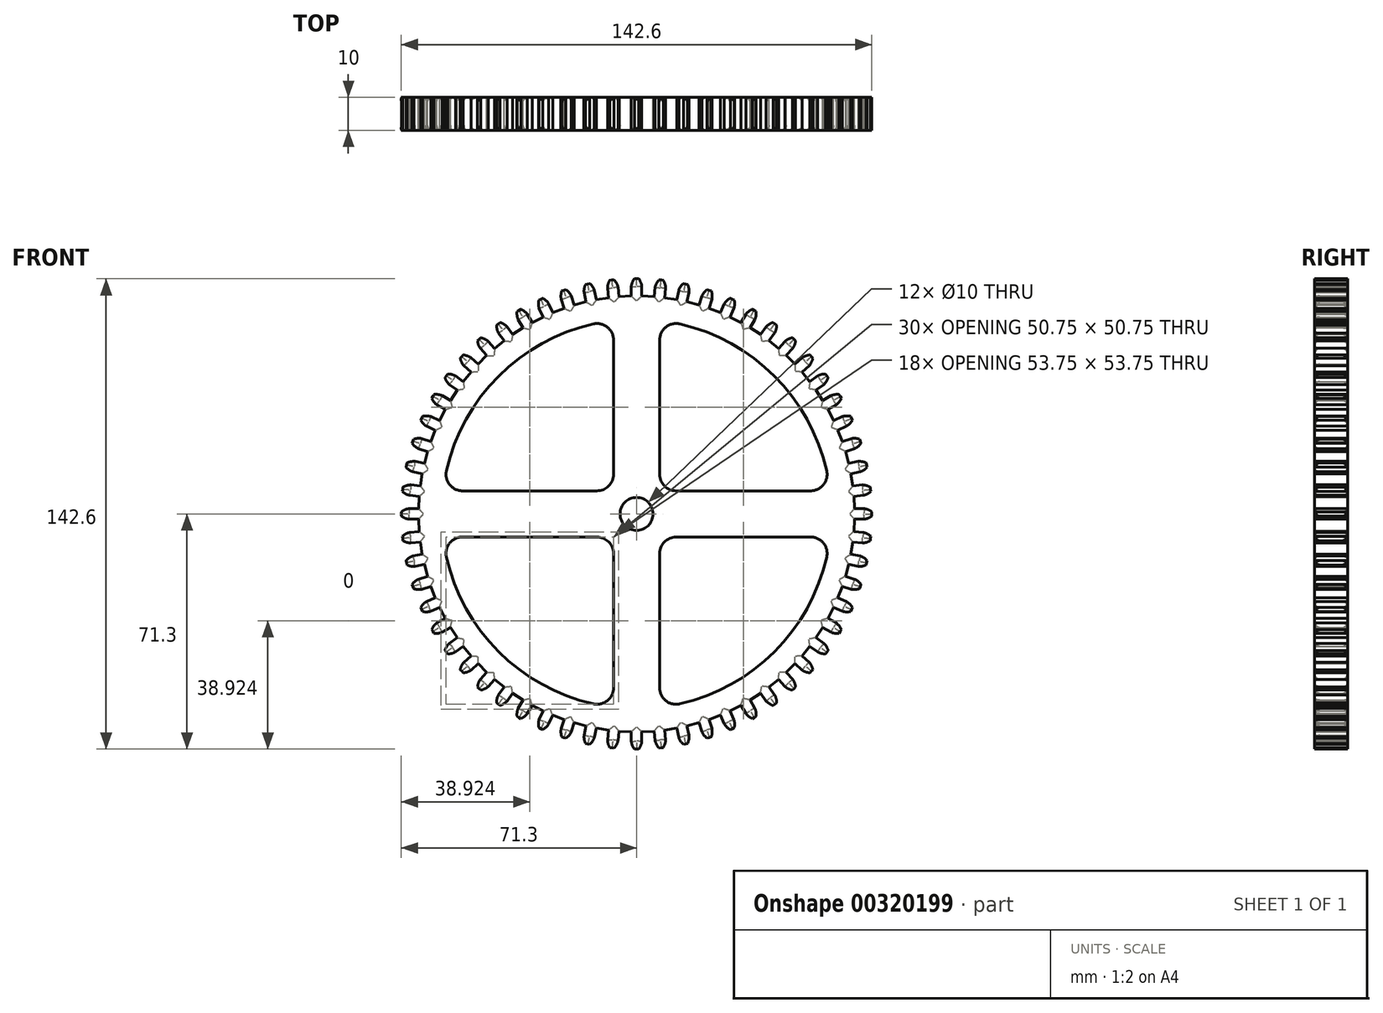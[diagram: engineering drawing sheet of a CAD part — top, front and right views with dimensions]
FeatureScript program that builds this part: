
annotation { "Feature Type Name" : "Feature", "Feature Type Description" : "" }
export const myFeature = defineFeature(function(context is Context, id is Id, definition is map)
    precondition{}
    {
        {
            var Q0;
            Q0=qCreatedBy(makeId("Front.planeOp"),FACE);
            var sketch = newSketch(context, id + "F0", { "sketchPlane" : qUnion([Q0])});
            skCircle(sketch, "E0", {"center": v(0, 0) * mm, "radius": 5 * mm});
            skLineSegment(sketch, "E1", {"start": v(1.6, 66.08) * mm, "end": v(1.6, 68.99) * mm});
            skArc(sketch, "E2", {"start": v(1.6, 67.83) * mm, "mid": v(1.47, 69.66) * mm, "end": v(0.66, 71.3) * mm});
            skLineSegment(sketch, "E3", {"start": v(0, 71.3) * mm, "end": v(0.66, 71.3) * mm});
            skLineSegment(sketch, "E4.MirrorCS", {"start": v(0, 71.3) * mm, "end": v(-0.66, 71.3) * mm});
            skArc(sketch, "E5.MirrorCS", {"start": v(-1.6, 67.83) * mm, "mid": v(-1.47, 69.66) * mm, "end": v(-0.66, 71.3) * mm});
            skLineSegment(sketch, "E6.MirrorCS", {"start": v(-1.6, 66.08) * mm, "end": v(-1.6, 68.99) * mm});
            skLineSegment(sketch, "E7.1.0", {"start": v(-8.5, 65.55) * mm, "end": v(-8.8, 68.44) * mm});
            skArc(sketch, "E7.1.1", {"start": v(-8.68, 67.3) * mm, "mid": v(-8.74, 69.12) * mm, "end": v(-8.1, 70.84) * mm});
            skLineSegment(sketch, "E7.1.2", {"start": v(-7.45, 70.9) * mm, "end": v(-8.1, 70.84) * mm});
            skLineSegment(sketch, "E7.1.3", {"start": v(-7.45, 70.9) * mm, "end": v(-6.8, 70.98) * mm});
            skArc(sketch, "E7.1.4", {"start": v(-5.5, 67.63) * mm, "mid": v(-5.82, 69.43) * mm, "end": v(-6.8, 70.98) * mm});
            skLineSegment(sketch, "E7.1.5", {"start": v(-5.32, 65.89) * mm, "end": v(-5.62, 68.78) * mm});
            skLineSegment(sketch, "E7.2.0", {"start": v(-15.3, 64.3) * mm, "end": v(-15.9, 67.15) * mm});
            skArc(sketch, "E7.2.1", {"start": v(-15.67, 66.02) * mm, "mid": v(-15.92, 67.83) * mm, "end": v(-15.47, 69.6) * mm});
            skLineSegment(sketch, "E7.2.2", {"start": v(-14.82, 69.74) * mm, "end": v(-15.47, 69.6) * mm});
            skLineSegment(sketch, "E7.2.3", {"start": v(-14.82, 69.74) * mm, "end": v(-14.18, 69.88) * mm});
            skArc(sketch, "E7.2.4", {"start": v(-12.54, 66.68) * mm, "mid": v(-13.05, 68.44) * mm, "end": v(-14.18, 69.88) * mm});
            skLineSegment(sketch, "E7.2.5", {"start": v(-12.17, 64.97) * mm, "end": v(-12.78, 67.81) * mm});
            skLineSegment(sketch, "E7.3.0", {"start": v(-21.94, 62.35) * mm, "end": v(-22.84, 65.12) * mm});
            skArc(sketch, "E7.3.1", {"start": v(-22.48, 64.02) * mm, "mid": v(-22.92, 65.8) * mm, "end": v(-22.66, 67.6) * mm});
            skLineSegment(sketch, "E7.3.2", {"start": v(-22.03, 67.81) * mm, "end": v(-22.66, 67.6) * mm});
            skLineSegment(sketch, "E7.3.3", {"start": v(-22.03, 67.81) * mm, "end": v(-21.4, 68.01) * mm});
            skArc(sketch, "E7.3.4", {"start": v(-19.44, 65) * mm, "mid": v(-20.13, 66.7) * mm, "end": v(-21.4, 68.01) * mm});
            skLineSegment(sketch, "E7.3.5", {"start": v(-18.9, 63.34) * mm, "end": v(-19.8, 66.1) * mm});
            skLineSegment(sketch, "E7.4.0", {"start": v(-28.34, 59.72) * mm, "end": v(-29.52, 62.37) * mm});
            skArc(sketch, "E7.4.1", {"start": v(-29.05, 61.32) * mm, "mid": v(-29.67, 63.04) * mm, "end": v(-29.6, 64.87) * mm});
            skLineSegment(sketch, "E7.4.2", {"start": v(-29, 65.14) * mm, "end": v(-29.6, 64.87) * mm});
            skLineSegment(sketch, "E7.4.3", {"start": v(-29, 65.14) * mm, "end": v(-28.4, 65.4) * mm});
            skArc(sketch, "E7.4.4", {"start": v(-26.13, 62.62) * mm, "mid": v(-26.99, 64.23) * mm, "end": v(-28.4, 65.4) * mm});
            skLineSegment(sketch, "E7.4.5", {"start": v(-25.42, 61.02) * mm, "end": v(-26.6, 63.68) * mm});
            skLineSegment(sketch, "E7.5.0", {"start": v(-34.43, 56.43) * mm, "end": v(-35.88, 58.95) * mm});
            skArc(sketch, "E7.5.1", {"start": v(-35.3, 57.94) * mm, "mid": v(-36.1, 59.59) * mm, "end": v(-36.22, 61.42) * mm});
            skLineSegment(sketch, "E7.5.2", {"start": v(-35.65, 61.75) * mm, "end": v(-36.22, 61.42) * mm});
            skLineSegment(sketch, "E7.5.3", {"start": v(-35.65, 61.75) * mm, "end": v(-35.08, 62.07) * mm});
            skArc(sketch, "E7.5.4", {"start": v(-32.53, 59.54) * mm, "mid": v(-33.56, 61.06) * mm, "end": v(-35.08, 62.07) * mm});
            skLineSegment(sketch, "E7.5.5", {"start": v(-31.65, 58.03) * mm, "end": v(-33.1, 60.55) * mm});
            skLineSegment(sketch, "E7.6.0", {"start": v(-40.14, 52.52) * mm, "end": v(-41.85, 54.87) * mm});
            skArc(sketch, "E7.6.1", {"start": v(-41.16, 53.94) * mm, "mid": v(-42.13, 55.49) * mm, "end": v(-42.44, 57.3) * mm});
            skLineSegment(sketch, "E7.6.2", {"start": v(-41.9, 57.68) * mm, "end": v(-42.44, 57.3) * mm});
            skLineSegment(sketch, "E7.6.3", {"start": v(-41.9, 57.68) * mm, "end": v(-41.38, 58.07) * mm});
            skArc(sketch, "E7.6.4", {"start": v(-38.58, 55.82) * mm, "mid": v(-39.75, 57.22) * mm, "end": v(-41.38, 58.07) * mm});
            skLineSegment(sketch, "E7.6.5", {"start": v(-37.55, 54.4) * mm, "end": v(-39.26, 56.75) * mm});
            skLineSegment(sketch, "E7.7.0", {"start": v(-45.4, 48.04) * mm, "end": v(-47.35, 50.2) * mm});
            skArc(sketch, "E7.7.1", {"start": v(-46.58, 49.34) * mm, "mid": v(-47.7, 50.78) * mm, "end": v(-48.2, 52.54) * mm});
            skLineSegment(sketch, "E7.7.2", {"start": v(-47.7, 52.99) * mm, "end": v(-48.2, 52.54) * mm});
            skLineSegment(sketch, "E7.7.3", {"start": v(-47.7, 52.99) * mm, "end": v(-47.22, 53.42) * mm});
            skArc(sketch, "E7.7.4", {"start": v(-44.2, 51.48) * mm, "mid": v(-45.52, 52.75) * mm, "end": v(-47.22, 53.42) * mm});
            skLineSegment(sketch, "E7.7.5", {"start": v(-43.03, 50.18) * mm, "end": v(-44.97, 52.34) * mm});
            skLineSegment(sketch, "E7.8.0", {"start": v(-50.18, 43.03) * mm, "end": v(-52.34, 44.97) * mm});
            skArc(sketch, "E7.8.1", {"start": v(-51.48, 44.2) * mm, "mid": v(-52.75, 45.52) * mm, "end": v(-53.42, 47.22) * mm});
            skLineSegment(sketch, "E7.8.2", {"start": v(-52.99, 47.7) * mm, "end": v(-53.42, 47.22) * mm});
            skLineSegment(sketch, "E7.8.3", {"start": v(-52.99, 47.7) * mm, "end": v(-52.54, 48.2) * mm});
            skArc(sketch, "E7.8.4", {"start": v(-49.34, 46.58) * mm, "mid": v(-50.78, 47.7) * mm, "end": v(-52.54, 48.2) * mm});
            skLineSegment(sketch, "E7.8.5", {"start": v(-48.04, 45.4) * mm, "end": v(-50.2, 47.35) * mm});
            skLineSegment(sketch, "E7.9.0", {"start": v(-54.4, 37.55) * mm, "end": v(-56.75, 39.26) * mm});
            skArc(sketch, "E7.9.1", {"start": v(-55.82, 38.58) * mm, "mid": v(-57.22, 39.75) * mm, "end": v(-58.07, 41.38) * mm});
            skLineSegment(sketch, "E7.9.2", {"start": v(-57.68, 41.9) * mm, "end": v(-58.07, 41.38) * mm});
            skLineSegment(sketch, "E7.9.3", {"start": v(-57.68, 41.9) * mm, "end": v(-57.3, 42.44) * mm});
            skArc(sketch, "E7.9.4", {"start": v(-53.94, 41.16) * mm, "mid": v(-55.49, 42.13) * mm, "end": v(-57.3, 42.44) * mm});
            skLineSegment(sketch, "E7.9.5", {"start": v(-52.52, 40.14) * mm, "end": v(-54.87, 41.85) * mm});
            skLineSegment(sketch, "E7.10.0", {"start": v(-58.03, 31.65) * mm, "end": v(-60.55, 33.1) * mm});
            skArc(sketch, "E7.10.1", {"start": v(-59.54, 32.53) * mm, "mid": v(-61.06, 33.56) * mm, "end": v(-62.07, 35.08) * mm});
            skLineSegment(sketch, "E7.10.2", {"start": v(-61.75, 35.65) * mm, "end": v(-62.07, 35.08) * mm});
            skLineSegment(sketch, "E7.10.3", {"start": v(-61.75, 35.65) * mm, "end": v(-61.42, 36.22) * mm});
            skArc(sketch, "E7.10.4", {"start": v(-57.94, 35.3) * mm, "mid": v(-59.59, 36.1) * mm, "end": v(-61.42, 36.22) * mm});
            skLineSegment(sketch, "E7.10.5", {"start": v(-56.43, 34.43) * mm, "end": v(-58.95, 35.88) * mm});
            skLineSegment(sketch, "E7.11.0", {"start": v(-61.02, 25.42) * mm, "end": v(-63.68, 26.6) * mm});
            skArc(sketch, "E7.11.1", {"start": v(-62.62, 26.13) * mm, "mid": v(-64.23, 26.99) * mm, "end": v(-65.4, 28.4) * mm});
            skLineSegment(sketch, "E7.11.2", {"start": v(-65.14, 29) * mm, "end": v(-65.4, 28.4) * mm});
            skLineSegment(sketch, "E7.11.3", {"start": v(-65.14, 29) * mm, "end": v(-64.87, 29.6) * mm});
            skArc(sketch, "E7.11.4", {"start": v(-61.32, 29.05) * mm, "mid": v(-63.04, 29.67) * mm, "end": v(-64.87, 29.6) * mm});
            skLineSegment(sketch, "E7.11.5", {"start": v(-59.72, 28.34) * mm, "end": v(-62.37, 29.52) * mm});
            skLineSegment(sketch, "E7.12.0", {"start": v(-63.34, 18.9) * mm, "end": v(-66.1, 19.8) * mm});
            skArc(sketch, "E7.12.1", {"start": v(-65, 19.44) * mm, "mid": v(-66.7, 20.13) * mm, "end": v(-68.01, 21.4) * mm});
            skLineSegment(sketch, "E7.12.2", {"start": v(-67.81, 22.03) * mm, "end": v(-68.01, 21.4) * mm});
            skLineSegment(sketch, "E7.12.3", {"start": v(-67.81, 22.03) * mm, "end": v(-67.6, 22.66) * mm});
            skArc(sketch, "E7.12.4", {"start": v(-64.02, 22.48) * mm, "mid": v(-65.8, 22.92) * mm, "end": v(-67.6, 22.66) * mm});
            skLineSegment(sketch, "E7.12.5", {"start": v(-62.35, 21.94) * mm, "end": v(-65.12, 22.84) * mm});
            skLineSegment(sketch, "E7.13.0", {"start": v(-64.97, 12.17) * mm, "end": v(-67.81, 12.78) * mm});
            skArc(sketch, "E7.13.1", {"start": v(-66.68, 12.54) * mm, "mid": v(-68.44, 13.05) * mm, "end": v(-69.88, 14.18) * mm});
            skLineSegment(sketch, "E7.13.2", {"start": v(-69.74, 14.82) * mm, "end": v(-69.88, 14.18) * mm});
            skLineSegment(sketch, "E7.13.3", {"start": v(-69.74, 14.82) * mm, "end": v(-69.6, 15.47) * mm});
            skArc(sketch, "E7.13.4", {"start": v(-66.02, 15.67) * mm, "mid": v(-67.83, 15.92) * mm, "end": v(-69.6, 15.47) * mm});
            skLineSegment(sketch, "E7.13.5", {"start": v(-64.3, 15.3) * mm, "end": v(-67.15, 15.9) * mm});
            skLineSegment(sketch, "E7.14.0", {"start": v(-65.89, 5.32) * mm, "end": v(-68.78, 5.62) * mm});
            skArc(sketch, "E7.14.1", {"start": v(-67.63, 5.5) * mm, "mid": v(-69.43, 5.82) * mm, "end": v(-70.98, 6.8) * mm});
            skLineSegment(sketch, "E7.14.2", {"start": v(-70.9, 7.45) * mm, "end": v(-70.98, 6.8) * mm});
            skLineSegment(sketch, "E7.14.3", {"start": v(-70.9, 7.45) * mm, "end": v(-70.84, 8.1) * mm});
            skArc(sketch, "E7.14.4", {"start": v(-67.3, 8.68) * mm, "mid": v(-69.12, 8.74) * mm, "end": v(-70.84, 8.1) * mm});
            skLineSegment(sketch, "E7.14.5", {"start": v(-65.55, 8.5) * mm, "end": v(-68.44, 8.8) * mm});
            skLineSegment(sketch, "E7.15.0", {"start": v(-66.08, -1.6) * mm, "end": v(-68.99, -1.6) * mm});
            skArc(sketch, "E7.15.1", {"start": v(-67.83, -1.6) * mm, "mid": v(-69.66, -1.47) * mm, "end": v(-71.3, -0.66) * mm});
            skLineSegment(sketch, "E7.15.2", {"start": v(-71.3, 0) * mm, "end": v(-71.3, -0.66) * mm});
            skLineSegment(sketch, "E7.15.3", {"start": v(-71.3, 0) * mm, "end": v(-71.3, 0.66) * mm});
            skArc(sketch, "E7.15.4", {"start": v(-67.83, 1.6) * mm, "mid": v(-69.66, 1.47) * mm, "end": v(-71.3, 0.66) * mm});
            skLineSegment(sketch, "E7.15.5", {"start": v(-66.08, 1.6) * mm, "end": v(-68.99, 1.6) * mm});
            skLineSegment(sketch, "E7.16.0", {"start": v(-65.55, -8.5) * mm, "end": v(-68.44, -8.8) * mm});
            skArc(sketch, "E7.16.1", {"start": v(-67.3, -8.68) * mm, "mid": v(-69.12, -8.74) * mm, "end": v(-70.84, -8.1) * mm});
            skLineSegment(sketch, "E7.16.2", {"start": v(-70.9, -7.45) * mm, "end": v(-70.84, -8.1) * mm});
            skLineSegment(sketch, "E7.16.3", {"start": v(-70.9, -7.45) * mm, "end": v(-70.98, -6.8) * mm});
            skArc(sketch, "E7.16.4", {"start": v(-67.63, -5.5) * mm, "mid": v(-69.43, -5.82) * mm, "end": v(-70.98, -6.8) * mm});
            skLineSegment(sketch, "E7.16.5", {"start": v(-65.89, -5.32) * mm, "end": v(-68.78, -5.62) * mm});
            skLineSegment(sketch, "E7.17.0", {"start": v(-64.3, -15.3) * mm, "end": v(-67.15, -15.9) * mm});
            skArc(sketch, "E7.17.1", {"start": v(-66.02, -15.67) * mm, "mid": v(-67.83, -15.92) * mm, "end": v(-69.6, -15.47) * mm});
            skLineSegment(sketch, "E7.17.2", {"start": v(-69.74, -14.82) * mm, "end": v(-69.6, -15.47) * mm});
            skLineSegment(sketch, "E7.17.3", {"start": v(-69.74, -14.82) * mm, "end": v(-69.88, -14.18) * mm});
            skArc(sketch, "E7.17.4", {"start": v(-66.68, -12.54) * mm, "mid": v(-68.44, -13.05) * mm, "end": v(-69.88, -14.18) * mm});
            skLineSegment(sketch, "E7.17.5", {"start": v(-64.97, -12.17) * mm, "end": v(-67.81, -12.78) * mm});
            skLineSegment(sketch, "E7.18.0", {"start": v(-62.35, -21.94) * mm, "end": v(-65.12, -22.84) * mm});
            skArc(sketch, "E7.18.1", {"start": v(-64.02, -22.48) * mm, "mid": v(-65.8, -22.92) * mm, "end": v(-67.6, -22.66) * mm});
            skLineSegment(sketch, "E7.18.2", {"start": v(-67.81, -22.03) * mm, "end": v(-67.6, -22.66) * mm});
            skLineSegment(sketch, "E7.18.3", {"start": v(-67.81, -22.03) * mm, "end": v(-68.01, -21.4) * mm});
            skArc(sketch, "E7.18.4", {"start": v(-65, -19.44) * mm, "mid": v(-66.7, -20.13) * mm, "end": v(-68.01, -21.4) * mm});
            skLineSegment(sketch, "E7.18.5", {"start": v(-63.34, -18.9) * mm, "end": v(-66.1, -19.8) * mm});
            skLineSegment(sketch, "E7.19.0", {"start": v(-59.72, -28.34) * mm, "end": v(-62.37, -29.52) * mm});
            skArc(sketch, "E7.19.1", {"start": v(-61.32, -29.05) * mm, "mid": v(-63.04, -29.67) * mm, "end": v(-64.87, -29.6) * mm});
            skLineSegment(sketch, "E7.19.2", {"start": v(-65.14, -29) * mm, "end": v(-64.87, -29.6) * mm});
            skLineSegment(sketch, "E7.19.3", {"start": v(-65.14, -29) * mm, "end": v(-65.4, -28.4) * mm});
            skArc(sketch, "E7.19.4", {"start": v(-62.62, -26.13) * mm, "mid": v(-64.23, -26.99) * mm, "end": v(-65.4, -28.4) * mm});
            skLineSegment(sketch, "E7.19.5", {"start": v(-61.02, -25.42) * mm, "end": v(-63.68, -26.6) * mm});
            skLineSegment(sketch, "E7.20.0", {"start": v(-56.43, -34.43) * mm, "end": v(-58.95, -35.88) * mm});
            skArc(sketch, "E7.20.1", {"start": v(-57.94, -35.3) * mm, "mid": v(-59.59, -36.1) * mm, "end": v(-61.42, -36.22) * mm});
            skLineSegment(sketch, "E7.20.2", {"start": v(-61.75, -35.65) * mm, "end": v(-61.42, -36.22) * mm});
            skLineSegment(sketch, "E7.20.3", {"start": v(-61.75, -35.65) * mm, "end": v(-62.07, -35.08) * mm});
            skArc(sketch, "E7.20.4", {"start": v(-59.54, -32.53) * mm, "mid": v(-61.06, -33.56) * mm, "end": v(-62.07, -35.08) * mm});
            skLineSegment(sketch, "E7.20.5", {"start": v(-58.03, -31.65) * mm, "end": v(-60.55, -33.1) * mm});
            skLineSegment(sketch, "E7.21.0", {"start": v(-52.52, -40.14) * mm, "end": v(-54.87, -41.85) * mm});
            skArc(sketch, "E7.21.1", {"start": v(-53.94, -41.16) * mm, "mid": v(-55.49, -42.13) * mm, "end": v(-57.3, -42.44) * mm});
            skLineSegment(sketch, "E7.21.2", {"start": v(-57.68, -41.9) * mm, "end": v(-57.3, -42.44) * mm});
            skLineSegment(sketch, "E7.21.3", {"start": v(-57.68, -41.9) * mm, "end": v(-58.07, -41.38) * mm});
            skArc(sketch, "E7.21.4", {"start": v(-55.82, -38.58) * mm, "mid": v(-57.22, -39.75) * mm, "end": v(-58.07, -41.38) * mm});
            skLineSegment(sketch, "E7.21.5", {"start": v(-54.4, -37.55) * mm, "end": v(-56.75, -39.26) * mm});
            skLineSegment(sketch, "E7.22.0", {"start": v(-48.04, -45.4) * mm, "end": v(-50.2, -47.35) * mm});
            skArc(sketch, "E7.22.1", {"start": v(-49.34, -46.58) * mm, "mid": v(-50.78, -47.7) * mm, "end": v(-52.54, -48.2) * mm});
            skLineSegment(sketch, "E7.22.2", {"start": v(-52.99, -47.7) * mm, "end": v(-52.54, -48.2) * mm});
            skLineSegment(sketch, "E7.22.3", {"start": v(-52.99, -47.7) * mm, "end": v(-53.42, -47.22) * mm});
            skArc(sketch, "E7.22.4", {"start": v(-51.48, -44.2) * mm, "mid": v(-52.75, -45.52) * mm, "end": v(-53.42, -47.22) * mm});
            skLineSegment(sketch, "E7.22.5", {"start": v(-50.18, -43.03) * mm, "end": v(-52.34, -44.97) * mm});
            skLineSegment(sketch, "E7.23.0", {"start": v(-43.03, -50.18) * mm, "end": v(-44.97, -52.34) * mm});
            skArc(sketch, "E7.23.1", {"start": v(-44.2, -51.48) * mm, "mid": v(-45.52, -52.75) * mm, "end": v(-47.22, -53.42) * mm});
            skLineSegment(sketch, "E7.23.2", {"start": v(-47.7, -52.99) * mm, "end": v(-47.22, -53.42) * mm});
            skLineSegment(sketch, "E7.23.3", {"start": v(-47.7, -52.99) * mm, "end": v(-48.2, -52.54) * mm});
            skArc(sketch, "E7.23.4", {"start": v(-46.58, -49.34) * mm, "mid": v(-47.7, -50.78) * mm, "end": v(-48.2, -52.54) * mm});
            skLineSegment(sketch, "E7.23.5", {"start": v(-45.4, -48.04) * mm, "end": v(-47.35, -50.2) * mm});
            skLineSegment(sketch, "E7.24.0", {"start": v(-37.55, -54.4) * mm, "end": v(-39.26, -56.75) * mm});
            skArc(sketch, "E7.24.1", {"start": v(-38.58, -55.82) * mm, "mid": v(-39.75, -57.22) * mm, "end": v(-41.38, -58.07) * mm});
            skLineSegment(sketch, "E7.24.2", {"start": v(-41.9, -57.68) * mm, "end": v(-41.38, -58.07) * mm});
            skLineSegment(sketch, "E7.24.3", {"start": v(-41.9, -57.68) * mm, "end": v(-42.44, -57.3) * mm});
            skArc(sketch, "E7.24.4", {"start": v(-41.16, -53.94) * mm, "mid": v(-42.13, -55.49) * mm, "end": v(-42.44, -57.3) * mm});
            skLineSegment(sketch, "E7.24.5", {"start": v(-40.14, -52.52) * mm, "end": v(-41.85, -54.87) * mm});
            skLineSegment(sketch, "E7.25.0", {"start": v(-31.65, -58.03) * mm, "end": v(-33.1, -60.55) * mm});
            skArc(sketch, "E7.25.1", {"start": v(-32.53, -59.54) * mm, "mid": v(-33.56, -61.06) * mm, "end": v(-35.08, -62.07) * mm});
            skLineSegment(sketch, "E7.25.2", {"start": v(-35.65, -61.75) * mm, "end": v(-35.08, -62.07) * mm});
            skLineSegment(sketch, "E7.25.3", {"start": v(-35.65, -61.75) * mm, "end": v(-36.22, -61.42) * mm});
            skArc(sketch, "E7.25.4", {"start": v(-35.3, -57.94) * mm, "mid": v(-36.1, -59.59) * mm, "end": v(-36.22, -61.42) * mm});
            skLineSegment(sketch, "E7.25.5", {"start": v(-34.43, -56.43) * mm, "end": v(-35.88, -58.95) * mm});
            skLineSegment(sketch, "E7.26.0", {"start": v(-25.42, -61.02) * mm, "end": v(-26.6, -63.68) * mm});
            skArc(sketch, "E7.26.1", {"start": v(-26.13, -62.62) * mm, "mid": v(-26.99, -64.23) * mm, "end": v(-28.4, -65.4) * mm});
            skLineSegment(sketch, "E7.26.2", {"start": v(-29, -65.14) * mm, "end": v(-28.4, -65.4) * mm});
            skLineSegment(sketch, "E7.26.3", {"start": v(-29, -65.14) * mm, "end": v(-29.6, -64.87) * mm});
            skArc(sketch, "E7.26.4", {"start": v(-29.05, -61.32) * mm, "mid": v(-29.67, -63.04) * mm, "end": v(-29.6, -64.87) * mm});
            skLineSegment(sketch, "E7.26.5", {"start": v(-28.34, -59.72) * mm, "end": v(-29.52, -62.37) * mm});
            skLineSegment(sketch, "E7.27.0", {"start": v(-18.9, -63.34) * mm, "end": v(-19.8, -66.1) * mm});
            skArc(sketch, "E7.27.1", {"start": v(-19.44, -65) * mm, "mid": v(-20.13, -66.7) * mm, "end": v(-21.4, -68.01) * mm});
            skLineSegment(sketch, "E7.27.2", {"start": v(-22.03, -67.81) * mm, "end": v(-21.4, -68.01) * mm});
            skLineSegment(sketch, "E7.27.3", {"start": v(-22.03, -67.81) * mm, "end": v(-22.66, -67.6) * mm});
            skArc(sketch, "E7.27.4", {"start": v(-22.48, -64.02) * mm, "mid": v(-22.92, -65.8) * mm, "end": v(-22.66, -67.6) * mm});
            skLineSegment(sketch, "E7.27.5", {"start": v(-21.94, -62.35) * mm, "end": v(-22.84, -65.12) * mm});
            skLineSegment(sketch, "E7.28.0", {"start": v(-12.17, -64.97) * mm, "end": v(-12.78, -67.81) * mm});
            skArc(sketch, "E7.28.1", {"start": v(-12.54, -66.68) * mm, "mid": v(-13.05, -68.44) * mm, "end": v(-14.18, -69.88) * mm});
            skLineSegment(sketch, "E7.28.2", {"start": v(-14.82, -69.74) * mm, "end": v(-14.18, -69.88) * mm});
            skLineSegment(sketch, "E7.28.3", {"start": v(-14.82, -69.74) * mm, "end": v(-15.47, -69.6) * mm});
            skArc(sketch, "E7.28.4", {"start": v(-15.67, -66.02) * mm, "mid": v(-15.92, -67.83) * mm, "end": v(-15.47, -69.6) * mm});
            skLineSegment(sketch, "E7.28.5", {"start": v(-15.3, -64.3) * mm, "end": v(-15.9, -67.15) * mm});
            skLineSegment(sketch, "E7.29.0", {"start": v(-5.32, -65.89) * mm, "end": v(-5.62, -68.78) * mm});
            skArc(sketch, "E7.29.1", {"start": v(-5.5, -67.63) * mm, "mid": v(-5.82, -69.43) * mm, "end": v(-6.8, -70.98) * mm});
            skLineSegment(sketch, "E7.29.2", {"start": v(-7.45, -70.9) * mm, "end": v(-6.8, -70.98) * mm});
            skLineSegment(sketch, "E7.29.3", {"start": v(-7.45, -70.9) * mm, "end": v(-8.1, -70.84) * mm});
            skArc(sketch, "E7.29.4", {"start": v(-8.68, -67.3) * mm, "mid": v(-8.74, -69.12) * mm, "end": v(-8.1, -70.84) * mm});
            skLineSegment(sketch, "E7.29.5", {"start": v(-8.5, -65.55) * mm, "end": v(-8.8, -68.44) * mm});
            skLineSegment(sketch, "E7.30.0", {"start": v(1.6, -66.08) * mm, "end": v(1.6, -68.99) * mm});
            skArc(sketch, "E7.30.1", {"start": v(1.6, -67.83) * mm, "mid": v(1.47, -69.66) * mm, "end": v(0.66, -71.3) * mm});
            skLineSegment(sketch, "E7.30.2", {"start": v(0, -71.3) * mm, "end": v(0.66, -71.3) * mm});
            skLineSegment(sketch, "E7.30.3", {"start": v(0, -71.3) * mm, "end": v(-0.66, -71.3) * mm});
            skArc(sketch, "E7.30.4", {"start": v(-1.6, -67.83) * mm, "mid": v(-1.47, -69.66) * mm, "end": v(-0.66, -71.3) * mm});
            skLineSegment(sketch, "E7.30.5", {"start": v(-1.6, -66.08) * mm, "end": v(-1.6, -68.99) * mm});
            skLineSegment(sketch, "E7.31.0", {"start": v(8.5, -65.55) * mm, "end": v(8.8, -68.44) * mm});
            skArc(sketch, "E7.31.1", {"start": v(8.68, -67.3) * mm, "mid": v(8.74, -69.12) * mm, "end": v(8.1, -70.84) * mm});
            skLineSegment(sketch, "E7.31.2", {"start": v(7.45, -70.9) * mm, "end": v(8.1, -70.84) * mm});
            skLineSegment(sketch, "E7.31.3", {"start": v(7.45, -70.9) * mm, "end": v(6.8, -70.98) * mm});
            skArc(sketch, "E7.31.4", {"start": v(5.5, -67.63) * mm, "mid": v(5.82, -69.43) * mm, "end": v(6.8, -70.98) * mm});
            skLineSegment(sketch, "E7.31.5", {"start": v(5.32, -65.89) * mm, "end": v(5.62, -68.78) * mm});
            skLineSegment(sketch, "E7.32.0", {"start": v(15.3, -64.3) * mm, "end": v(15.9, -67.15) * mm});
            skArc(sketch, "E7.32.1", {"start": v(15.67, -66.02) * mm, "mid": v(15.92, -67.83) * mm, "end": v(15.47, -69.6) * mm});
            skLineSegment(sketch, "E7.32.2", {"start": v(14.82, -69.74) * mm, "end": v(15.47, -69.6) * mm});
            skLineSegment(sketch, "E7.32.3", {"start": v(14.82, -69.74) * mm, "end": v(14.18, -69.88) * mm});
            skArc(sketch, "E7.32.4", {"start": v(12.54, -66.68) * mm, "mid": v(13.05, -68.44) * mm, "end": v(14.18, -69.88) * mm});
            skLineSegment(sketch, "E7.32.5", {"start": v(12.17, -64.97) * mm, "end": v(12.78, -67.81) * mm});
            skLineSegment(sketch, "E7.33.0", {"start": v(21.94, -62.35) * mm, "end": v(22.84, -65.12) * mm});
            skArc(sketch, "E7.33.1", {"start": v(22.48, -64.02) * mm, "mid": v(22.92, -65.8) * mm, "end": v(22.66, -67.6) * mm});
            skLineSegment(sketch, "E7.33.2", {"start": v(22.03, -67.81) * mm, "end": v(22.66, -67.6) * mm});
            skLineSegment(sketch, "E7.33.3", {"start": v(22.03, -67.81) * mm, "end": v(21.4, -68.01) * mm});
            skArc(sketch, "E7.33.4", {"start": v(19.44, -65) * mm, "mid": v(20.13, -66.7) * mm, "end": v(21.4, -68.01) * mm});
            skLineSegment(sketch, "E7.33.5", {"start": v(18.9, -63.34) * mm, "end": v(19.8, -66.1) * mm});
            skLineSegment(sketch, "E7.34.0", {"start": v(28.34, -59.72) * mm, "end": v(29.52, -62.37) * mm});
            skArc(sketch, "E7.34.1", {"start": v(29.05, -61.32) * mm, "mid": v(29.67, -63.04) * mm, "end": v(29.6, -64.87) * mm});
            skLineSegment(sketch, "E7.34.2", {"start": v(29, -65.14) * mm, "end": v(29.6, -64.87) * mm});
            skLineSegment(sketch, "E7.34.3", {"start": v(29, -65.14) * mm, "end": v(28.4, -65.4) * mm});
            skArc(sketch, "E7.34.4", {"start": v(26.13, -62.62) * mm, "mid": v(26.99, -64.23) * mm, "end": v(28.4, -65.4) * mm});
            skLineSegment(sketch, "E7.34.5", {"start": v(25.42, -61.02) * mm, "end": v(26.6, -63.68) * mm});
            skLineSegment(sketch, "E7.35.0", {"start": v(34.43, -56.43) * mm, "end": v(35.88, -58.95) * mm});
            skArc(sketch, "E7.35.1", {"start": v(35.3, -57.94) * mm, "mid": v(36.1, -59.59) * mm, "end": v(36.22, -61.42) * mm});
            skLineSegment(sketch, "E7.35.2", {"start": v(35.65, -61.75) * mm, "end": v(36.22, -61.42) * mm});
            skLineSegment(sketch, "E7.35.3", {"start": v(35.65, -61.75) * mm, "end": v(35.08, -62.07) * mm});
            skArc(sketch, "E7.35.4", {"start": v(32.53, -59.54) * mm, "mid": v(33.56, -61.06) * mm, "end": v(35.08, -62.07) * mm});
            skLineSegment(sketch, "E7.35.5", {"start": v(31.65, -58.03) * mm, "end": v(33.1, -60.55) * mm});
            skLineSegment(sketch, "E7.36.0", {"start": v(40.14, -52.52) * mm, "end": v(41.85, -54.87) * mm});
            skArc(sketch, "E7.36.1", {"start": v(41.16, -53.94) * mm, "mid": v(42.13, -55.49) * mm, "end": v(42.44, -57.3) * mm});
            skLineSegment(sketch, "E7.36.2", {"start": v(41.9, -57.68) * mm, "end": v(42.44, -57.3) * mm});
            skLineSegment(sketch, "E7.36.3", {"start": v(41.9, -57.68) * mm, "end": v(41.38, -58.07) * mm});
            skArc(sketch, "E7.36.4", {"start": v(38.58, -55.82) * mm, "mid": v(39.75, -57.22) * mm, "end": v(41.38, -58.07) * mm});
            skLineSegment(sketch, "E7.36.5", {"start": v(37.55, -54.4) * mm, "end": v(39.26, -56.75) * mm});
            skLineSegment(sketch, "E7.37.0", {"start": v(45.4, -48.04) * mm, "end": v(47.35, -50.2) * mm});
            skArc(sketch, "E7.37.1", {"start": v(46.58, -49.34) * mm, "mid": v(47.7, -50.78) * mm, "end": v(48.2, -52.54) * mm});
            skLineSegment(sketch, "E7.37.2", {"start": v(47.7, -52.99) * mm, "end": v(48.2, -52.54) * mm});
            skLineSegment(sketch, "E7.37.3", {"start": v(47.7, -52.99) * mm, "end": v(47.22, -53.42) * mm});
            skArc(sketch, "E7.37.4", {"start": v(44.2, -51.48) * mm, "mid": v(45.52, -52.75) * mm, "end": v(47.22, -53.42) * mm});
            skLineSegment(sketch, "E7.37.5", {"start": v(43.03, -50.18) * mm, "end": v(44.97, -52.34) * mm});
            skLineSegment(sketch, "E7.38.0", {"start": v(50.18, -43.03) * mm, "end": v(52.34, -44.97) * mm});
            skArc(sketch, "E7.38.1", {"start": v(51.48, -44.2) * mm, "mid": v(52.75, -45.52) * mm, "end": v(53.42, -47.22) * mm});
            skLineSegment(sketch, "E7.38.2", {"start": v(52.99, -47.7) * mm, "end": v(53.42, -47.22) * mm});
            skLineSegment(sketch, "E7.38.3", {"start": v(52.99, -47.7) * mm, "end": v(52.54, -48.2) * mm});
            skArc(sketch, "E7.38.4", {"start": v(49.34, -46.58) * mm, "mid": v(50.78, -47.7) * mm, "end": v(52.54, -48.2) * mm});
            skLineSegment(sketch, "E7.38.5", {"start": v(48.04, -45.4) * mm, "end": v(50.2, -47.35) * mm});
            skLineSegment(sketch, "E7.39.0", {"start": v(54.4, -37.55) * mm, "end": v(56.75, -39.26) * mm});
            skArc(sketch, "E7.39.1", {"start": v(55.82, -38.58) * mm, "mid": v(57.22, -39.75) * mm, "end": v(58.07, -41.38) * mm});
            skLineSegment(sketch, "E7.39.2", {"start": v(57.68, -41.9) * mm, "end": v(58.07, -41.38) * mm});
            skLineSegment(sketch, "E7.39.3", {"start": v(57.68, -41.9) * mm, "end": v(57.3, -42.44) * mm});
            skArc(sketch, "E7.39.4", {"start": v(53.94, -41.16) * mm, "mid": v(55.49, -42.13) * mm, "end": v(57.3, -42.44) * mm});
            skLineSegment(sketch, "E7.39.5", {"start": v(52.52, -40.14) * mm, "end": v(54.87, -41.85) * mm});
            skLineSegment(sketch, "E7.40.0", {"start": v(58.03, -31.65) * mm, "end": v(60.55, -33.1) * mm});
            skArc(sketch, "E7.40.1", {"start": v(59.54, -32.53) * mm, "mid": v(61.06, -33.56) * mm, "end": v(62.07, -35.08) * mm});
            skLineSegment(sketch, "E7.40.2", {"start": v(61.75, -35.65) * mm, "end": v(62.07, -35.08) * mm});
            skLineSegment(sketch, "E7.40.3", {"start": v(61.75, -35.65) * mm, "end": v(61.42, -36.22) * mm});
            skArc(sketch, "E7.40.4", {"start": v(57.94, -35.3) * mm, "mid": v(59.59, -36.1) * mm, "end": v(61.42, -36.22) * mm});
            skLineSegment(sketch, "E7.40.5", {"start": v(56.43, -34.43) * mm, "end": v(58.95, -35.88) * mm});
            skLineSegment(sketch, "E7.41.0", {"start": v(61.02, -25.42) * mm, "end": v(63.68, -26.6) * mm});
            skArc(sketch, "E7.41.1", {"start": v(62.62, -26.13) * mm, "mid": v(64.23, -26.99) * mm, "end": v(65.4, -28.4) * mm});
            skLineSegment(sketch, "E7.41.2", {"start": v(65.14, -29) * mm, "end": v(65.4, -28.4) * mm});
            skLineSegment(sketch, "E7.41.3", {"start": v(65.14, -29) * mm, "end": v(64.87, -29.6) * mm});
            skArc(sketch, "E7.41.4", {"start": v(61.32, -29.05) * mm, "mid": v(63.04, -29.67) * mm, "end": v(64.87, -29.6) * mm});
            skLineSegment(sketch, "E7.41.5", {"start": v(59.72, -28.34) * mm, "end": v(62.37, -29.52) * mm});
            skLineSegment(sketch, "E7.42.0", {"start": v(63.34, -18.9) * mm, "end": v(66.1, -19.8) * mm});
            skArc(sketch, "E7.42.1", {"start": v(65, -19.44) * mm, "mid": v(66.7, -20.13) * mm, "end": v(68.01, -21.4) * mm});
            skLineSegment(sketch, "E7.42.2", {"start": v(67.81, -22.03) * mm, "end": v(68.01, -21.4) * mm});
            skLineSegment(sketch, "E7.42.3", {"start": v(67.81, -22.03) * mm, "end": v(67.6, -22.66) * mm});
            skArc(sketch, "E7.42.4", {"start": v(64.02, -22.48) * mm, "mid": v(65.8, -22.92) * mm, "end": v(67.6, -22.66) * mm});
            skLineSegment(sketch, "E7.42.5", {"start": v(62.35, -21.94) * mm, "end": v(65.12, -22.84) * mm});
            skLineSegment(sketch, "E7.43.0", {"start": v(64.97, -12.17) * mm, "end": v(67.81, -12.78) * mm});
            skArc(sketch, "E7.43.1", {"start": v(66.68, -12.54) * mm, "mid": v(68.44, -13.05) * mm, "end": v(69.88, -14.18) * mm});
            skLineSegment(sketch, "E7.43.2", {"start": v(69.74, -14.82) * mm, "end": v(69.88, -14.18) * mm});
            skLineSegment(sketch, "E7.43.3", {"start": v(69.74, -14.82) * mm, "end": v(69.6, -15.47) * mm});
            skArc(sketch, "E7.43.4", {"start": v(66.02, -15.67) * mm, "mid": v(67.83, -15.92) * mm, "end": v(69.6, -15.47) * mm});
            skLineSegment(sketch, "E7.43.5", {"start": v(64.3, -15.3) * mm, "end": v(67.15, -15.9) * mm});
            skLineSegment(sketch, "E7.44.0", {"start": v(65.89, -5.32) * mm, "end": v(68.78, -5.62) * mm});
            skArc(sketch, "E7.44.1", {"start": v(67.63, -5.5) * mm, "mid": v(69.43, -5.82) * mm, "end": v(70.98, -6.8) * mm});
            skLineSegment(sketch, "E7.44.2", {"start": v(70.9, -7.45) * mm, "end": v(70.98, -6.8) * mm});
            skLineSegment(sketch, "E7.44.3", {"start": v(70.9, -7.45) * mm, "end": v(70.84, -8.1) * mm});
            skArc(sketch, "E7.44.4", {"start": v(67.3, -8.68) * mm, "mid": v(69.12, -8.74) * mm, "end": v(70.84, -8.1) * mm});
            skLineSegment(sketch, "E7.44.5", {"start": v(65.55, -8.5) * mm, "end": v(68.44, -8.8) * mm});
            skLineSegment(sketch, "E7.45.0", {"start": v(66.08, 1.6) * mm, "end": v(68.99, 1.6) * mm});
            skArc(sketch, "E7.45.1", {"start": v(67.83, 1.6) * mm, "mid": v(69.66, 1.47) * mm, "end": v(71.3, 0.66) * mm});
            skLineSegment(sketch, "E7.45.2", {"start": v(71.3, 0) * mm, "end": v(71.3, 0.66) * mm});
            skLineSegment(sketch, "E7.45.3", {"start": v(71.3, 0) * mm, "end": v(71.3, -0.66) * mm});
            skArc(sketch, "E7.45.4", {"start": v(67.83, -1.6) * mm, "mid": v(69.66, -1.47) * mm, "end": v(71.3, -0.66) * mm});
            skLineSegment(sketch, "E7.45.5", {"start": v(66.08, -1.6) * mm, "end": v(68.99, -1.6) * mm});
            skLineSegment(sketch, "E7.46.0", {"start": v(65.55, 8.5) * mm, "end": v(68.44, 8.8) * mm});
            skArc(sketch, "E7.46.1", {"start": v(67.3, 8.68) * mm, "mid": v(69.12, 8.74) * mm, "end": v(70.84, 8.1) * mm});
            skLineSegment(sketch, "E7.46.2", {"start": v(70.9, 7.45) * mm, "end": v(70.84, 8.1) * mm});
            skLineSegment(sketch, "E7.46.3", {"start": v(70.9, 7.45) * mm, "end": v(70.98, 6.8) * mm});
            skArc(sketch, "E7.46.4", {"start": v(67.63, 5.5) * mm, "mid": v(69.43, 5.82) * mm, "end": v(70.98, 6.8) * mm});
            skLineSegment(sketch, "E7.46.5", {"start": v(65.89, 5.32) * mm, "end": v(68.78, 5.62) * mm});
            skLineSegment(sketch, "E7.47.0", {"start": v(64.3, 15.3) * mm, "end": v(67.15, 15.9) * mm});
            skArc(sketch, "E7.47.1", {"start": v(66.02, 15.67) * mm, "mid": v(67.83, 15.92) * mm, "end": v(69.6, 15.47) * mm});
            skLineSegment(sketch, "E7.47.2", {"start": v(69.74, 14.82) * mm, "end": v(69.6, 15.47) * mm});
            skLineSegment(sketch, "E7.47.3", {"start": v(69.74, 14.82) * mm, "end": v(69.88, 14.18) * mm});
            skArc(sketch, "E7.47.4", {"start": v(66.68, 12.54) * mm, "mid": v(68.44, 13.05) * mm, "end": v(69.88, 14.18) * mm});
            skLineSegment(sketch, "E7.47.5", {"start": v(64.97, 12.17) * mm, "end": v(67.81, 12.78) * mm});
            skLineSegment(sketch, "E7.48.0", {"start": v(62.35, 21.94) * mm, "end": v(65.12, 22.84) * mm});
            skArc(sketch, "E7.48.1", {"start": v(64.02, 22.48) * mm, "mid": v(65.8, 22.92) * mm, "end": v(67.6, 22.66) * mm});
            skLineSegment(sketch, "E7.48.2", {"start": v(67.81, 22.03) * mm, "end": v(67.6, 22.66) * mm});
            skLineSegment(sketch, "E7.48.3", {"start": v(67.81, 22.03) * mm, "end": v(68.01, 21.4) * mm});
            skArc(sketch, "E7.48.4", {"start": v(65, 19.44) * mm, "mid": v(66.7, 20.13) * mm, "end": v(68.01, 21.4) * mm});
            skLineSegment(sketch, "E7.48.5", {"start": v(63.34, 18.9) * mm, "end": v(66.1, 19.8) * mm});
            skLineSegment(sketch, "E7.49.0", {"start": v(59.72, 28.34) * mm, "end": v(62.37, 29.52) * mm});
            skArc(sketch, "E7.49.1", {"start": v(61.32, 29.05) * mm, "mid": v(63.04, 29.67) * mm, "end": v(64.87, 29.6) * mm});
            skLineSegment(sketch, "E7.49.2", {"start": v(65.14, 29) * mm, "end": v(64.87, 29.6) * mm});
            skLineSegment(sketch, "E7.49.3", {"start": v(65.14, 29) * mm, "end": v(65.4, 28.4) * mm});
            skArc(sketch, "E7.49.4", {"start": v(62.62, 26.13) * mm, "mid": v(64.23, 26.99) * mm, "end": v(65.4, 28.4) * mm});
            skLineSegment(sketch, "E7.49.5", {"start": v(61.02, 25.42) * mm, "end": v(63.68, 26.6) * mm});
            skLineSegment(sketch, "E7.50.0", {"start": v(56.43, 34.43) * mm, "end": v(58.95, 35.88) * mm});
            skArc(sketch, "E7.50.1", {"start": v(57.94, 35.3) * mm, "mid": v(59.59, 36.1) * mm, "end": v(61.42, 36.22) * mm});
            skLineSegment(sketch, "E7.50.2", {"start": v(61.75, 35.65) * mm, "end": v(61.42, 36.22) * mm});
            skLineSegment(sketch, "E7.50.3", {"start": v(61.75, 35.65) * mm, "end": v(62.07, 35.08) * mm});
            skArc(sketch, "E7.50.4", {"start": v(59.54, 32.53) * mm, "mid": v(61.06, 33.56) * mm, "end": v(62.07, 35.08) * mm});
            skLineSegment(sketch, "E7.50.5", {"start": v(58.03, 31.65) * mm, "end": v(60.55, 33.1) * mm});
            skLineSegment(sketch, "E7.51.0", {"start": v(52.52, 40.14) * mm, "end": v(54.87, 41.85) * mm});
            skArc(sketch, "E7.51.1", {"start": v(53.94, 41.16) * mm, "mid": v(55.49, 42.13) * mm, "end": v(57.3, 42.44) * mm});
            skLineSegment(sketch, "E7.51.2", {"start": v(57.68, 41.9) * mm, "end": v(57.3, 42.44) * mm});
            skLineSegment(sketch, "E7.51.3", {"start": v(57.68, 41.9) * mm, "end": v(58.07, 41.38) * mm});
            skArc(sketch, "E7.51.4", {"start": v(55.82, 38.58) * mm, "mid": v(57.22, 39.75) * mm, "end": v(58.07, 41.38) * mm});
            skLineSegment(sketch, "E7.51.5", {"start": v(54.4, 37.55) * mm, "end": v(56.75, 39.26) * mm});
            skLineSegment(sketch, "E7.52.0", {"start": v(48.04, 45.4) * mm, "end": v(50.2, 47.35) * mm});
            skArc(sketch, "E7.52.1", {"start": v(49.34, 46.58) * mm, "mid": v(50.78, 47.7) * mm, "end": v(52.54, 48.2) * mm});
            skLineSegment(sketch, "E7.52.2", {"start": v(52.99, 47.7) * mm, "end": v(52.54, 48.2) * mm});
            skLineSegment(sketch, "E7.52.3", {"start": v(52.99, 47.7) * mm, "end": v(53.42, 47.22) * mm});
            skArc(sketch, "E7.52.4", {"start": v(51.48, 44.2) * mm, "mid": v(52.75, 45.52) * mm, "end": v(53.42, 47.22) * mm});
            skLineSegment(sketch, "E7.52.5", {"start": v(50.18, 43.03) * mm, "end": v(52.34, 44.97) * mm});
            skLineSegment(sketch, "E7.53.0", {"start": v(43.03, 50.18) * mm, "end": v(44.97, 52.34) * mm});
            skArc(sketch, "E7.53.1", {"start": v(44.2, 51.48) * mm, "mid": v(45.52, 52.75) * mm, "end": v(47.22, 53.42) * mm});
            skLineSegment(sketch, "E7.53.2", {"start": v(47.7, 52.99) * mm, "end": v(47.22, 53.42) * mm});
            skLineSegment(sketch, "E7.53.3", {"start": v(47.7, 52.99) * mm, "end": v(48.2, 52.54) * mm});
            skArc(sketch, "E7.53.4", {"start": v(46.58, 49.34) * mm, "mid": v(47.7, 50.78) * mm, "end": v(48.2, 52.54) * mm});
            skLineSegment(sketch, "E7.53.5", {"start": v(45.4, 48.04) * mm, "end": v(47.35, 50.2) * mm});
            skLineSegment(sketch, "E7.54.0", {"start": v(37.55, 54.4) * mm, "end": v(39.26, 56.75) * mm});
            skArc(sketch, "E7.54.1", {"start": v(38.58, 55.82) * mm, "mid": v(39.75, 57.22) * mm, "end": v(41.38, 58.07) * mm});
            skLineSegment(sketch, "E7.54.2", {"start": v(41.9, 57.68) * mm, "end": v(41.38, 58.07) * mm});
            skLineSegment(sketch, "E7.54.3", {"start": v(41.9, 57.68) * mm, "end": v(42.44, 57.3) * mm});
            skArc(sketch, "E7.54.4", {"start": v(41.16, 53.94) * mm, "mid": v(42.13, 55.49) * mm, "end": v(42.44, 57.3) * mm});
            skLineSegment(sketch, "E7.54.5", {"start": v(40.14, 52.52) * mm, "end": v(41.85, 54.87) * mm});
            skLineSegment(sketch, "E7.55.0", {"start": v(31.65, 58.03) * mm, "end": v(33.1, 60.55) * mm});
            skArc(sketch, "E7.55.1", {"start": v(32.53, 59.54) * mm, "mid": v(33.56, 61.06) * mm, "end": v(35.08, 62.07) * mm});
            skLineSegment(sketch, "E7.55.2", {"start": v(35.65, 61.75) * mm, "end": v(35.08, 62.07) * mm});
            skLineSegment(sketch, "E7.55.3", {"start": v(35.65, 61.75) * mm, "end": v(36.22, 61.42) * mm});
            skArc(sketch, "E7.55.4", {"start": v(35.3, 57.94) * mm, "mid": v(36.1, 59.59) * mm, "end": v(36.22, 61.42) * mm});
            skLineSegment(sketch, "E7.55.5", {"start": v(34.43, 56.43) * mm, "end": v(35.88, 58.95) * mm});
            skLineSegment(sketch, "E7.56.0", {"start": v(25.42, 61.02) * mm, "end": v(26.6, 63.68) * mm});
            skArc(sketch, "E7.56.1", {"start": v(26.13, 62.62) * mm, "mid": v(26.99, 64.23) * mm, "end": v(28.4, 65.4) * mm});
            skLineSegment(sketch, "E7.56.2", {"start": v(29, 65.14) * mm, "end": v(28.4, 65.4) * mm});
            skLineSegment(sketch, "E7.56.3", {"start": v(29, 65.14) * mm, "end": v(29.6, 64.87) * mm});
            skArc(sketch, "E7.56.4", {"start": v(29.05, 61.32) * mm, "mid": v(29.67, 63.04) * mm, "end": v(29.6, 64.87) * mm});
            skLineSegment(sketch, "E7.56.5", {"start": v(28.34, 59.72) * mm, "end": v(29.52, 62.37) * mm});
            skLineSegment(sketch, "E7.57.0", {"start": v(18.9, 63.34) * mm, "end": v(19.8, 66.1) * mm});
            skArc(sketch, "E7.57.1", {"start": v(19.44, 65) * mm, "mid": v(20.13, 66.7) * mm, "end": v(21.4, 68.01) * mm});
            skLineSegment(sketch, "E7.57.2", {"start": v(22.03, 67.81) * mm, "end": v(21.4, 68.01) * mm});
            skLineSegment(sketch, "E7.57.3", {"start": v(22.03, 67.81) * mm, "end": v(22.66, 67.6) * mm});
            skArc(sketch, "E7.57.4", {"start": v(22.48, 64.02) * mm, "mid": v(22.92, 65.8) * mm, "end": v(22.66, 67.6) * mm});
            skLineSegment(sketch, "E7.57.5", {"start": v(21.94, 62.35) * mm, "end": v(22.84, 65.12) * mm});
            skLineSegment(sketch, "E7.58.0", {"start": v(12.17, 64.97) * mm, "end": v(12.78, 67.81) * mm});
            skArc(sketch, "E7.58.1", {"start": v(12.54, 66.68) * mm, "mid": v(13.05, 68.44) * mm, "end": v(14.18, 69.88) * mm});
            skLineSegment(sketch, "E7.58.2", {"start": v(14.82, 69.74) * mm, "end": v(14.18, 69.88) * mm});
            skLineSegment(sketch, "E7.58.3", {"start": v(14.82, 69.74) * mm, "end": v(15.47, 69.6) * mm});
            skArc(sketch, "E7.58.4", {"start": v(15.67, 66.02) * mm, "mid": v(15.92, 67.83) * mm, "end": v(15.47, 69.6) * mm});
            skLineSegment(sketch, "E7.58.5", {"start": v(15.3, 64.3) * mm, "end": v(15.9, 67.15) * mm});
            skLineSegment(sketch, "E7.59.0", {"start": v(5.32, 65.89) * mm, "end": v(5.62, 68.78) * mm});
            skArc(sketch, "E7.59.1", {"start": v(5.5, 67.63) * mm, "mid": v(5.82, 69.43) * mm, "end": v(6.8, 70.98) * mm});
            skLineSegment(sketch, "E7.59.2", {"start": v(7.45, 70.9) * mm, "end": v(6.8, 70.98) * mm});
            skLineSegment(sketch, "E7.59.3", {"start": v(7.45, 70.9) * mm, "end": v(8.1, 70.84) * mm});
            skArc(sketch, "E7.59.4", {"start": v(8.68, 67.3) * mm, "mid": v(8.74, 69.12) * mm, "end": v(8.1, 70.84) * mm});
            skLineSegment(sketch, "E7.59.5", {"start": v(8.5, 65.55) * mm, "end": v(8.8, 68.44) * mm});
            skArc(sketch, "E8", {"start": v(-57.63, 13.1) * mm, "mid": v(-41.8, 41.8) * mm, "end": v(-13.1, 57.63) * mm});
            skLineSegment(sketch, "E9", {"start": v(-52.75, 7) * mm, "end": v(-12, 7) * mm});
            skLineSegment(sketch, "E10", {"start": v(-7, 12) * mm, "end": v(-7, 52.75) * mm});
            skPoint(sketch, "E11.visualSharp", {"position": v(-7, 58.68) * mm});
            skArc(sketch, "E11.filletArc", {"start": v(-7, 52.75) * mm, "mid": v(-8.88, 56.66) * mm, "end": v(-13.1, 57.63) * mm});
            skPoint(sketch, "E12.visualSharp", {"position": v(-58.68, 7) * mm});
            skArc(sketch, "E12.filletArc", {"start": v(-57.63, 13.1) * mm, "mid": v(-56.66, 8.88) * mm, "end": v(-52.75, 7) * mm});
            skPoint(sketch, "E13.visualSharp", {"position": v(-7, 7) * mm});
            skArc(sketch, "E13.filletArc", {"start": v(-12, 7) * mm, "mid": v(-8.46, 8.46) * mm, "end": v(-7, 12) * mm});
            skLineSegment(sketch, "E14.MirrorCS", {"start": v(7, 12) * mm, "end": v(7, 52.75) * mm});
            skArc(sketch, "E15.MirrorCS", {"start": v(7, 52.75) * mm, "mid": v(8.88, 56.66) * mm, "end": v(13.1, 57.63) * mm});
            skArc(sketch, "E16.MirrorCS", {"start": v(57.63, 13.1) * mm, "mid": v(41.8, 41.8) * mm, "end": v(13.1, 57.63) * mm});
            skArc(sketch, "E17.MirrorCS", {"start": v(57.63, 13.1) * mm, "mid": v(56.66, 8.88) * mm, "end": v(52.75, 7) * mm});
            skLineSegment(sketch, "E18.MirrorCS", {"start": v(52.75, 7) * mm, "end": v(12, 7) * mm});
            skArc(sketch, "E19.MirrorCS", {"start": v(12, 7) * mm, "mid": v(8.46, 8.46) * mm, "end": v(7, 12) * mm});
            skArc(sketch, "E20.MirrorCS", {"start": v(12, -7) * mm, "mid": v(8.46, -8.46) * mm, "end": v(7, -12) * mm});
            skLineSegment(sketch, "E21.MirrorCS", {"start": v(7, -12) * mm, "end": v(7, -52.75) * mm});
            skArc(sketch, "E22.MirrorCS", {"start": v(7, -52.75) * mm, "mid": v(8.88, -56.66) * mm, "end": v(13.1, -57.63) * mm});
            skArc(sketch, "E23.MirrorCS", {"start": v(57.63, -13.1) * mm, "mid": v(41.8, -41.8) * mm, "end": v(13.1, -57.63) * mm});
            skArc(sketch, "E24.MirrorCS", {"start": v(57.63, -13.1) * mm, "mid": v(56.66, -8.88) * mm, "end": v(52.75, -7) * mm});
            skLineSegment(sketch, "E25.MirrorCS", {"start": v(52.75, -7) * mm, "end": v(12, -7) * mm});
            skPoint(sketch, "E26.MirrorP", {"position": v(-7, -58.68) * mm});
            skLineSegment(sketch, "E27.MirrorCS", {"start": v(-7, -12) * mm, "end": v(-7, -52.75) * mm});
            skArc(sketch, "E28.MirrorCS", {"start": v(-57.63, -13.1) * mm, "mid": v(-56.66, -8.88) * mm, "end": v(-52.75, -7) * mm});
            skLineSegment(sketch, "E29.MirrorCS", {"start": v(-52.75, -7) * mm, "end": v(-12, -7) * mm});
            skArc(sketch, "E30.MirrorCS", {"start": v(-57.63, -13.1) * mm, "mid": v(-41.8, -41.8) * mm, "end": v(-13.1, -57.63) * mm});
            skArc(sketch, "E31.MirrorCS", {"start": v(-7, -52.75) * mm, "mid": v(-8.88, -56.66) * mm, "end": v(-13.1, -57.63) * mm});
            skArc(sketch, "E32.MirrorCS", {"start": v(-12, -7) * mm, "mid": v(-8.46, -8.46) * mm, "end": v(-7, -12) * mm});
            skLineSegment(sketch, "E33", {"start": v(-5.32, 65.89) * mm, "end": v(-1.6, 66.08) * mm});
            skLineSegment(sketch, "E34.1.0", {"start": v(-12.17, 64.97) * mm, "end": v(-8.5, 65.55) * mm});
            skLineSegment(sketch, "E34.2.0", {"start": v(-18.9, 63.34) * mm, "end": v(-15.3, 64.3) * mm});
            skLineSegment(sketch, "E34.3.0", {"start": v(-25.42, 61.02) * mm, "end": v(-21.94, 62.35) * mm});
            skLineSegment(sketch, "E34.4.0", {"start": v(-31.65, 58.03) * mm, "end": v(-28.34, 59.72) * mm});
            skLineSegment(sketch, "E34.5.0", {"start": v(-37.55, 54.4) * mm, "end": v(-34.43, 56.43) * mm});
            skLineSegment(sketch, "E34.6.0", {"start": v(-43.03, 50.18) * mm, "end": v(-40.14, 52.52) * mm});
            skLineSegment(sketch, "E34.7.0", {"start": v(-48.04, 45.4) * mm, "end": v(-45.4, 48.04) * mm});
            skLineSegment(sketch, "E34.8.0", {"start": v(-52.52, 40.14) * mm, "end": v(-50.18, 43.03) * mm});
            skLineSegment(sketch, "E34.9.0", {"start": v(-56.43, 34.43) * mm, "end": v(-54.4, 37.55) * mm});
            skLineSegment(sketch, "E34.10.0", {"start": v(-59.72, 28.34) * mm, "end": v(-58.03, 31.65) * mm});
            skLineSegment(sketch, "E34.11.0", {"start": v(-62.35, 21.94) * mm, "end": v(-61.02, 25.42) * mm});
            skLineSegment(sketch, "E34.12.0", {"start": v(-64.3, 15.3) * mm, "end": v(-63.34, 18.9) * mm});
            skLineSegment(sketch, "E34.13.0", {"start": v(-65.55, 8.5) * mm, "end": v(-64.97, 12.17) * mm});
            skLineSegment(sketch, "E34.14.0", {"start": v(-66.08, 1.6) * mm, "end": v(-65.89, 5.32) * mm});
            skLineSegment(sketch, "E34.15.0", {"start": v(-65.89, -5.32) * mm, "end": v(-66.08, -1.6) * mm});
            skLineSegment(sketch, "E34.16.0", {"start": v(-64.97, -12.17) * mm, "end": v(-65.55, -8.5) * mm});
            skLineSegment(sketch, "E34.17.0", {"start": v(-63.34, -18.9) * mm, "end": v(-64.3, -15.3) * mm});
            skLineSegment(sketch, "E34.18.0", {"start": v(-61.02, -25.42) * mm, "end": v(-62.35, -21.94) * mm});
            skLineSegment(sketch, "E34.19.0", {"start": v(-58.03, -31.65) * mm, "end": v(-59.72, -28.34) * mm});
            skLineSegment(sketch, "E34.20.0", {"start": v(-54.4, -37.55) * mm, "end": v(-56.43, -34.43) * mm});
            skLineSegment(sketch, "E34.21.0", {"start": v(-50.18, -43.03) * mm, "end": v(-52.52, -40.14) * mm});
            skLineSegment(sketch, "E34.22.0", {"start": v(-45.4, -48.04) * mm, "end": v(-48.04, -45.4) * mm});
            skLineSegment(sketch, "E34.23.0", {"start": v(-40.14, -52.52) * mm, "end": v(-43.03, -50.18) * mm});
            skLineSegment(sketch, "E34.24.0", {"start": v(-34.43, -56.43) * mm, "end": v(-37.55, -54.4) * mm});
            skLineSegment(sketch, "E34.25.0", {"start": v(-28.34, -59.72) * mm, "end": v(-31.65, -58.03) * mm});
            skLineSegment(sketch, "E34.26.0", {"start": v(-21.94, -62.35) * mm, "end": v(-25.42, -61.02) * mm});
            skLineSegment(sketch, "E34.27.0", {"start": v(-15.3, -64.3) * mm, "end": v(-18.9, -63.34) * mm});
            skLineSegment(sketch, "E34.28.0", {"start": v(-8.5, -65.55) * mm, "end": v(-12.17, -64.97) * mm});
            skLineSegment(sketch, "E34.29.0", {"start": v(-1.6, -66.08) * mm, "end": v(-5.32, -65.89) * mm});
            skLineSegment(sketch, "E34.30.0", {"start": v(5.32, -65.89) * mm, "end": v(1.6, -66.08) * mm});
            skLineSegment(sketch, "E34.31.0", {"start": v(12.17, -64.97) * mm, "end": v(8.5, -65.55) * mm});
            skLineSegment(sketch, "E34.32.0", {"start": v(18.9, -63.34) * mm, "end": v(15.3, -64.3) * mm});
            skLineSegment(sketch, "E34.33.0", {"start": v(25.42, -61.02) * mm, "end": v(21.94, -62.35) * mm});
            skLineSegment(sketch, "E34.34.0", {"start": v(31.65, -58.03) * mm, "end": v(28.34, -59.72) * mm});
            skLineSegment(sketch, "E34.35.0", {"start": v(37.55, -54.4) * mm, "end": v(34.43, -56.43) * mm});
            skLineSegment(sketch, "E34.36.0", {"start": v(43.03, -50.18) * mm, "end": v(40.14, -52.52) * mm});
            skLineSegment(sketch, "E34.37.0", {"start": v(48.04, -45.4) * mm, "end": v(45.4, -48.04) * mm});
            skLineSegment(sketch, "E34.38.0", {"start": v(52.52, -40.14) * mm, "end": v(50.18, -43.03) * mm});
            skLineSegment(sketch, "E34.39.0", {"start": v(56.43, -34.43) * mm, "end": v(54.4, -37.55) * mm});
            skLineSegment(sketch, "E34.40.0", {"start": v(59.72, -28.34) * mm, "end": v(58.03, -31.65) * mm});
            skLineSegment(sketch, "E34.41.0", {"start": v(62.35, -21.94) * mm, "end": v(61.02, -25.42) * mm});
            skLineSegment(sketch, "E34.42.0", {"start": v(64.3, -15.3) * mm, "end": v(63.34, -18.9) * mm});
            skLineSegment(sketch, "E34.43.0", {"start": v(65.55, -8.5) * mm, "end": v(64.97, -12.17) * mm});
            skLineSegment(sketch, "E34.44.0", {"start": v(66.08, -1.6) * mm, "end": v(65.89, -5.32) * mm});
            skLineSegment(sketch, "E34.45.0", {"start": v(65.89, 5.32) * mm, "end": v(66.08, 1.6) * mm});
            skLineSegment(sketch, "E34.46.0", {"start": v(64.97, 12.17) * mm, "end": v(65.55, 8.5) * mm});
            skLineSegment(sketch, "E34.47.0", {"start": v(63.34, 18.9) * mm, "end": v(64.3, 15.3) * mm});
            skLineSegment(sketch, "E34.48.0", {"start": v(61.02, 25.42) * mm, "end": v(62.35, 21.94) * mm});
            skLineSegment(sketch, "E34.49.0", {"start": v(58.03, 31.65) * mm, "end": v(59.72, 28.34) * mm});
            skLineSegment(sketch, "E34.50.0", {"start": v(54.4, 37.55) * mm, "end": v(56.43, 34.43) * mm});
            skLineSegment(sketch, "E34.51.0", {"start": v(50.18, 43.03) * mm, "end": v(52.52, 40.14) * mm});
            skLineSegment(sketch, "E34.52.0", {"start": v(45.4, 48.04) * mm, "end": v(48.04, 45.4) * mm});
            skLineSegment(sketch, "E34.53.0", {"start": v(40.14, 52.52) * mm, "end": v(43.03, 50.18) * mm});
            skLineSegment(sketch, "E34.54.0", {"start": v(34.43, 56.43) * mm, "end": v(37.55, 54.4) * mm});
            skLineSegment(sketch, "E34.55.0", {"start": v(28.34, 59.72) * mm, "end": v(31.65, 58.03) * mm});
            skLineSegment(sketch, "E34.56.0", {"start": v(21.94, 62.35) * mm, "end": v(25.42, 61.02) * mm});
            skLineSegment(sketch, "E34.57.0", {"start": v(15.3, 64.3) * mm, "end": v(18.9, 63.34) * mm});
            skLineSegment(sketch, "E34.58.0", {"start": v(8.5, 65.55) * mm, "end": v(12.17, 64.97) * mm});
            skLineSegment(sketch, "E34.59.0", {"start": v(1.6, 66.08) * mm, "end": v(5.32, 65.89) * mm});
            skSolve(sketch);
        }
        {
            var Q0;
            Q0=makeQuery(id+"F0.imprint","IMPRINT",FACE,{"disambiguationData":[TD([[makeQuery(id+"F0.imprint","IMPRINT",EDGE,{"derivedFrom":sQuery(id+"F0.wireOp",EDGE,"E0")}),-1.0]])]});
            extrude(context, id + "F1", {"entities" : qUnion([Q0]), "endBound" : BoundingType.SYMMETRIC, "depth" : 10 * mm});
        }
        {
            var Q0;
            Q0=makeQuery(id+"F1.opExtrude","SWEPT_BODY",BODY,{"disambiguationData":[OSD([sQuery(id+"F0.wireOp",EDGE,"E0"),sQuery(id+"F0.wireOp",EDGE,"E1"),sQuery(id+"F0.wireOp",EDGE,"E2"),sQuery(id+"F0.wireOp",EDGE,"E3"),sQuery(id+"F0.wireOp",EDGE,"E4.MirrorCS"),sQuery(id+"F0.wireOp",EDGE,"E5.MirrorCS"),sQuery(id+"F0.wireOp",EDGE,"E6.MirrorCS"),sQuery(id+"F0.wireOp",EDGE,"E7.1.0"),sQuery(id+"F0.wireOp",EDGE,"E7.1.1"),sQuery(id+"F0.wireOp",EDGE,"E7.1.2"),sQuery(id+"F0.wireOp",EDGE,"E7.1.3"),sQuery(id+"F0.wireOp",EDGE,"E7.1.4"),sQuery(id+"F0.wireOp",EDGE,"E7.1.5"),sQuery(id+"F0.wireOp",EDGE,"E7.2.0"),sQuery(id+"F0.wireOp",EDGE,"E7.2.1"),sQuery(id+"F0.wireOp",EDGE,"E7.2.2"),sQuery(id+"F0.wireOp",EDGE,"E7.2.3"),sQuery(id+"F0.wireOp",EDGE,"E7.2.4"),sQuery(id+"F0.wireOp",EDGE,"E7.2.5"),sQuery(id+"F0.wireOp",EDGE,"E7.3.0"),sQuery(id+"F0.wireOp",EDGE,"E7.3.1"),sQuery(id+"F0.wireOp",EDGE,"E7.3.2"),sQuery(id+"F0.wireOp",EDGE,"E7.3.3"),sQuery(id+"F0.wireOp",EDGE,"E7.3.4"),sQuery(id+"F0.wireOp",EDGE,"E7.3.5"),sQuery(id+"F0.wireOp",EDGE,"E7.4.0"),sQuery(id+"F0.wireOp",EDGE,"E7.4.1"),sQuery(id+"F0.wireOp",EDGE,"E7.4.2"),sQuery(id+"F0.wireOp",EDGE,"E7.4.3"),sQuery(id+"F0.wireOp",EDGE,"E7.4.4"),sQuery(id+"F0.wireOp",EDGE,"E7.4.5"),sQuery(id+"F0.wireOp",EDGE,"E7.5.0"),sQuery(id+"F0.wireOp",EDGE,"E7.5.1"),sQuery(id+"F0.wireOp",EDGE,"E7.5.2"),sQuery(id+"F0.wireOp",EDGE,"E7.5.3"),sQuery(id+"F0.wireOp",EDGE,"E7.5.4"),sQuery(id+"F0.wireOp",EDGE,"E7.5.5"),sQuery(id+"F0.wireOp",EDGE,"E7.6.0"),sQuery(id+"F0.wireOp",EDGE,"E7.6.1"),sQuery(id+"F0.wireOp",EDGE,"E7.6.2"),sQuery(id+"F0.wireOp",EDGE,"E7.6.3"),sQuery(id+"F0.wireOp",EDGE,"E7.6.4"),sQuery(id+"F0.wireOp",EDGE,"E7.6.5"),sQuery(id+"F0.wireOp",EDGE,"E7.7.0"),sQuery(id+"F0.wireOp",EDGE,"E7.7.1"),sQuery(id+"F0.wireOp",EDGE,"E7.7.2"),sQuery(id+"F0.wireOp",EDGE,"E7.7.3"),sQuery(id+"F0.wireOp",EDGE,"E7.7.4"),sQuery(id+"F0.wireOp",EDGE,"E7.7.5"),sQuery(id+"F0.wireOp",EDGE,"E7.8.0"),sQuery(id+"F0.wireOp",EDGE,"E7.8.1"),sQuery(id+"F0.wireOp",EDGE,"E7.8.2"),sQuery(id+"F0.wireOp",EDGE,"E7.8.3"),sQuery(id+"F0.wireOp",EDGE,"E7.8.4"),sQuery(id+"F0.wireOp",EDGE,"E7.8.5"),sQuery(id+"F0.wireOp",EDGE,"E7.9.0"),sQuery(id+"F0.wireOp",EDGE,"E7.9.1"),sQuery(id+"F0.wireOp",EDGE,"E7.9.2"),sQuery(id+"F0.wireOp",EDGE,"E7.9.3"),sQuery(id+"F0.wireOp",EDGE,"E7.9.4"),sQuery(id+"F0.wireOp",EDGE,"E7.9.5"),sQuery(id+"F0.wireOp",EDGE,"E7.10.0"),sQuery(id+"F0.wireOp",EDGE,"E7.10.1"),sQuery(id+"F0.wireOp",EDGE,"E7.10.2"),sQuery(id+"F0.wireOp",EDGE,"E7.10.3"),sQuery(id+"F0.wireOp",EDGE,"E7.10.4"),sQuery(id+"F0.wireOp",EDGE,"E7.10.5"),sQuery(id+"F0.wireOp",EDGE,"E7.11.0"),sQuery(id+"F0.wireOp",EDGE,"E7.11.1"),sQuery(id+"F0.wireOp",EDGE,"E7.11.2"),sQuery(id+"F0.wireOp",EDGE,"E7.11.3"),sQuery(id+"F0.wireOp",EDGE,"E7.11.4"),sQuery(id+"F0.wireOp",EDGE,"E7.11.5"),sQuery(id+"F0.wireOp",EDGE,"E7.12.0"),sQuery(id+"F0.wireOp",EDGE,"E7.12.1"),sQuery(id+"F0.wireOp",EDGE,"E7.12.2"),sQuery(id+"F0.wireOp",EDGE,"E7.12.3"),sQuery(id+"F0.wireOp",EDGE,"E7.12.4"),sQuery(id+"F0.wireOp",EDGE,"E7.12.5"),sQuery(id+"F0.wireOp",EDGE,"E7.13.0"),sQuery(id+"F0.wireOp",EDGE,"E7.13.1"),sQuery(id+"F0.wireOp",EDGE,"E7.13.2"),sQuery(id+"F0.wireOp",EDGE,"E7.13.3"),sQuery(id+"F0.wireOp",EDGE,"E7.13.4"),sQuery(id+"F0.wireOp",EDGE,"E7.13.5"),sQuery(id+"F0.wireOp",EDGE,"E7.14.0"),sQuery(id+"F0.wireOp",EDGE,"E7.14.1"),sQuery(id+"F0.wireOp",EDGE,"E7.14.2"),sQuery(id+"F0.wireOp",EDGE,"E7.14.3"),sQuery(id+"F0.wireOp",EDGE,"E7.14.4"),sQuery(id+"F0.wireOp",EDGE,"E7.14.5"),sQuery(id+"F0.wireOp",EDGE,"E7.15.0"),sQuery(id+"F0.wireOp",EDGE,"E7.15.1"),sQuery(id+"F0.wireOp",EDGE,"E7.15.2"),sQuery(id+"F0.wireOp",EDGE,"E7.15.3"),sQuery(id+"F0.wireOp",EDGE,"E7.15.4"),sQuery(id+"F0.wireOp",EDGE,"E7.15.5"),sQuery(id+"F0.wireOp",EDGE,"E7.16.0"),sQuery(id+"F0.wireOp",EDGE,"E7.16.1"),sQuery(id+"F0.wireOp",EDGE,"E7.16.2"),sQuery(id+"F0.wireOp",EDGE,"E7.16.3"),sQuery(id+"F0.wireOp",EDGE,"E7.16.4"),sQuery(id+"F0.wireOp",EDGE,"E7.16.5"),sQuery(id+"F0.wireOp",EDGE,"E7.17.0"),sQuery(id+"F0.wireOp",EDGE,"E7.17.1"),sQuery(id+"F0.wireOp",EDGE,"E7.17.2"),sQuery(id+"F0.wireOp",EDGE,"E7.17.3"),sQuery(id+"F0.wireOp",EDGE,"E7.17.4"),sQuery(id+"F0.wireOp",EDGE,"E7.17.5"),sQuery(id+"F0.wireOp",EDGE,"E7.18.0"),sQuery(id+"F0.wireOp",EDGE,"E7.18.1"),sQuery(id+"F0.wireOp",EDGE,"E7.18.2"),sQuery(id+"F0.wireOp",EDGE,"E7.18.3"),sQuery(id+"F0.wireOp",EDGE,"E7.18.4"),sQuery(id+"F0.wireOp",EDGE,"E7.18.5"),sQuery(id+"F0.wireOp",EDGE,"E7.19.0"),sQuery(id+"F0.wireOp",EDGE,"E7.19.1"),sQuery(id+"F0.wireOp",EDGE,"E7.19.2"),sQuery(id+"F0.wireOp",EDGE,"E7.19.3"),sQuery(id+"F0.wireOp",EDGE,"E7.19.4"),sQuery(id+"F0.wireOp",EDGE,"E7.19.5"),sQuery(id+"F0.wireOp",EDGE,"E7.20.0"),sQuery(id+"F0.wireOp",EDGE,"E7.20.1"),sQuery(id+"F0.wireOp",EDGE,"E7.20.2"),sQuery(id+"F0.wireOp",EDGE,"E7.20.3"),sQuery(id+"F0.wireOp",EDGE,"E7.20.4"),sQuery(id+"F0.wireOp",EDGE,"E7.20.5"),sQuery(id+"F0.wireOp",EDGE,"E7.21.0"),sQuery(id+"F0.wireOp",EDGE,"E7.21.1"),sQuery(id+"F0.wireOp",EDGE,"E7.21.2"),sQuery(id+"F0.wireOp",EDGE,"E7.21.3"),sQuery(id+"F0.wireOp",EDGE,"E7.21.4"),sQuery(id+"F0.wireOp",EDGE,"E7.21.5"),sQuery(id+"F0.wireOp",EDGE,"E7.22.0"),sQuery(id+"F0.wireOp",EDGE,"E7.22.1"),sQuery(id+"F0.wireOp",EDGE,"E7.22.2"),sQuery(id+"F0.wireOp",EDGE,"E7.22.3"),sQuery(id+"F0.wireOp",EDGE,"E7.22.4"),sQuery(id+"F0.wireOp",EDGE,"E7.22.5"),sQuery(id+"F0.wireOp",EDGE,"E7.23.0"),sQuery(id+"F0.wireOp",EDGE,"E7.23.1"),sQuery(id+"F0.wireOp",EDGE,"E7.23.2"),sQuery(id+"F0.wireOp",EDGE,"E7.23.3"),sQuery(id+"F0.wireOp",EDGE,"E7.23.4"),sQuery(id+"F0.wireOp",EDGE,"E7.23.5"),sQuery(id+"F0.wireOp",EDGE,"E7.24.0"),sQuery(id+"F0.wireOp",EDGE,"E7.24.1"),sQuery(id+"F0.wireOp",EDGE,"E7.24.2"),sQuery(id+"F0.wireOp",EDGE,"E7.24.3"),sQuery(id+"F0.wireOp",EDGE,"E7.24.4"),sQuery(id+"F0.wireOp",EDGE,"E7.24.5"),sQuery(id+"F0.wireOp",EDGE,"E7.25.0"),sQuery(id+"F0.wireOp",EDGE,"E7.25.1"),sQuery(id+"F0.wireOp",EDGE,"E7.25.2"),sQuery(id+"F0.wireOp",EDGE,"E7.25.3"),sQuery(id+"F0.wireOp",EDGE,"E7.25.4"),sQuery(id+"F0.wireOp",EDGE,"E7.25.5"),sQuery(id+"F0.wireOp",EDGE,"E7.26.0"),sQuery(id+"F0.wireOp",EDGE,"E7.26.1"),sQuery(id+"F0.wireOp",EDGE,"E7.26.2"),sQuery(id+"F0.wireOp",EDGE,"E7.26.3"),sQuery(id+"F0.wireOp",EDGE,"E7.26.4"),sQuery(id+"F0.wireOp",EDGE,"E7.26.5"),sQuery(id+"F0.wireOp",EDGE,"E7.27.0"),sQuery(id+"F0.wireOp",EDGE,"E7.27.1"),sQuery(id+"F0.wireOp",EDGE,"E7.27.2"),sQuery(id+"F0.wireOp",EDGE,"E7.27.3"),sQuery(id+"F0.wireOp",EDGE,"E7.27.4"),sQuery(id+"F0.wireOp",EDGE,"E7.27.5"),sQuery(id+"F0.wireOp",EDGE,"E7.28.0"),sQuery(id+"F0.wireOp",EDGE,"E7.28.1"),sQuery(id+"F0.wireOp",EDGE,"E7.28.2"),sQuery(id+"F0.wireOp",EDGE,"E7.28.3"),sQuery(id+"F0.wireOp",EDGE,"E7.28.4"),sQuery(id+"F0.wireOp",EDGE,"E7.28.5"),sQuery(id+"F0.wireOp",EDGE,"E7.29.0"),sQuery(id+"F0.wireOp",EDGE,"E7.29.1"),sQuery(id+"F0.wireOp",EDGE,"E7.29.2"),sQuery(id+"F0.wireOp",EDGE,"E7.29.3"),sQuery(id+"F0.wireOp",EDGE,"E7.29.4"),sQuery(id+"F0.wireOp",EDGE,"E7.29.5"),sQuery(id+"F0.wireOp",EDGE,"E7.30.0"),sQuery(id+"F0.wireOp",EDGE,"E7.30.1"),sQuery(id+"F0.wireOp",EDGE,"E7.30.2"),sQuery(id+"F0.wireOp",EDGE,"E7.30.3"),sQuery(id+"F0.wireOp",EDGE,"E7.30.4"),sQuery(id+"F0.wireOp",EDGE,"E7.30.5"),sQuery(id+"F0.wireOp",EDGE,"E7.31.0"),sQuery(id+"F0.wireOp",EDGE,"E7.31.1"),sQuery(id+"F0.wireOp",EDGE,"E7.31.2"),sQuery(id+"F0.wireOp",EDGE,"E7.31.3"),sQuery(id+"F0.wireOp",EDGE,"E7.31.4"),sQuery(id+"F0.wireOp",EDGE,"E7.31.5"),sQuery(id+"F0.wireOp",EDGE,"E7.32.0"),sQuery(id+"F0.wireOp",EDGE,"E7.32.1"),sQuery(id+"F0.wireOp",EDGE,"E7.32.2"),sQuery(id+"F0.wireOp",EDGE,"E7.32.3"),sQuery(id+"F0.wireOp",EDGE,"E7.32.4"),sQuery(id+"F0.wireOp",EDGE,"E7.32.5"),sQuery(id+"F0.wireOp",EDGE,"E7.33.0"),sQuery(id+"F0.wireOp",EDGE,"E7.33.1"),sQuery(id+"F0.wireOp",EDGE,"E7.33.2"),sQuery(id+"F0.wireOp",EDGE,"E7.33.3"),sQuery(id+"F0.wireOp",EDGE,"E7.33.4"),sQuery(id+"F0.wireOp",EDGE,"E7.33.5"),sQuery(id+"F0.wireOp",EDGE,"E7.34.0"),sQuery(id+"F0.wireOp",EDGE,"E7.34.1"),sQuery(id+"F0.wireOp",EDGE,"E7.34.2"),sQuery(id+"F0.wireOp",EDGE,"E7.34.3"),sQuery(id+"F0.wireOp",EDGE,"E7.34.4"),sQuery(id+"F0.wireOp",EDGE,"E7.34.5"),sQuery(id+"F0.wireOp",EDGE,"E7.35.0"),sQuery(id+"F0.wireOp",EDGE,"E7.35.1"),sQuery(id+"F0.wireOp",EDGE,"E7.35.2"),sQuery(id+"F0.wireOp",EDGE,"E7.35.3"),sQuery(id+"F0.wireOp",EDGE,"E7.35.4"),sQuery(id+"F0.wireOp",EDGE,"E7.35.5"),sQuery(id+"F0.wireOp",EDGE,"E7.36.0"),sQuery(id+"F0.wireOp",EDGE,"E7.36.1"),sQuery(id+"F0.wireOp",EDGE,"E7.36.2"),sQuery(id+"F0.wireOp",EDGE,"E7.36.3"),sQuery(id+"F0.wireOp",EDGE,"E7.36.4"),sQuery(id+"F0.wireOp",EDGE,"E7.36.5"),sQuery(id+"F0.wireOp",EDGE,"E7.37.0"),sQuery(id+"F0.wireOp",EDGE,"E7.37.1"),sQuery(id+"F0.wireOp",EDGE,"E7.37.2"),sQuery(id+"F0.wireOp",EDGE,"E7.37.3"),sQuery(id+"F0.wireOp",EDGE,"E7.37.4"),sQuery(id+"F0.wireOp",EDGE,"E7.37.5"),sQuery(id+"F0.wireOp",EDGE,"E7.38.0"),sQuery(id+"F0.wireOp",EDGE,"E7.38.1"),sQuery(id+"F0.wireOp",EDGE,"E7.38.2"),sQuery(id+"F0.wireOp",EDGE,"E7.38.3"),sQuery(id+"F0.wireOp",EDGE,"E7.38.4"),sQuery(id+"F0.wireOp",EDGE,"E7.38.5"),sQuery(id+"F0.wireOp",EDGE,"E7.39.0"),sQuery(id+"F0.wireOp",EDGE,"E7.39.1"),sQuery(id+"F0.wireOp",EDGE,"E7.39.2"),sQuery(id+"F0.wireOp",EDGE,"E7.39.3"),sQuery(id+"F0.wireOp",EDGE,"E7.39.4"),sQuery(id+"F0.wireOp",EDGE,"E7.39.5"),sQuery(id+"F0.wireOp",EDGE,"E7.40.0"),sQuery(id+"F0.wireOp",EDGE,"E7.40.1"),sQuery(id+"F0.wireOp",EDGE,"E7.40.2"),sQuery(id+"F0.wireOp",EDGE,"E7.40.3"),sQuery(id+"F0.wireOp",EDGE,"E7.40.4"),sQuery(id+"F0.wireOp",EDGE,"E7.40.5"),sQuery(id+"F0.wireOp",EDGE,"E7.41.0"),sQuery(id+"F0.wireOp",EDGE,"E7.41.1"),sQuery(id+"F0.wireOp",EDGE,"E7.41.2"),sQuery(id+"F0.wireOp",EDGE,"E7.41.3"),sQuery(id+"F0.wireOp",EDGE,"E7.41.4"),sQuery(id+"F0.wireOp",EDGE,"E7.41.5"),sQuery(id+"F0.wireOp",EDGE,"E7.42.0"),sQuery(id+"F0.wireOp",EDGE,"E7.42.1"),sQuery(id+"F0.wireOp",EDGE,"E7.42.2"),sQuery(id+"F0.wireOp",EDGE,"E7.42.3"),sQuery(id+"F0.wireOp",EDGE,"E7.42.4"),sQuery(id+"F0.wireOp",EDGE,"E7.42.5"),sQuery(id+"F0.wireOp",EDGE,"E7.43.0"),sQuery(id+"F0.wireOp",EDGE,"E7.43.1"),sQuery(id+"F0.wireOp",EDGE,"E7.43.2"),sQuery(id+"F0.wireOp",EDGE,"E7.43.3"),sQuery(id+"F0.wireOp",EDGE,"E7.43.4"),sQuery(id+"F0.wireOp",EDGE,"E7.43.5"),sQuery(id+"F0.wireOp",EDGE,"E7.44.0"),sQuery(id+"F0.wireOp",EDGE,"E7.44.1"),sQuery(id+"F0.wireOp",EDGE,"E7.44.2"),sQuery(id+"F0.wireOp",EDGE,"E7.44.3"),sQuery(id+"F0.wireOp",EDGE,"E7.44.4"),sQuery(id+"F0.wireOp",EDGE,"E7.44.5"),sQuery(id+"F0.wireOp",EDGE,"E7.45.0"),sQuery(id+"F0.wireOp",EDGE,"E7.45.1"),sQuery(id+"F0.wireOp",EDGE,"E7.45.2"),sQuery(id+"F0.wireOp",EDGE,"E7.45.3"),sQuery(id+"F0.wireOp",EDGE,"E7.45.4"),sQuery(id+"F0.wireOp",EDGE,"E7.45.5"),sQuery(id+"F0.wireOp",EDGE,"E7.46.0"),sQuery(id+"F0.wireOp",EDGE,"E7.46.1"),sQuery(id+"F0.wireOp",EDGE,"E7.46.2"),sQuery(id+"F0.wireOp",EDGE,"E7.46.3"),sQuery(id+"F0.wireOp",EDGE,"E7.46.4"),sQuery(id+"F0.wireOp",EDGE,"E7.46.5"),sQuery(id+"F0.wireOp",EDGE,"E7.47.0"),sQuery(id+"F0.wireOp",EDGE,"E7.47.1"),sQuery(id+"F0.wireOp",EDGE,"E7.47.2"),sQuery(id+"F0.wireOp",EDGE,"E7.47.3"),sQuery(id+"F0.wireOp",EDGE,"E7.47.4"),sQuery(id+"F0.wireOp",EDGE,"E7.47.5"),sQuery(id+"F0.wireOp",EDGE,"E7.48.0"),sQuery(id+"F0.wireOp",EDGE,"E7.48.1"),sQuery(id+"F0.wireOp",EDGE,"E7.48.2"),sQuery(id+"F0.wireOp",EDGE,"E7.48.3"),sQuery(id+"F0.wireOp",EDGE,"E7.48.4"),sQuery(id+"F0.wireOp",EDGE,"E7.48.5"),sQuery(id+"F0.wireOp",EDGE,"E7.49.0"),sQuery(id+"F0.wireOp",EDGE,"E7.49.1"),sQuery(id+"F0.wireOp",EDGE,"E7.49.2"),sQuery(id+"F0.wireOp",EDGE,"E7.49.3"),sQuery(id+"F0.wireOp",EDGE,"E7.49.4"),sQuery(id+"F0.wireOp",EDGE,"E7.49.5"),sQuery(id+"F0.wireOp",EDGE,"E7.50.0"),sQuery(id+"F0.wireOp",EDGE,"E7.50.1"),sQuery(id+"F0.wireOp",EDGE,"E7.50.2"),sQuery(id+"F0.wireOp",EDGE,"E7.50.3"),sQuery(id+"F0.wireOp",EDGE,"E7.50.4"),sQuery(id+"F0.wireOp",EDGE,"E7.50.5"),sQuery(id+"F0.wireOp",EDGE,"E7.51.0"),sQuery(id+"F0.wireOp",EDGE,"E7.51.1"),sQuery(id+"F0.wireOp",EDGE,"E7.51.2"),sQuery(id+"F0.wireOp",EDGE,"E7.51.3"),sQuery(id+"F0.wireOp",EDGE,"E7.51.4"),sQuery(id+"F0.wireOp",EDGE,"E7.51.5"),sQuery(id+"F0.wireOp",EDGE,"E7.52.0"),sQuery(id+"F0.wireOp",EDGE,"E7.52.1"),sQuery(id+"F0.wireOp",EDGE,"E7.52.2"),sQuery(id+"F0.wireOp",EDGE,"E7.52.3"),sQuery(id+"F0.wireOp",EDGE,"E7.52.4"),sQuery(id+"F0.wireOp",EDGE,"E7.52.5"),sQuery(id+"F0.wireOp",EDGE,"E7.53.0"),sQuery(id+"F0.wireOp",EDGE,"E7.53.1"),sQuery(id+"F0.wireOp",EDGE,"E7.53.2"),sQuery(id+"F0.wireOp",EDGE,"E7.53.3"),sQuery(id+"F0.wireOp",EDGE,"E7.53.4"),sQuery(id+"F0.wireOp",EDGE,"E7.53.5"),sQuery(id+"F0.wireOp",EDGE,"E7.54.0"),sQuery(id+"F0.wireOp",EDGE,"E7.54.1"),sQuery(id+"F0.wireOp",EDGE,"E7.54.2"),sQuery(id+"F0.wireOp",EDGE,"E7.54.3"),sQuery(id+"F0.wireOp",EDGE,"E7.54.4"),sQuery(id+"F0.wireOp",EDGE,"E7.54.5"),sQuery(id+"F0.wireOp",EDGE,"E7.55.0"),sQuery(id+"F0.wireOp",EDGE,"E7.55.1"),sQuery(id+"F0.wireOp",EDGE,"E7.55.2"),sQuery(id+"F0.wireOp",EDGE,"E7.55.3"),sQuery(id+"F0.wireOp",EDGE,"E7.55.4"),sQuery(id+"F0.wireOp",EDGE,"E7.55.5"),sQuery(id+"F0.wireOp",EDGE,"E7.56.0"),sQuery(id+"F0.wireOp",EDGE,"E7.56.1"),sQuery(id+"F0.wireOp",EDGE,"E7.56.2"),sQuery(id+"F0.wireOp",EDGE,"E7.56.3"),sQuery(id+"F0.wireOp",EDGE,"E7.56.4"),sQuery(id+"F0.wireOp",EDGE,"E7.56.5"),sQuery(id+"F0.wireOp",EDGE,"E7.57.0"),sQuery(id+"F0.wireOp",EDGE,"E7.57.1"),sQuery(id+"F0.wireOp",EDGE,"E7.57.2"),sQuery(id+"F0.wireOp",EDGE,"E7.57.3"),sQuery(id+"F0.wireOp",EDGE,"E7.57.4"),sQuery(id+"F0.wireOp",EDGE,"E7.57.5"),sQuery(id+"F0.wireOp",EDGE,"E7.58.0"),sQuery(id+"F0.wireOp",EDGE,"E7.58.1"),sQuery(id+"F0.wireOp",EDGE,"E7.58.2"),sQuery(id+"F0.wireOp",EDGE,"E7.58.3"),sQuery(id+"F0.wireOp",EDGE,"E7.58.4"),sQuery(id+"F0.wireOp",EDGE,"E7.58.5"),sQuery(id+"F0.wireOp",EDGE,"E7.59.0"),sQuery(id+"F0.wireOp",EDGE,"E7.59.1"),sQuery(id+"F0.wireOp",EDGE,"E7.59.2"),sQuery(id+"F0.wireOp",EDGE,"E7.59.3"),sQuery(id+"F0.wireOp",EDGE,"E7.59.4"),sQuery(id+"F0.wireOp",EDGE,"E7.59.5"),sQuery(id+"F0.wireOp",EDGE,"E8"),sQuery(id+"F0.wireOp",EDGE,"E9"),sQuery(id+"F0.wireOp",EDGE,"E10"),sQuery(id+"F0.wireOp",EDGE,"E11.filletArc"),sQuery(id+"F0.wireOp",EDGE,"E12.filletArc"),sQuery(id+"F0.wireOp",EDGE,"E13.filletArc"),sQuery(id+"F0.wireOp",EDGE,"E14.MirrorCS"),sQuery(id+"F0.wireOp",EDGE,"E15.MirrorCS"),sQuery(id+"F0.wireOp",EDGE,"E16.MirrorCS"),sQuery(id+"F0.wireOp",EDGE,"E17.MirrorCS"),sQuery(id+"F0.wireOp",EDGE,"E18.MirrorCS"),sQuery(id+"F0.wireOp",EDGE,"E19.MirrorCS"),sQuery(id+"F0.wireOp",EDGE,"E21.MirrorCS"),sQuery(id+"F0.wireOp",EDGE,"E22.MirrorCS"),sQuery(id+"F0.wireOp",EDGE,"E23.MirrorCS"),sQuery(id+"F0.wireOp",EDGE,"E24.MirrorCS"),sQuery(id+"F0.wireOp",EDGE,"E25.MirrorCS"),sQuery(id+"F0.wireOp",EDGE,"E20.MirrorCS"),sQuery(id+"F0.wireOp",EDGE,"E27.MirrorCS"),sQuery(id+"F0.wireOp",EDGE,"E28.MirrorCS"),sQuery(id+"F0.wireOp",EDGE,"E29.MirrorCS"),sQuery(id+"F0.wireOp",EDGE,"E30.MirrorCS"),sQuery(id+"F0.wireOp",EDGE,"E31.MirrorCS"),sQuery(id+"F0.wireOp",EDGE,"E32.MirrorCS"),sQuery(id+"F0.wireOp",EDGE,"E33"),sQuery(id+"F0.wireOp",EDGE,"E34.1.0"),sQuery(id+"F0.wireOp",EDGE,"E34.2.0"),sQuery(id+"F0.wireOp",EDGE,"E34.3.0"),sQuery(id+"F0.wireOp",EDGE,"E34.4.0"),sQuery(id+"F0.wireOp",EDGE,"E34.5.0"),sQuery(id+"F0.wireOp",EDGE,"E34.6.0"),sQuery(id+"F0.wireOp",EDGE,"E34.7.0"),sQuery(id+"F0.wireOp",EDGE,"E34.8.0"),sQuery(id+"F0.wireOp",EDGE,"E34.9.0"),sQuery(id+"F0.wireOp",EDGE,"E34.10.0"),sQuery(id+"F0.wireOp",EDGE,"E34.11.0"),sQuery(id+"F0.wireOp",EDGE,"E34.12.0"),sQuery(id+"F0.wireOp",EDGE,"E34.13.0"),sQuery(id+"F0.wireOp",EDGE,"E34.14.0"),sQuery(id+"F0.wireOp",EDGE,"E34.15.0"),sQuery(id+"F0.wireOp",EDGE,"E34.16.0"),sQuery(id+"F0.wireOp",EDGE,"E34.17.0"),sQuery(id+"F0.wireOp",EDGE,"E34.18.0"),sQuery(id+"F0.wireOp",EDGE,"E34.19.0"),sQuery(id+"F0.wireOp",EDGE,"E34.20.0"),sQuery(id+"F0.wireOp",EDGE,"E34.21.0"),sQuery(id+"F0.wireOp",EDGE,"E34.22.0"),sQuery(id+"F0.wireOp",EDGE,"E34.23.0"),sQuery(id+"F0.wireOp",EDGE,"E34.24.0"),sQuery(id+"F0.wireOp",EDGE,"E34.25.0"),sQuery(id+"F0.wireOp",EDGE,"E34.26.0"),sQuery(id+"F0.wireOp",EDGE,"E34.27.0"),sQuery(id+"F0.wireOp",EDGE,"E34.28.0"),sQuery(id+"F0.wireOp",EDGE,"E34.29.0"),sQuery(id+"F0.wireOp",EDGE,"E34.30.0"),sQuery(id+"F0.wireOp",EDGE,"E34.31.0"),sQuery(id+"F0.wireOp",EDGE,"E34.32.0"),sQuery(id+"F0.wireOp",EDGE,"E34.33.0"),sQuery(id+"F0.wireOp",EDGE,"E34.34.0"),sQuery(id+"F0.wireOp",EDGE,"E34.35.0"),sQuery(id+"F0.wireOp",EDGE,"E34.36.0"),sQuery(id+"F0.wireOp",EDGE,"E34.37.0"),sQuery(id+"F0.wireOp",EDGE,"E34.38.0"),sQuery(id+"F0.wireOp",EDGE,"E34.39.0"),sQuery(id+"F0.wireOp",EDGE,"E34.40.0"),sQuery(id+"F0.wireOp",EDGE,"E34.41.0"),sQuery(id+"F0.wireOp",EDGE,"E34.42.0"),sQuery(id+"F0.wireOp",EDGE,"E34.43.0"),sQuery(id+"F0.wireOp",EDGE,"E34.44.0"),sQuery(id+"F0.wireOp",EDGE,"E34.45.0"),sQuery(id+"F0.wireOp",EDGE,"E34.46.0"),sQuery(id+"F0.wireOp",EDGE,"E34.47.0"),sQuery(id+"F0.wireOp",EDGE,"E34.48.0"),sQuery(id+"F0.wireOp",EDGE,"E34.49.0"),sQuery(id+"F0.wireOp",EDGE,"E34.50.0"),sQuery(id+"F0.wireOp",EDGE,"E34.51.0"),sQuery(id+"F0.wireOp",EDGE,"E34.52.0"),sQuery(id+"F0.wireOp",EDGE,"E34.53.0"),sQuery(id+"F0.wireOp",EDGE,"E34.54.0"),sQuery(id+"F0.wireOp",EDGE,"E34.55.0"),sQuery(id+"F0.wireOp",EDGE,"E34.56.0"),sQuery(id+"F0.wireOp",EDGE,"E34.57.0"),sQuery(id+"F0.wireOp",EDGE,"E34.58.0"),sQuery(id+"F0.wireOp",EDGE,"E34.59.0")])]});
            transform(context, id + "F2", {"entities" : qUnion([Q0]), "transformType" : TransformType.TRANSLATION_3D, "dx" : 0 * mm, "dy" : 0 * mm, "dz" : 0 * mm, "makeCopy" : true});
        }
        {
            var Q0;
            Q0=makeQuery(id+"F1.opExtrude","SWEPT_BODY",BODY,{"disambiguationData":[OSD([sQuery(id+"F0.wireOp",EDGE,"E0"),sQuery(id+"F0.wireOp",EDGE,"E1"),sQuery(id+"F0.wireOp",EDGE,"E2"),sQuery(id+"F0.wireOp",EDGE,"E3"),sQuery(id+"F0.wireOp",EDGE,"E4.MirrorCS"),sQuery(id+"F0.wireOp",EDGE,"E5.MirrorCS"),sQuery(id+"F0.wireOp",EDGE,"E6.MirrorCS"),sQuery(id+"F0.wireOp",EDGE,"E7.1.0"),sQuery(id+"F0.wireOp",EDGE,"E7.1.1"),sQuery(id+"F0.wireOp",EDGE,"E7.1.2"),sQuery(id+"F0.wireOp",EDGE,"E7.1.3"),sQuery(id+"F0.wireOp",EDGE,"E7.1.4"),sQuery(id+"F0.wireOp",EDGE,"E7.1.5"),sQuery(id+"F0.wireOp",EDGE,"E7.2.0"),sQuery(id+"F0.wireOp",EDGE,"E7.2.1"),sQuery(id+"F0.wireOp",EDGE,"E7.2.2"),sQuery(id+"F0.wireOp",EDGE,"E7.2.3"),sQuery(id+"F0.wireOp",EDGE,"E7.2.4"),sQuery(id+"F0.wireOp",EDGE,"E7.2.5"),sQuery(id+"F0.wireOp",EDGE,"E7.3.0"),sQuery(id+"F0.wireOp",EDGE,"E7.3.1"),sQuery(id+"F0.wireOp",EDGE,"E7.3.2"),sQuery(id+"F0.wireOp",EDGE,"E7.3.3"),sQuery(id+"F0.wireOp",EDGE,"E7.3.4"),sQuery(id+"F0.wireOp",EDGE,"E7.3.5"),sQuery(id+"F0.wireOp",EDGE,"E7.4.0"),sQuery(id+"F0.wireOp",EDGE,"E7.4.1"),sQuery(id+"F0.wireOp",EDGE,"E7.4.2"),sQuery(id+"F0.wireOp",EDGE,"E7.4.3"),sQuery(id+"F0.wireOp",EDGE,"E7.4.4"),sQuery(id+"F0.wireOp",EDGE,"E7.4.5"),sQuery(id+"F0.wireOp",EDGE,"E7.5.0"),sQuery(id+"F0.wireOp",EDGE,"E7.5.1"),sQuery(id+"F0.wireOp",EDGE,"E7.5.2"),sQuery(id+"F0.wireOp",EDGE,"E7.5.3"),sQuery(id+"F0.wireOp",EDGE,"E7.5.4"),sQuery(id+"F0.wireOp",EDGE,"E7.5.5"),sQuery(id+"F0.wireOp",EDGE,"E7.6.0"),sQuery(id+"F0.wireOp",EDGE,"E7.6.1"),sQuery(id+"F0.wireOp",EDGE,"E7.6.2"),sQuery(id+"F0.wireOp",EDGE,"E7.6.3"),sQuery(id+"F0.wireOp",EDGE,"E7.6.4"),sQuery(id+"F0.wireOp",EDGE,"E7.6.5"),sQuery(id+"F0.wireOp",EDGE,"E7.7.0"),sQuery(id+"F0.wireOp",EDGE,"E7.7.1"),sQuery(id+"F0.wireOp",EDGE,"E7.7.2"),sQuery(id+"F0.wireOp",EDGE,"E7.7.3"),sQuery(id+"F0.wireOp",EDGE,"E7.7.4"),sQuery(id+"F0.wireOp",EDGE,"E7.7.5"),sQuery(id+"F0.wireOp",EDGE,"E7.8.0"),sQuery(id+"F0.wireOp",EDGE,"E7.8.1"),sQuery(id+"F0.wireOp",EDGE,"E7.8.2"),sQuery(id+"F0.wireOp",EDGE,"E7.8.3"),sQuery(id+"F0.wireOp",EDGE,"E7.8.4"),sQuery(id+"F0.wireOp",EDGE,"E7.8.5"),sQuery(id+"F0.wireOp",EDGE,"E7.9.0"),sQuery(id+"F0.wireOp",EDGE,"E7.9.1"),sQuery(id+"F0.wireOp",EDGE,"E7.9.2"),sQuery(id+"F0.wireOp",EDGE,"E7.9.3"),sQuery(id+"F0.wireOp",EDGE,"E7.9.4"),sQuery(id+"F0.wireOp",EDGE,"E7.9.5"),sQuery(id+"F0.wireOp",EDGE,"E7.10.0"),sQuery(id+"F0.wireOp",EDGE,"E7.10.1"),sQuery(id+"F0.wireOp",EDGE,"E7.10.2"),sQuery(id+"F0.wireOp",EDGE,"E7.10.3"),sQuery(id+"F0.wireOp",EDGE,"E7.10.4"),sQuery(id+"F0.wireOp",EDGE,"E7.10.5"),sQuery(id+"F0.wireOp",EDGE,"E7.11.0"),sQuery(id+"F0.wireOp",EDGE,"E7.11.1"),sQuery(id+"F0.wireOp",EDGE,"E7.11.2"),sQuery(id+"F0.wireOp",EDGE,"E7.11.3"),sQuery(id+"F0.wireOp",EDGE,"E7.11.4"),sQuery(id+"F0.wireOp",EDGE,"E7.11.5"),sQuery(id+"F0.wireOp",EDGE,"E7.12.0"),sQuery(id+"F0.wireOp",EDGE,"E7.12.1"),sQuery(id+"F0.wireOp",EDGE,"E7.12.2"),sQuery(id+"F0.wireOp",EDGE,"E7.12.3"),sQuery(id+"F0.wireOp",EDGE,"E7.12.4"),sQuery(id+"F0.wireOp",EDGE,"E7.12.5"),sQuery(id+"F0.wireOp",EDGE,"E7.13.0"),sQuery(id+"F0.wireOp",EDGE,"E7.13.1"),sQuery(id+"F0.wireOp",EDGE,"E7.13.2"),sQuery(id+"F0.wireOp",EDGE,"E7.13.3"),sQuery(id+"F0.wireOp",EDGE,"E7.13.4"),sQuery(id+"F0.wireOp",EDGE,"E7.13.5"),sQuery(id+"F0.wireOp",EDGE,"E7.14.0"),sQuery(id+"F0.wireOp",EDGE,"E7.14.1"),sQuery(id+"F0.wireOp",EDGE,"E7.14.2"),sQuery(id+"F0.wireOp",EDGE,"E7.14.3"),sQuery(id+"F0.wireOp",EDGE,"E7.14.4"),sQuery(id+"F0.wireOp",EDGE,"E7.14.5"),sQuery(id+"F0.wireOp",EDGE,"E7.15.0"),sQuery(id+"F0.wireOp",EDGE,"E7.15.1"),sQuery(id+"F0.wireOp",EDGE,"E7.15.2"),sQuery(id+"F0.wireOp",EDGE,"E7.15.3"),sQuery(id+"F0.wireOp",EDGE,"E7.15.4"),sQuery(id+"F0.wireOp",EDGE,"E7.15.5"),sQuery(id+"F0.wireOp",EDGE,"E7.16.0"),sQuery(id+"F0.wireOp",EDGE,"E7.16.1"),sQuery(id+"F0.wireOp",EDGE,"E7.16.2"),sQuery(id+"F0.wireOp",EDGE,"E7.16.3"),sQuery(id+"F0.wireOp",EDGE,"E7.16.4"),sQuery(id+"F0.wireOp",EDGE,"E7.16.5"),sQuery(id+"F0.wireOp",EDGE,"E7.17.0"),sQuery(id+"F0.wireOp",EDGE,"E7.17.1"),sQuery(id+"F0.wireOp",EDGE,"E7.17.2"),sQuery(id+"F0.wireOp",EDGE,"E7.17.3"),sQuery(id+"F0.wireOp",EDGE,"E7.17.4"),sQuery(id+"F0.wireOp",EDGE,"E7.17.5"),sQuery(id+"F0.wireOp",EDGE,"E7.18.0"),sQuery(id+"F0.wireOp",EDGE,"E7.18.1"),sQuery(id+"F0.wireOp",EDGE,"E7.18.2"),sQuery(id+"F0.wireOp",EDGE,"E7.18.3"),sQuery(id+"F0.wireOp",EDGE,"E7.18.4"),sQuery(id+"F0.wireOp",EDGE,"E7.18.5"),sQuery(id+"F0.wireOp",EDGE,"E7.19.0"),sQuery(id+"F0.wireOp",EDGE,"E7.19.1"),sQuery(id+"F0.wireOp",EDGE,"E7.19.2"),sQuery(id+"F0.wireOp",EDGE,"E7.19.3"),sQuery(id+"F0.wireOp",EDGE,"E7.19.4"),sQuery(id+"F0.wireOp",EDGE,"E7.19.5"),sQuery(id+"F0.wireOp",EDGE,"E7.20.0"),sQuery(id+"F0.wireOp",EDGE,"E7.20.1"),sQuery(id+"F0.wireOp",EDGE,"E7.20.2"),sQuery(id+"F0.wireOp",EDGE,"E7.20.3"),sQuery(id+"F0.wireOp",EDGE,"E7.20.4"),sQuery(id+"F0.wireOp",EDGE,"E7.20.5"),sQuery(id+"F0.wireOp",EDGE,"E7.21.0"),sQuery(id+"F0.wireOp",EDGE,"E7.21.1"),sQuery(id+"F0.wireOp",EDGE,"E7.21.2"),sQuery(id+"F0.wireOp",EDGE,"E7.21.3"),sQuery(id+"F0.wireOp",EDGE,"E7.21.4"),sQuery(id+"F0.wireOp",EDGE,"E7.21.5"),sQuery(id+"F0.wireOp",EDGE,"E7.22.0"),sQuery(id+"F0.wireOp",EDGE,"E7.22.1"),sQuery(id+"F0.wireOp",EDGE,"E7.22.2"),sQuery(id+"F0.wireOp",EDGE,"E7.22.3"),sQuery(id+"F0.wireOp",EDGE,"E7.22.4"),sQuery(id+"F0.wireOp",EDGE,"E7.22.5"),sQuery(id+"F0.wireOp",EDGE,"E7.23.0"),sQuery(id+"F0.wireOp",EDGE,"E7.23.1"),sQuery(id+"F0.wireOp",EDGE,"E7.23.2"),sQuery(id+"F0.wireOp",EDGE,"E7.23.3"),sQuery(id+"F0.wireOp",EDGE,"E7.23.4"),sQuery(id+"F0.wireOp",EDGE,"E7.23.5"),sQuery(id+"F0.wireOp",EDGE,"E7.24.0"),sQuery(id+"F0.wireOp",EDGE,"E7.24.1"),sQuery(id+"F0.wireOp",EDGE,"E7.24.2"),sQuery(id+"F0.wireOp",EDGE,"E7.24.3"),sQuery(id+"F0.wireOp",EDGE,"E7.24.4"),sQuery(id+"F0.wireOp",EDGE,"E7.24.5"),sQuery(id+"F0.wireOp",EDGE,"E7.25.0"),sQuery(id+"F0.wireOp",EDGE,"E7.25.1"),sQuery(id+"F0.wireOp",EDGE,"E7.25.2"),sQuery(id+"F0.wireOp",EDGE,"E7.25.3"),sQuery(id+"F0.wireOp",EDGE,"E7.25.4"),sQuery(id+"F0.wireOp",EDGE,"E7.25.5"),sQuery(id+"F0.wireOp",EDGE,"E7.26.0"),sQuery(id+"F0.wireOp",EDGE,"E7.26.1"),sQuery(id+"F0.wireOp",EDGE,"E7.26.2"),sQuery(id+"F0.wireOp",EDGE,"E7.26.3"),sQuery(id+"F0.wireOp",EDGE,"E7.26.4"),sQuery(id+"F0.wireOp",EDGE,"E7.26.5"),sQuery(id+"F0.wireOp",EDGE,"E7.27.0"),sQuery(id+"F0.wireOp",EDGE,"E7.27.1"),sQuery(id+"F0.wireOp",EDGE,"E7.27.2"),sQuery(id+"F0.wireOp",EDGE,"E7.27.3"),sQuery(id+"F0.wireOp",EDGE,"E7.27.4"),sQuery(id+"F0.wireOp",EDGE,"E7.27.5"),sQuery(id+"F0.wireOp",EDGE,"E7.28.0"),sQuery(id+"F0.wireOp",EDGE,"E7.28.1"),sQuery(id+"F0.wireOp",EDGE,"E7.28.2"),sQuery(id+"F0.wireOp",EDGE,"E7.28.3"),sQuery(id+"F0.wireOp",EDGE,"E7.28.4"),sQuery(id+"F0.wireOp",EDGE,"E7.28.5"),sQuery(id+"F0.wireOp",EDGE,"E7.29.0"),sQuery(id+"F0.wireOp",EDGE,"E7.29.1"),sQuery(id+"F0.wireOp",EDGE,"E7.29.2"),sQuery(id+"F0.wireOp",EDGE,"E7.29.3"),sQuery(id+"F0.wireOp",EDGE,"E7.29.4"),sQuery(id+"F0.wireOp",EDGE,"E7.29.5"),sQuery(id+"F0.wireOp",EDGE,"E7.30.0"),sQuery(id+"F0.wireOp",EDGE,"E7.30.1"),sQuery(id+"F0.wireOp",EDGE,"E7.30.2"),sQuery(id+"F0.wireOp",EDGE,"E7.30.3"),sQuery(id+"F0.wireOp",EDGE,"E7.30.4"),sQuery(id+"F0.wireOp",EDGE,"E7.30.5"),sQuery(id+"F0.wireOp",EDGE,"E7.31.0"),sQuery(id+"F0.wireOp",EDGE,"E7.31.1"),sQuery(id+"F0.wireOp",EDGE,"E7.31.2"),sQuery(id+"F0.wireOp",EDGE,"E7.31.3"),sQuery(id+"F0.wireOp",EDGE,"E7.31.4"),sQuery(id+"F0.wireOp",EDGE,"E7.31.5"),sQuery(id+"F0.wireOp",EDGE,"E7.32.0"),sQuery(id+"F0.wireOp",EDGE,"E7.32.1"),sQuery(id+"F0.wireOp",EDGE,"E7.32.2"),sQuery(id+"F0.wireOp",EDGE,"E7.32.3"),sQuery(id+"F0.wireOp",EDGE,"E7.32.4"),sQuery(id+"F0.wireOp",EDGE,"E7.32.5"),sQuery(id+"F0.wireOp",EDGE,"E7.33.0"),sQuery(id+"F0.wireOp",EDGE,"E7.33.1"),sQuery(id+"F0.wireOp",EDGE,"E7.33.2"),sQuery(id+"F0.wireOp",EDGE,"E7.33.3"),sQuery(id+"F0.wireOp",EDGE,"E7.33.4"),sQuery(id+"F0.wireOp",EDGE,"E7.33.5"),sQuery(id+"F0.wireOp",EDGE,"E7.34.0"),sQuery(id+"F0.wireOp",EDGE,"E7.34.1"),sQuery(id+"F0.wireOp",EDGE,"E7.34.2"),sQuery(id+"F0.wireOp",EDGE,"E7.34.3"),sQuery(id+"F0.wireOp",EDGE,"E7.34.4"),sQuery(id+"F0.wireOp",EDGE,"E7.34.5"),sQuery(id+"F0.wireOp",EDGE,"E7.35.0"),sQuery(id+"F0.wireOp",EDGE,"E7.35.1"),sQuery(id+"F0.wireOp",EDGE,"E7.35.2"),sQuery(id+"F0.wireOp",EDGE,"E7.35.3"),sQuery(id+"F0.wireOp",EDGE,"E7.35.4"),sQuery(id+"F0.wireOp",EDGE,"E7.35.5"),sQuery(id+"F0.wireOp",EDGE,"E7.36.0"),sQuery(id+"F0.wireOp",EDGE,"E7.36.1"),sQuery(id+"F0.wireOp",EDGE,"E7.36.2"),sQuery(id+"F0.wireOp",EDGE,"E7.36.3"),sQuery(id+"F0.wireOp",EDGE,"E7.36.4"),sQuery(id+"F0.wireOp",EDGE,"E7.36.5"),sQuery(id+"F0.wireOp",EDGE,"E7.37.0"),sQuery(id+"F0.wireOp",EDGE,"E7.37.1"),sQuery(id+"F0.wireOp",EDGE,"E7.37.2"),sQuery(id+"F0.wireOp",EDGE,"E7.37.3"),sQuery(id+"F0.wireOp",EDGE,"E7.37.4"),sQuery(id+"F0.wireOp",EDGE,"E7.37.5"),sQuery(id+"F0.wireOp",EDGE,"E7.38.0"),sQuery(id+"F0.wireOp",EDGE,"E7.38.1"),sQuery(id+"F0.wireOp",EDGE,"E7.38.2"),sQuery(id+"F0.wireOp",EDGE,"E7.38.3"),sQuery(id+"F0.wireOp",EDGE,"E7.38.4"),sQuery(id+"F0.wireOp",EDGE,"E7.38.5"),sQuery(id+"F0.wireOp",EDGE,"E7.39.0"),sQuery(id+"F0.wireOp",EDGE,"E7.39.1"),sQuery(id+"F0.wireOp",EDGE,"E7.39.2"),sQuery(id+"F0.wireOp",EDGE,"E7.39.3"),sQuery(id+"F0.wireOp",EDGE,"E7.39.4"),sQuery(id+"F0.wireOp",EDGE,"E7.39.5"),sQuery(id+"F0.wireOp",EDGE,"E7.40.0"),sQuery(id+"F0.wireOp",EDGE,"E7.40.1"),sQuery(id+"F0.wireOp",EDGE,"E7.40.2"),sQuery(id+"F0.wireOp",EDGE,"E7.40.3"),sQuery(id+"F0.wireOp",EDGE,"E7.40.4"),sQuery(id+"F0.wireOp",EDGE,"E7.40.5"),sQuery(id+"F0.wireOp",EDGE,"E7.41.0"),sQuery(id+"F0.wireOp",EDGE,"E7.41.1"),sQuery(id+"F0.wireOp",EDGE,"E7.41.2"),sQuery(id+"F0.wireOp",EDGE,"E7.41.3"),sQuery(id+"F0.wireOp",EDGE,"E7.41.4"),sQuery(id+"F0.wireOp",EDGE,"E7.41.5"),sQuery(id+"F0.wireOp",EDGE,"E7.42.0"),sQuery(id+"F0.wireOp",EDGE,"E7.42.1"),sQuery(id+"F0.wireOp",EDGE,"E7.42.2"),sQuery(id+"F0.wireOp",EDGE,"E7.42.3"),sQuery(id+"F0.wireOp",EDGE,"E7.42.4"),sQuery(id+"F0.wireOp",EDGE,"E7.42.5"),sQuery(id+"F0.wireOp",EDGE,"E7.43.0"),sQuery(id+"F0.wireOp",EDGE,"E7.43.1"),sQuery(id+"F0.wireOp",EDGE,"E7.43.2"),sQuery(id+"F0.wireOp",EDGE,"E7.43.3"),sQuery(id+"F0.wireOp",EDGE,"E7.43.4"),sQuery(id+"F0.wireOp",EDGE,"E7.43.5"),sQuery(id+"F0.wireOp",EDGE,"E7.44.0"),sQuery(id+"F0.wireOp",EDGE,"E7.44.1"),sQuery(id+"F0.wireOp",EDGE,"E7.44.2"),sQuery(id+"F0.wireOp",EDGE,"E7.44.3"),sQuery(id+"F0.wireOp",EDGE,"E7.44.4"),sQuery(id+"F0.wireOp",EDGE,"E7.44.5"),sQuery(id+"F0.wireOp",EDGE,"E7.45.0"),sQuery(id+"F0.wireOp",EDGE,"E7.45.1"),sQuery(id+"F0.wireOp",EDGE,"E7.45.2"),sQuery(id+"F0.wireOp",EDGE,"E7.45.3"),sQuery(id+"F0.wireOp",EDGE,"E7.45.4"),sQuery(id+"F0.wireOp",EDGE,"E7.45.5"),sQuery(id+"F0.wireOp",EDGE,"E7.46.0"),sQuery(id+"F0.wireOp",EDGE,"E7.46.1"),sQuery(id+"F0.wireOp",EDGE,"E7.46.2"),sQuery(id+"F0.wireOp",EDGE,"E7.46.3"),sQuery(id+"F0.wireOp",EDGE,"E7.46.4"),sQuery(id+"F0.wireOp",EDGE,"E7.46.5"),sQuery(id+"F0.wireOp",EDGE,"E7.47.0"),sQuery(id+"F0.wireOp",EDGE,"E7.47.1"),sQuery(id+"F0.wireOp",EDGE,"E7.47.2"),sQuery(id+"F0.wireOp",EDGE,"E7.47.3"),sQuery(id+"F0.wireOp",EDGE,"E7.47.4"),sQuery(id+"F0.wireOp",EDGE,"E7.47.5"),sQuery(id+"F0.wireOp",EDGE,"E7.48.0"),sQuery(id+"F0.wireOp",EDGE,"E7.48.1"),sQuery(id+"F0.wireOp",EDGE,"E7.48.2"),sQuery(id+"F0.wireOp",EDGE,"E7.48.3"),sQuery(id+"F0.wireOp",EDGE,"E7.48.4"),sQuery(id+"F0.wireOp",EDGE,"E7.48.5"),sQuery(id+"F0.wireOp",EDGE,"E7.49.0"),sQuery(id+"F0.wireOp",EDGE,"E7.49.1"),sQuery(id+"F0.wireOp",EDGE,"E7.49.2"),sQuery(id+"F0.wireOp",EDGE,"E7.49.3"),sQuery(id+"F0.wireOp",EDGE,"E7.49.4"),sQuery(id+"F0.wireOp",EDGE,"E7.49.5"),sQuery(id+"F0.wireOp",EDGE,"E7.50.0"),sQuery(id+"F0.wireOp",EDGE,"E7.50.1"),sQuery(id+"F0.wireOp",EDGE,"E7.50.2"),sQuery(id+"F0.wireOp",EDGE,"E7.50.3"),sQuery(id+"F0.wireOp",EDGE,"E7.50.4"),sQuery(id+"F0.wireOp",EDGE,"E7.50.5"),sQuery(id+"F0.wireOp",EDGE,"E7.51.0"),sQuery(id+"F0.wireOp",EDGE,"E7.51.1"),sQuery(id+"F0.wireOp",EDGE,"E7.51.2"),sQuery(id+"F0.wireOp",EDGE,"E7.51.3"),sQuery(id+"F0.wireOp",EDGE,"E7.51.4"),sQuery(id+"F0.wireOp",EDGE,"E7.51.5"),sQuery(id+"F0.wireOp",EDGE,"E7.52.0"),sQuery(id+"F0.wireOp",EDGE,"E7.52.1"),sQuery(id+"F0.wireOp",EDGE,"E7.52.2"),sQuery(id+"F0.wireOp",EDGE,"E7.52.3"),sQuery(id+"F0.wireOp",EDGE,"E7.52.4"),sQuery(id+"F0.wireOp",EDGE,"E7.52.5"),sQuery(id+"F0.wireOp",EDGE,"E7.53.0"),sQuery(id+"F0.wireOp",EDGE,"E7.53.1"),sQuery(id+"F0.wireOp",EDGE,"E7.53.2"),sQuery(id+"F0.wireOp",EDGE,"E7.53.3"),sQuery(id+"F0.wireOp",EDGE,"E7.53.4"),sQuery(id+"F0.wireOp",EDGE,"E7.53.5"),sQuery(id+"F0.wireOp",EDGE,"E7.54.0"),sQuery(id+"F0.wireOp",EDGE,"E7.54.1"),sQuery(id+"F0.wireOp",EDGE,"E7.54.2"),sQuery(id+"F0.wireOp",EDGE,"E7.54.3"),sQuery(id+"F0.wireOp",EDGE,"E7.54.4"),sQuery(id+"F0.wireOp",EDGE,"E7.54.5"),sQuery(id+"F0.wireOp",EDGE,"E7.55.0"),sQuery(id+"F0.wireOp",EDGE,"E7.55.1"),sQuery(id+"F0.wireOp",EDGE,"E7.55.2"),sQuery(id+"F0.wireOp",EDGE,"E7.55.3"),sQuery(id+"F0.wireOp",EDGE,"E7.55.4"),sQuery(id+"F0.wireOp",EDGE,"E7.55.5"),sQuery(id+"F0.wireOp",EDGE,"E7.56.0"),sQuery(id+"F0.wireOp",EDGE,"E7.56.1"),sQuery(id+"F0.wireOp",EDGE,"E7.56.2"),sQuery(id+"F0.wireOp",EDGE,"E7.56.3"),sQuery(id+"F0.wireOp",EDGE,"E7.56.4"),sQuery(id+"F0.wireOp",EDGE,"E7.56.5"),sQuery(id+"F0.wireOp",EDGE,"E7.57.0"),sQuery(id+"F0.wireOp",EDGE,"E7.57.1"),sQuery(id+"F0.wireOp",EDGE,"E7.57.2"),sQuery(id+"F0.wireOp",EDGE,"E7.57.3"),sQuery(id+"F0.wireOp",EDGE,"E7.57.4"),sQuery(id+"F0.wireOp",EDGE,"E7.57.5"),sQuery(id+"F0.wireOp",EDGE,"E7.58.0"),sQuery(id+"F0.wireOp",EDGE,"E7.58.1"),sQuery(id+"F0.wireOp",EDGE,"E7.58.2"),sQuery(id+"F0.wireOp",EDGE,"E7.58.3"),sQuery(id+"F0.wireOp",EDGE,"E7.58.4"),sQuery(id+"F0.wireOp",EDGE,"E7.58.5"),sQuery(id+"F0.wireOp",EDGE,"E7.59.0"),sQuery(id+"F0.wireOp",EDGE,"E7.59.1"),sQuery(id+"F0.wireOp",EDGE,"E7.59.2"),sQuery(id+"F0.wireOp",EDGE,"E7.59.3"),sQuery(id+"F0.wireOp",EDGE,"E7.59.4"),sQuery(id+"F0.wireOp",EDGE,"E7.59.5"),sQuery(id+"F0.wireOp",EDGE,"E8"),sQuery(id+"F0.wireOp",EDGE,"E9"),sQuery(id+"F0.wireOp",EDGE,"E10"),sQuery(id+"F0.wireOp",EDGE,"E11.filletArc"),sQuery(id+"F0.wireOp",EDGE,"E12.filletArc"),sQuery(id+"F0.wireOp",EDGE,"E13.filletArc"),sQuery(id+"F0.wireOp",EDGE,"E14.MirrorCS"),sQuery(id+"F0.wireOp",EDGE,"E15.MirrorCS"),sQuery(id+"F0.wireOp",EDGE,"E16.MirrorCS"),sQuery(id+"F0.wireOp",EDGE,"E17.MirrorCS"),sQuery(id+"F0.wireOp",EDGE,"E18.MirrorCS"),sQuery(id+"F0.wireOp",EDGE,"E19.MirrorCS"),sQuery(id+"F0.wireOp",EDGE,"E21.MirrorCS"),sQuery(id+"F0.wireOp",EDGE,"E22.MirrorCS"),sQuery(id+"F0.wireOp",EDGE,"E23.MirrorCS"),sQuery(id+"F0.wireOp",EDGE,"E24.MirrorCS"),sQuery(id+"F0.wireOp",EDGE,"E25.MirrorCS"),sQuery(id+"F0.wireOp",EDGE,"E20.MirrorCS"),sQuery(id+"F0.wireOp",EDGE,"E27.MirrorCS"),sQuery(id+"F0.wireOp",EDGE,"E28.MirrorCS"),sQuery(id+"F0.wireOp",EDGE,"E29.MirrorCS"),sQuery(id+"F0.wireOp",EDGE,"E30.MirrorCS"),sQuery(id+"F0.wireOp",EDGE,"E31.MirrorCS"),sQuery(id+"F0.wireOp",EDGE,"E32.MirrorCS"),sQuery(id+"F0.wireOp",EDGE,"E33"),sQuery(id+"F0.wireOp",EDGE,"E34.1.0"),sQuery(id+"F0.wireOp",EDGE,"E34.2.0"),sQuery(id+"F0.wireOp",EDGE,"E34.3.0"),sQuery(id+"F0.wireOp",EDGE,"E34.4.0"),sQuery(id+"F0.wireOp",EDGE,"E34.5.0"),sQuery(id+"F0.wireOp",EDGE,"E34.6.0"),sQuery(id+"F0.wireOp",EDGE,"E34.7.0"),sQuery(id+"F0.wireOp",EDGE,"E34.8.0"),sQuery(id+"F0.wireOp",EDGE,"E34.9.0"),sQuery(id+"F0.wireOp",EDGE,"E34.10.0"),sQuery(id+"F0.wireOp",EDGE,"E34.11.0"),sQuery(id+"F0.wireOp",EDGE,"E34.12.0"),sQuery(id+"F0.wireOp",EDGE,"E34.13.0"),sQuery(id+"F0.wireOp",EDGE,"E34.14.0"),sQuery(id+"F0.wireOp",EDGE,"E34.15.0"),sQuery(id+"F0.wireOp",EDGE,"E34.16.0"),sQuery(id+"F0.wireOp",EDGE,"E34.17.0"),sQuery(id+"F0.wireOp",EDGE,"E34.18.0"),sQuery(id+"F0.wireOp",EDGE,"E34.19.0"),sQuery(id+"F0.wireOp",EDGE,"E34.20.0"),sQuery(id+"F0.wireOp",EDGE,"E34.21.0"),sQuery(id+"F0.wireOp",EDGE,"E34.22.0"),sQuery(id+"F0.wireOp",EDGE,"E34.23.0"),sQuery(id+"F0.wireOp",EDGE,"E34.24.0"),sQuery(id+"F0.wireOp",EDGE,"E34.25.0"),sQuery(id+"F0.wireOp",EDGE,"E34.26.0"),sQuery(id+"F0.wireOp",EDGE,"E34.27.0"),sQuery(id+"F0.wireOp",EDGE,"E34.28.0"),sQuery(id+"F0.wireOp",EDGE,"E34.29.0"),sQuery(id+"F0.wireOp",EDGE,"E34.30.0"),sQuery(id+"F0.wireOp",EDGE,"E34.31.0"),sQuery(id+"F0.wireOp",EDGE,"E34.32.0"),sQuery(id+"F0.wireOp",EDGE,"E34.33.0"),sQuery(id+"F0.wireOp",EDGE,"E34.34.0"),sQuery(id+"F0.wireOp",EDGE,"E34.35.0"),sQuery(id+"F0.wireOp",EDGE,"E34.36.0"),sQuery(id+"F0.wireOp",EDGE,"E34.37.0"),sQuery(id+"F0.wireOp",EDGE,"E34.38.0"),sQuery(id+"F0.wireOp",EDGE,"E34.39.0"),sQuery(id+"F0.wireOp",EDGE,"E34.40.0"),sQuery(id+"F0.wireOp",EDGE,"E34.41.0"),sQuery(id+"F0.wireOp",EDGE,"E34.42.0"),sQuery(id+"F0.wireOp",EDGE,"E34.43.0"),sQuery(id+"F0.wireOp",EDGE,"E34.44.0"),sQuery(id+"F0.wireOp",EDGE,"E34.45.0"),sQuery(id+"F0.wireOp",EDGE,"E34.46.0"),sQuery(id+"F0.wireOp",EDGE,"E34.47.0"),sQuery(id+"F0.wireOp",EDGE,"E34.48.0"),sQuery(id+"F0.wireOp",EDGE,"E34.49.0"),sQuery(id+"F0.wireOp",EDGE,"E34.50.0"),sQuery(id+"F0.wireOp",EDGE,"E34.51.0"),sQuery(id+"F0.wireOp",EDGE,"E34.52.0"),sQuery(id+"F0.wireOp",EDGE,"E34.53.0"),sQuery(id+"F0.wireOp",EDGE,"E34.54.0"),sQuery(id+"F0.wireOp",EDGE,"E34.55.0"),sQuery(id+"F0.wireOp",EDGE,"E34.56.0"),sQuery(id+"F0.wireOp",EDGE,"E34.57.0"),sQuery(id+"F0.wireOp",EDGE,"E34.58.0"),sQuery(id+"F0.wireOp",EDGE,"E34.59.0")])]});
            transform(context, id + "F3", {"entities" : qUnion([Q0]), "transformType" : TransformType.TRANSLATION_3D, "dx" : 0 * mm, "dy" : 0 * mm, "dz" : 0 * mm, "makeCopy" : true});
        }
        {
            var Q0;
            Q0=makeQuery(id+"F3.opPattern","COPY",BODY,{"derivedFrom":makeQuery(id+"F1.opExtrude","SWEPT_BODY",BODY,{"disambiguationData":[OSD([sQuery(id+"F0.wireOp",EDGE,"E0"),sQuery(id+"F0.wireOp",EDGE,"E1"),sQuery(id+"F0.wireOp",EDGE,"E2"),sQuery(id+"F0.wireOp",EDGE,"E3"),sQuery(id+"F0.wireOp",EDGE,"E4.MirrorCS"),sQuery(id+"F0.wireOp",EDGE,"E5.MirrorCS"),sQuery(id+"F0.wireOp",EDGE,"E6.MirrorCS"),sQuery(id+"F0.wireOp",EDGE,"E7.1.0"),sQuery(id+"F0.wireOp",EDGE,"E7.1.1"),sQuery(id+"F0.wireOp",EDGE,"E7.1.2"),sQuery(id+"F0.wireOp",EDGE,"E7.1.3"),sQuery(id+"F0.wireOp",EDGE,"E7.1.4"),sQuery(id+"F0.wireOp",EDGE,"E7.1.5"),sQuery(id+"F0.wireOp",EDGE,"E7.2.0"),sQuery(id+"F0.wireOp",EDGE,"E7.2.1"),sQuery(id+"F0.wireOp",EDGE,"E7.2.2"),sQuery(id+"F0.wireOp",EDGE,"E7.2.3"),sQuery(id+"F0.wireOp",EDGE,"E7.2.4"),sQuery(id+"F0.wireOp",EDGE,"E7.2.5"),sQuery(id+"F0.wireOp",EDGE,"E7.3.0"),sQuery(id+"F0.wireOp",EDGE,"E7.3.1"),sQuery(id+"F0.wireOp",EDGE,"E7.3.2"),sQuery(id+"F0.wireOp",EDGE,"E7.3.3"),sQuery(id+"F0.wireOp",EDGE,"E7.3.4"),sQuery(id+"F0.wireOp",EDGE,"E7.3.5"),sQuery(id+"F0.wireOp",EDGE,"E7.4.0"),sQuery(id+"F0.wireOp",EDGE,"E7.4.1"),sQuery(id+"F0.wireOp",EDGE,"E7.4.2"),sQuery(id+"F0.wireOp",EDGE,"E7.4.3"),sQuery(id+"F0.wireOp",EDGE,"E7.4.4"),sQuery(id+"F0.wireOp",EDGE,"E7.4.5"),sQuery(id+"F0.wireOp",EDGE,"E7.5.0"),sQuery(id+"F0.wireOp",EDGE,"E7.5.1"),sQuery(id+"F0.wireOp",EDGE,"E7.5.2"),sQuery(id+"F0.wireOp",EDGE,"E7.5.3"),sQuery(id+"F0.wireOp",EDGE,"E7.5.4"),sQuery(id+"F0.wireOp",EDGE,"E7.5.5"),sQuery(id+"F0.wireOp",EDGE,"E7.6.0"),sQuery(id+"F0.wireOp",EDGE,"E7.6.1"),sQuery(id+"F0.wireOp",EDGE,"E7.6.2"),sQuery(id+"F0.wireOp",EDGE,"E7.6.3"),sQuery(id+"F0.wireOp",EDGE,"E7.6.4"),sQuery(id+"F0.wireOp",EDGE,"E7.6.5"),sQuery(id+"F0.wireOp",EDGE,"E7.7.0"),sQuery(id+"F0.wireOp",EDGE,"E7.7.1"),sQuery(id+"F0.wireOp",EDGE,"E7.7.2"),sQuery(id+"F0.wireOp",EDGE,"E7.7.3"),sQuery(id+"F0.wireOp",EDGE,"E7.7.4"),sQuery(id+"F0.wireOp",EDGE,"E7.7.5"),sQuery(id+"F0.wireOp",EDGE,"E7.8.0"),sQuery(id+"F0.wireOp",EDGE,"E7.8.1"),sQuery(id+"F0.wireOp",EDGE,"E7.8.2"),sQuery(id+"F0.wireOp",EDGE,"E7.8.3"),sQuery(id+"F0.wireOp",EDGE,"E7.8.4"),sQuery(id+"F0.wireOp",EDGE,"E7.8.5"),sQuery(id+"F0.wireOp",EDGE,"E7.9.0"),sQuery(id+"F0.wireOp",EDGE,"E7.9.1"),sQuery(id+"F0.wireOp",EDGE,"E7.9.2"),sQuery(id+"F0.wireOp",EDGE,"E7.9.3"),sQuery(id+"F0.wireOp",EDGE,"E7.9.4"),sQuery(id+"F0.wireOp",EDGE,"E7.9.5"),sQuery(id+"F0.wireOp",EDGE,"E7.10.0"),sQuery(id+"F0.wireOp",EDGE,"E7.10.1"),sQuery(id+"F0.wireOp",EDGE,"E7.10.2"),sQuery(id+"F0.wireOp",EDGE,"E7.10.3"),sQuery(id+"F0.wireOp",EDGE,"E7.10.4"),sQuery(id+"F0.wireOp",EDGE,"E7.10.5"),sQuery(id+"F0.wireOp",EDGE,"E7.11.0"),sQuery(id+"F0.wireOp",EDGE,"E7.11.1"),sQuery(id+"F0.wireOp",EDGE,"E7.11.2"),sQuery(id+"F0.wireOp",EDGE,"E7.11.3"),sQuery(id+"F0.wireOp",EDGE,"E7.11.4"),sQuery(id+"F0.wireOp",EDGE,"E7.11.5"),sQuery(id+"F0.wireOp",EDGE,"E7.12.0"),sQuery(id+"F0.wireOp",EDGE,"E7.12.1"),sQuery(id+"F0.wireOp",EDGE,"E7.12.2"),sQuery(id+"F0.wireOp",EDGE,"E7.12.3"),sQuery(id+"F0.wireOp",EDGE,"E7.12.4"),sQuery(id+"F0.wireOp",EDGE,"E7.12.5"),sQuery(id+"F0.wireOp",EDGE,"E7.13.0"),sQuery(id+"F0.wireOp",EDGE,"E7.13.1"),sQuery(id+"F0.wireOp",EDGE,"E7.13.2"),sQuery(id+"F0.wireOp",EDGE,"E7.13.3"),sQuery(id+"F0.wireOp",EDGE,"E7.13.4"),sQuery(id+"F0.wireOp",EDGE,"E7.13.5"),sQuery(id+"F0.wireOp",EDGE,"E7.14.0"),sQuery(id+"F0.wireOp",EDGE,"E7.14.1"),sQuery(id+"F0.wireOp",EDGE,"E7.14.2"),sQuery(id+"F0.wireOp",EDGE,"E7.14.3"),sQuery(id+"F0.wireOp",EDGE,"E7.14.4"),sQuery(id+"F0.wireOp",EDGE,"E7.14.5"),sQuery(id+"F0.wireOp",EDGE,"E7.15.0"),sQuery(id+"F0.wireOp",EDGE,"E7.15.1"),sQuery(id+"F0.wireOp",EDGE,"E7.15.2"),sQuery(id+"F0.wireOp",EDGE,"E7.15.3"),sQuery(id+"F0.wireOp",EDGE,"E7.15.4"),sQuery(id+"F0.wireOp",EDGE,"E7.15.5"),sQuery(id+"F0.wireOp",EDGE,"E7.16.0"),sQuery(id+"F0.wireOp",EDGE,"E7.16.1"),sQuery(id+"F0.wireOp",EDGE,"E7.16.2"),sQuery(id+"F0.wireOp",EDGE,"E7.16.3"),sQuery(id+"F0.wireOp",EDGE,"E7.16.4"),sQuery(id+"F0.wireOp",EDGE,"E7.16.5"),sQuery(id+"F0.wireOp",EDGE,"E7.17.0"),sQuery(id+"F0.wireOp",EDGE,"E7.17.1"),sQuery(id+"F0.wireOp",EDGE,"E7.17.2"),sQuery(id+"F0.wireOp",EDGE,"E7.17.3"),sQuery(id+"F0.wireOp",EDGE,"E7.17.4"),sQuery(id+"F0.wireOp",EDGE,"E7.17.5"),sQuery(id+"F0.wireOp",EDGE,"E7.18.0"),sQuery(id+"F0.wireOp",EDGE,"E7.18.1"),sQuery(id+"F0.wireOp",EDGE,"E7.18.2"),sQuery(id+"F0.wireOp",EDGE,"E7.18.3"),sQuery(id+"F0.wireOp",EDGE,"E7.18.4"),sQuery(id+"F0.wireOp",EDGE,"E7.18.5"),sQuery(id+"F0.wireOp",EDGE,"E7.19.0"),sQuery(id+"F0.wireOp",EDGE,"E7.19.1"),sQuery(id+"F0.wireOp",EDGE,"E7.19.2"),sQuery(id+"F0.wireOp",EDGE,"E7.19.3"),sQuery(id+"F0.wireOp",EDGE,"E7.19.4"),sQuery(id+"F0.wireOp",EDGE,"E7.19.5"),sQuery(id+"F0.wireOp",EDGE,"E7.20.0"),sQuery(id+"F0.wireOp",EDGE,"E7.20.1"),sQuery(id+"F0.wireOp",EDGE,"E7.20.2"),sQuery(id+"F0.wireOp",EDGE,"E7.20.3"),sQuery(id+"F0.wireOp",EDGE,"E7.20.4"),sQuery(id+"F0.wireOp",EDGE,"E7.20.5"),sQuery(id+"F0.wireOp",EDGE,"E7.21.0"),sQuery(id+"F0.wireOp",EDGE,"E7.21.1"),sQuery(id+"F0.wireOp",EDGE,"E7.21.2"),sQuery(id+"F0.wireOp",EDGE,"E7.21.3"),sQuery(id+"F0.wireOp",EDGE,"E7.21.4"),sQuery(id+"F0.wireOp",EDGE,"E7.21.5"),sQuery(id+"F0.wireOp",EDGE,"E7.22.0"),sQuery(id+"F0.wireOp",EDGE,"E7.22.1"),sQuery(id+"F0.wireOp",EDGE,"E7.22.2"),sQuery(id+"F0.wireOp",EDGE,"E7.22.3"),sQuery(id+"F0.wireOp",EDGE,"E7.22.4"),sQuery(id+"F0.wireOp",EDGE,"E7.22.5"),sQuery(id+"F0.wireOp",EDGE,"E7.23.0"),sQuery(id+"F0.wireOp",EDGE,"E7.23.1"),sQuery(id+"F0.wireOp",EDGE,"E7.23.2"),sQuery(id+"F0.wireOp",EDGE,"E7.23.3"),sQuery(id+"F0.wireOp",EDGE,"E7.23.4"),sQuery(id+"F0.wireOp",EDGE,"E7.23.5"),sQuery(id+"F0.wireOp",EDGE,"E7.24.0"),sQuery(id+"F0.wireOp",EDGE,"E7.24.1"),sQuery(id+"F0.wireOp",EDGE,"E7.24.2"),sQuery(id+"F0.wireOp",EDGE,"E7.24.3"),sQuery(id+"F0.wireOp",EDGE,"E7.24.4"),sQuery(id+"F0.wireOp",EDGE,"E7.24.5"),sQuery(id+"F0.wireOp",EDGE,"E7.25.0"),sQuery(id+"F0.wireOp",EDGE,"E7.25.1"),sQuery(id+"F0.wireOp",EDGE,"E7.25.2"),sQuery(id+"F0.wireOp",EDGE,"E7.25.3"),sQuery(id+"F0.wireOp",EDGE,"E7.25.4"),sQuery(id+"F0.wireOp",EDGE,"E7.25.5"),sQuery(id+"F0.wireOp",EDGE,"E7.26.0"),sQuery(id+"F0.wireOp",EDGE,"E7.26.1"),sQuery(id+"F0.wireOp",EDGE,"E7.26.2"),sQuery(id+"F0.wireOp",EDGE,"E7.26.3"),sQuery(id+"F0.wireOp",EDGE,"E7.26.4"),sQuery(id+"F0.wireOp",EDGE,"E7.26.5"),sQuery(id+"F0.wireOp",EDGE,"E7.27.0"),sQuery(id+"F0.wireOp",EDGE,"E7.27.1"),sQuery(id+"F0.wireOp",EDGE,"E7.27.2"),sQuery(id+"F0.wireOp",EDGE,"E7.27.3"),sQuery(id+"F0.wireOp",EDGE,"E7.27.4"),sQuery(id+"F0.wireOp",EDGE,"E7.27.5"),sQuery(id+"F0.wireOp",EDGE,"E7.28.0"),sQuery(id+"F0.wireOp",EDGE,"E7.28.1"),sQuery(id+"F0.wireOp",EDGE,"E7.28.2"),sQuery(id+"F0.wireOp",EDGE,"E7.28.3"),sQuery(id+"F0.wireOp",EDGE,"E7.28.4"),sQuery(id+"F0.wireOp",EDGE,"E7.28.5"),sQuery(id+"F0.wireOp",EDGE,"E7.29.0"),sQuery(id+"F0.wireOp",EDGE,"E7.29.1"),sQuery(id+"F0.wireOp",EDGE,"E7.29.2"),sQuery(id+"F0.wireOp",EDGE,"E7.29.3"),sQuery(id+"F0.wireOp",EDGE,"E7.29.4"),sQuery(id+"F0.wireOp",EDGE,"E7.29.5"),sQuery(id+"F0.wireOp",EDGE,"E7.30.0"),sQuery(id+"F0.wireOp",EDGE,"E7.30.1"),sQuery(id+"F0.wireOp",EDGE,"E7.30.2"),sQuery(id+"F0.wireOp",EDGE,"E7.30.3"),sQuery(id+"F0.wireOp",EDGE,"E7.30.4"),sQuery(id+"F0.wireOp",EDGE,"E7.30.5"),sQuery(id+"F0.wireOp",EDGE,"E7.31.0"),sQuery(id+"F0.wireOp",EDGE,"E7.31.1"),sQuery(id+"F0.wireOp",EDGE,"E7.31.2"),sQuery(id+"F0.wireOp",EDGE,"E7.31.3"),sQuery(id+"F0.wireOp",EDGE,"E7.31.4"),sQuery(id+"F0.wireOp",EDGE,"E7.31.5"),sQuery(id+"F0.wireOp",EDGE,"E7.32.0"),sQuery(id+"F0.wireOp",EDGE,"E7.32.1"),sQuery(id+"F0.wireOp",EDGE,"E7.32.2"),sQuery(id+"F0.wireOp",EDGE,"E7.32.3"),sQuery(id+"F0.wireOp",EDGE,"E7.32.4"),sQuery(id+"F0.wireOp",EDGE,"E7.32.5"),sQuery(id+"F0.wireOp",EDGE,"E7.33.0"),sQuery(id+"F0.wireOp",EDGE,"E7.33.1"),sQuery(id+"F0.wireOp",EDGE,"E7.33.2"),sQuery(id+"F0.wireOp",EDGE,"E7.33.3"),sQuery(id+"F0.wireOp",EDGE,"E7.33.4"),sQuery(id+"F0.wireOp",EDGE,"E7.33.5"),sQuery(id+"F0.wireOp",EDGE,"E7.34.0"),sQuery(id+"F0.wireOp",EDGE,"E7.34.1"),sQuery(id+"F0.wireOp",EDGE,"E7.34.2"),sQuery(id+"F0.wireOp",EDGE,"E7.34.3"),sQuery(id+"F0.wireOp",EDGE,"E7.34.4"),sQuery(id+"F0.wireOp",EDGE,"E7.34.5"),sQuery(id+"F0.wireOp",EDGE,"E7.35.0"),sQuery(id+"F0.wireOp",EDGE,"E7.35.1"),sQuery(id+"F0.wireOp",EDGE,"E7.35.2"),sQuery(id+"F0.wireOp",EDGE,"E7.35.3"),sQuery(id+"F0.wireOp",EDGE,"E7.35.4"),sQuery(id+"F0.wireOp",EDGE,"E7.35.5"),sQuery(id+"F0.wireOp",EDGE,"E7.36.0"),sQuery(id+"F0.wireOp",EDGE,"E7.36.1"),sQuery(id+"F0.wireOp",EDGE,"E7.36.2"),sQuery(id+"F0.wireOp",EDGE,"E7.36.3"),sQuery(id+"F0.wireOp",EDGE,"E7.36.4"),sQuery(id+"F0.wireOp",EDGE,"E7.36.5"),sQuery(id+"F0.wireOp",EDGE,"E7.37.0"),sQuery(id+"F0.wireOp",EDGE,"E7.37.1"),sQuery(id+"F0.wireOp",EDGE,"E7.37.2"),sQuery(id+"F0.wireOp",EDGE,"E7.37.3"),sQuery(id+"F0.wireOp",EDGE,"E7.37.4"),sQuery(id+"F0.wireOp",EDGE,"E7.37.5"),sQuery(id+"F0.wireOp",EDGE,"E7.38.0"),sQuery(id+"F0.wireOp",EDGE,"E7.38.1"),sQuery(id+"F0.wireOp",EDGE,"E7.38.2"),sQuery(id+"F0.wireOp",EDGE,"E7.38.3"),sQuery(id+"F0.wireOp",EDGE,"E7.38.4"),sQuery(id+"F0.wireOp",EDGE,"E7.38.5"),sQuery(id+"F0.wireOp",EDGE,"E7.39.0"),sQuery(id+"F0.wireOp",EDGE,"E7.39.1"),sQuery(id+"F0.wireOp",EDGE,"E7.39.2"),sQuery(id+"F0.wireOp",EDGE,"E7.39.3"),sQuery(id+"F0.wireOp",EDGE,"E7.39.4"),sQuery(id+"F0.wireOp",EDGE,"E7.39.5"),sQuery(id+"F0.wireOp",EDGE,"E7.40.0"),sQuery(id+"F0.wireOp",EDGE,"E7.40.1"),sQuery(id+"F0.wireOp",EDGE,"E7.40.2"),sQuery(id+"F0.wireOp",EDGE,"E7.40.3"),sQuery(id+"F0.wireOp",EDGE,"E7.40.4"),sQuery(id+"F0.wireOp",EDGE,"E7.40.5"),sQuery(id+"F0.wireOp",EDGE,"E7.41.0"),sQuery(id+"F0.wireOp",EDGE,"E7.41.1"),sQuery(id+"F0.wireOp",EDGE,"E7.41.2"),sQuery(id+"F0.wireOp",EDGE,"E7.41.3"),sQuery(id+"F0.wireOp",EDGE,"E7.41.4"),sQuery(id+"F0.wireOp",EDGE,"E7.41.5"),sQuery(id+"F0.wireOp",EDGE,"E7.42.0"),sQuery(id+"F0.wireOp",EDGE,"E7.42.1"),sQuery(id+"F0.wireOp",EDGE,"E7.42.2"),sQuery(id+"F0.wireOp",EDGE,"E7.42.3"),sQuery(id+"F0.wireOp",EDGE,"E7.42.4"),sQuery(id+"F0.wireOp",EDGE,"E7.42.5"),sQuery(id+"F0.wireOp",EDGE,"E7.43.0"),sQuery(id+"F0.wireOp",EDGE,"E7.43.1"),sQuery(id+"F0.wireOp",EDGE,"E7.43.2"),sQuery(id+"F0.wireOp",EDGE,"E7.43.3"),sQuery(id+"F0.wireOp",EDGE,"E7.43.4"),sQuery(id+"F0.wireOp",EDGE,"E7.43.5"),sQuery(id+"F0.wireOp",EDGE,"E7.44.0"),sQuery(id+"F0.wireOp",EDGE,"E7.44.1"),sQuery(id+"F0.wireOp",EDGE,"E7.44.2"),sQuery(id+"F0.wireOp",EDGE,"E7.44.3"),sQuery(id+"F0.wireOp",EDGE,"E7.44.4"),sQuery(id+"F0.wireOp",EDGE,"E7.44.5"),sQuery(id+"F0.wireOp",EDGE,"E7.45.0"),sQuery(id+"F0.wireOp",EDGE,"E7.45.1"),sQuery(id+"F0.wireOp",EDGE,"E7.45.2"),sQuery(id+"F0.wireOp",EDGE,"E7.45.3"),sQuery(id+"F0.wireOp",EDGE,"E7.45.4"),sQuery(id+"F0.wireOp",EDGE,"E7.45.5"),sQuery(id+"F0.wireOp",EDGE,"E7.46.0"),sQuery(id+"F0.wireOp",EDGE,"E7.46.1"),sQuery(id+"F0.wireOp",EDGE,"E7.46.2"),sQuery(id+"F0.wireOp",EDGE,"E7.46.3"),sQuery(id+"F0.wireOp",EDGE,"E7.46.4"),sQuery(id+"F0.wireOp",EDGE,"E7.46.5"),sQuery(id+"F0.wireOp",EDGE,"E7.47.0"),sQuery(id+"F0.wireOp",EDGE,"E7.47.1"),sQuery(id+"F0.wireOp",EDGE,"E7.47.2"),sQuery(id+"F0.wireOp",EDGE,"E7.47.3"),sQuery(id+"F0.wireOp",EDGE,"E7.47.4"),sQuery(id+"F0.wireOp",EDGE,"E7.47.5"),sQuery(id+"F0.wireOp",EDGE,"E7.48.0"),sQuery(id+"F0.wireOp",EDGE,"E7.48.1"),sQuery(id+"F0.wireOp",EDGE,"E7.48.2"),sQuery(id+"F0.wireOp",EDGE,"E7.48.3"),sQuery(id+"F0.wireOp",EDGE,"E7.48.4"),sQuery(id+"F0.wireOp",EDGE,"E7.48.5"),sQuery(id+"F0.wireOp",EDGE,"E7.49.0"),sQuery(id+"F0.wireOp",EDGE,"E7.49.1"),sQuery(id+"F0.wireOp",EDGE,"E7.49.2"),sQuery(id+"F0.wireOp",EDGE,"E7.49.3"),sQuery(id+"F0.wireOp",EDGE,"E7.49.4"),sQuery(id+"F0.wireOp",EDGE,"E7.49.5"),sQuery(id+"F0.wireOp",EDGE,"E7.50.0"),sQuery(id+"F0.wireOp",EDGE,"E7.50.1"),sQuery(id+"F0.wireOp",EDGE,"E7.50.2"),sQuery(id+"F0.wireOp",EDGE,"E7.50.3"),sQuery(id+"F0.wireOp",EDGE,"E7.50.4"),sQuery(id+"F0.wireOp",EDGE,"E7.50.5"),sQuery(id+"F0.wireOp",EDGE,"E7.51.0"),sQuery(id+"F0.wireOp",EDGE,"E7.51.1"),sQuery(id+"F0.wireOp",EDGE,"E7.51.2"),sQuery(id+"F0.wireOp",EDGE,"E7.51.3"),sQuery(id+"F0.wireOp",EDGE,"E7.51.4"),sQuery(id+"F0.wireOp",EDGE,"E7.51.5"),sQuery(id+"F0.wireOp",EDGE,"E7.52.0"),sQuery(id+"F0.wireOp",EDGE,"E7.52.1"),sQuery(id+"F0.wireOp",EDGE,"E7.52.2"),sQuery(id+"F0.wireOp",EDGE,"E7.52.3"),sQuery(id+"F0.wireOp",EDGE,"E7.52.4"),sQuery(id+"F0.wireOp",EDGE,"E7.52.5"),sQuery(id+"F0.wireOp",EDGE,"E7.53.0"),sQuery(id+"F0.wireOp",EDGE,"E7.53.1"),sQuery(id+"F0.wireOp",EDGE,"E7.53.2"),sQuery(id+"F0.wireOp",EDGE,"E7.53.3"),sQuery(id+"F0.wireOp",EDGE,"E7.53.4"),sQuery(id+"F0.wireOp",EDGE,"E7.53.5"),sQuery(id+"F0.wireOp",EDGE,"E7.54.0"),sQuery(id+"F0.wireOp",EDGE,"E7.54.1"),sQuery(id+"F0.wireOp",EDGE,"E7.54.2"),sQuery(id+"F0.wireOp",EDGE,"E7.54.3"),sQuery(id+"F0.wireOp",EDGE,"E7.54.4"),sQuery(id+"F0.wireOp",EDGE,"E7.54.5"),sQuery(id+"F0.wireOp",EDGE,"E7.55.0"),sQuery(id+"F0.wireOp",EDGE,"E7.55.1"),sQuery(id+"F0.wireOp",EDGE,"E7.55.2"),sQuery(id+"F0.wireOp",EDGE,"E7.55.3"),sQuery(id+"F0.wireOp",EDGE,"E7.55.4"),sQuery(id+"F0.wireOp",EDGE,"E7.55.5"),sQuery(id+"F0.wireOp",EDGE,"E7.56.0"),sQuery(id+"F0.wireOp",EDGE,"E7.56.1"),sQuery(id+"F0.wireOp",EDGE,"E7.56.2"),sQuery(id+"F0.wireOp",EDGE,"E7.56.3"),sQuery(id+"F0.wireOp",EDGE,"E7.56.4"),sQuery(id+"F0.wireOp",EDGE,"E7.56.5"),sQuery(id+"F0.wireOp",EDGE,"E7.57.0"),sQuery(id+"F0.wireOp",EDGE,"E7.57.1"),sQuery(id+"F0.wireOp",EDGE,"E7.57.2"),sQuery(id+"F0.wireOp",EDGE,"E7.57.3"),sQuery(id+"F0.wireOp",EDGE,"E7.57.4"),sQuery(id+"F0.wireOp",EDGE,"E7.57.5"),sQuery(id+"F0.wireOp",EDGE,"E7.58.0"),sQuery(id+"F0.wireOp",EDGE,"E7.58.1"),sQuery(id+"F0.wireOp",EDGE,"E7.58.2"),sQuery(id+"F0.wireOp",EDGE,"E7.58.3"),sQuery(id+"F0.wireOp",EDGE,"E7.58.4"),sQuery(id+"F0.wireOp",EDGE,"E7.58.5"),sQuery(id+"F0.wireOp",EDGE,"E7.59.0"),sQuery(id+"F0.wireOp",EDGE,"E7.59.1"),sQuery(id+"F0.wireOp",EDGE,"E7.59.2"),sQuery(id+"F0.wireOp",EDGE,"E7.59.3"),sQuery(id+"F0.wireOp",EDGE,"E7.59.4"),sQuery(id+"F0.wireOp",EDGE,"E7.59.5"),sQuery(id+"F0.wireOp",EDGE,"E8"),sQuery(id+"F0.wireOp",EDGE,"E9"),sQuery(id+"F0.wireOp",EDGE,"E10"),sQuery(id+"F0.wireOp",EDGE,"E11.filletArc"),sQuery(id+"F0.wireOp",EDGE,"E12.filletArc"),sQuery(id+"F0.wireOp",EDGE,"E13.filletArc"),sQuery(id+"F0.wireOp",EDGE,"E14.MirrorCS"),sQuery(id+"F0.wireOp",EDGE,"E15.MirrorCS"),sQuery(id+"F0.wireOp",EDGE,"E16.MirrorCS"),sQuery(id+"F0.wireOp",EDGE,"E17.MirrorCS"),sQuery(id+"F0.wireOp",EDGE,"E18.MirrorCS"),sQuery(id+"F0.wireOp",EDGE,"E19.MirrorCS"),sQuery(id+"F0.wireOp",EDGE,"E21.MirrorCS"),sQuery(id+"F0.wireOp",EDGE,"E22.MirrorCS"),sQuery(id+"F0.wireOp",EDGE,"E23.MirrorCS"),sQuery(id+"F0.wireOp",EDGE,"E24.MirrorCS"),sQuery(id+"F0.wireOp",EDGE,"E25.MirrorCS"),sQuery(id+"F0.wireOp",EDGE,"E20.MirrorCS"),sQuery(id+"F0.wireOp",EDGE,"E27.MirrorCS"),sQuery(id+"F0.wireOp",EDGE,"E28.MirrorCS"),sQuery(id+"F0.wireOp",EDGE,"E29.MirrorCS"),sQuery(id+"F0.wireOp",EDGE,"E30.MirrorCS"),sQuery(id+"F0.wireOp",EDGE,"E31.MirrorCS"),sQuery(id+"F0.wireOp",EDGE,"E32.MirrorCS"),sQuery(id+"F0.wireOp",EDGE,"E33"),sQuery(id+"F0.wireOp",EDGE,"E34.1.0"),sQuery(id+"F0.wireOp",EDGE,"E34.2.0"),sQuery(id+"F0.wireOp",EDGE,"E34.3.0"),sQuery(id+"F0.wireOp",EDGE,"E34.4.0"),sQuery(id+"F0.wireOp",EDGE,"E34.5.0"),sQuery(id+"F0.wireOp",EDGE,"E34.6.0"),sQuery(id+"F0.wireOp",EDGE,"E34.7.0"),sQuery(id+"F0.wireOp",EDGE,"E34.8.0"),sQuery(id+"F0.wireOp",EDGE,"E34.9.0"),sQuery(id+"F0.wireOp",EDGE,"E34.10.0"),sQuery(id+"F0.wireOp",EDGE,"E34.11.0"),sQuery(id+"F0.wireOp",EDGE,"E34.12.0"),sQuery(id+"F0.wireOp",EDGE,"E34.13.0"),sQuery(id+"F0.wireOp",EDGE,"E34.14.0"),sQuery(id+"F0.wireOp",EDGE,"E34.15.0"),sQuery(id+"F0.wireOp",EDGE,"E34.16.0"),sQuery(id+"F0.wireOp",EDGE,"E34.17.0"),sQuery(id+"F0.wireOp",EDGE,"E34.18.0"),sQuery(id+"F0.wireOp",EDGE,"E34.19.0"),sQuery(id+"F0.wireOp",EDGE,"E34.20.0"),sQuery(id+"F0.wireOp",EDGE,"E34.21.0"),sQuery(id+"F0.wireOp",EDGE,"E34.22.0"),sQuery(id+"F0.wireOp",EDGE,"E34.23.0"),sQuery(id+"F0.wireOp",EDGE,"E34.24.0"),sQuery(id+"F0.wireOp",EDGE,"E34.25.0"),sQuery(id+"F0.wireOp",EDGE,"E34.26.0"),sQuery(id+"F0.wireOp",EDGE,"E34.27.0"),sQuery(id+"F0.wireOp",EDGE,"E34.28.0"),sQuery(id+"F0.wireOp",EDGE,"E34.29.0"),sQuery(id+"F0.wireOp",EDGE,"E34.30.0"),sQuery(id+"F0.wireOp",EDGE,"E34.31.0"),sQuery(id+"F0.wireOp",EDGE,"E34.32.0"),sQuery(id+"F0.wireOp",EDGE,"E34.33.0"),sQuery(id+"F0.wireOp",EDGE,"E34.34.0"),sQuery(id+"F0.wireOp",EDGE,"E34.35.0"),sQuery(id+"F0.wireOp",EDGE,"E34.36.0"),sQuery(id+"F0.wireOp",EDGE,"E34.37.0"),sQuery(id+"F0.wireOp",EDGE,"E34.38.0"),sQuery(id+"F0.wireOp",EDGE,"E34.39.0"),sQuery(id+"F0.wireOp",EDGE,"E34.40.0"),sQuery(id+"F0.wireOp",EDGE,"E34.41.0"),sQuery(id+"F0.wireOp",EDGE,"E34.42.0"),sQuery(id+"F0.wireOp",EDGE,"E34.43.0"),sQuery(id+"F0.wireOp",EDGE,"E34.44.0"),sQuery(id+"F0.wireOp",EDGE,"E34.45.0"),sQuery(id+"F0.wireOp",EDGE,"E34.46.0"),sQuery(id+"F0.wireOp",EDGE,"E34.47.0"),sQuery(id+"F0.wireOp",EDGE,"E34.48.0"),sQuery(id+"F0.wireOp",EDGE,"E34.49.0"),sQuery(id+"F0.wireOp",EDGE,"E34.50.0"),sQuery(id+"F0.wireOp",EDGE,"E34.51.0"),sQuery(id+"F0.wireOp",EDGE,"E34.52.0"),sQuery(id+"F0.wireOp",EDGE,"E34.53.0"),sQuery(id+"F0.wireOp",EDGE,"E34.54.0"),sQuery(id+"F0.wireOp",EDGE,"E34.55.0"),sQuery(id+"F0.wireOp",EDGE,"E34.56.0"),sQuery(id+"F0.wireOp",EDGE,"E34.57.0"),sQuery(id+"F0.wireOp",EDGE,"E34.58.0"),sQuery(id+"F0.wireOp",EDGE,"E34.59.0")])]}),"instanceName":"1"});
            transform(context, id + "F4", {"entities" : qUnion([Q0]), "transformType" : TransformType.TRANSLATION_3D, "dx" : 0 * mm, "dy" : 0 * mm, "dz" : 0 * mm, "makeCopy" : false});
        }
        {
            var Q0;
            Q0=makeQuery(id+"F1.opExtrude","CAP_EDGE",EDGE,{"disambiguationData":[OSD([sQuery(id+"F0.wireOp",EDGE,"E8")])],"isStart":false});
            var Q1;
            Q1=makeQuery(id+"F3.opPattern","COPY",FACE,{"derivedFrom":makeQuery(id+"F1.opExtrude","CAP_FACE",FACE,{"disambiguationData":[OSD([sQuery(id+"F0.wireOp",EDGE,"E0"),sQuery(id+"F0.wireOp",EDGE,"E1"),sQuery(id+"F0.wireOp",EDGE,"E2"),sQuery(id+"F0.wireOp",EDGE,"E3"),sQuery(id+"F0.wireOp",EDGE,"E4.MirrorCS"),sQuery(id+"F0.wireOp",EDGE,"E5.MirrorCS"),sQuery(id+"F0.wireOp",EDGE,"E6.MirrorCS"),sQuery(id+"F0.wireOp",EDGE,"E7.1.0"),sQuery(id+"F0.wireOp",EDGE,"E7.1.1"),sQuery(id+"F0.wireOp",EDGE,"E7.1.2"),sQuery(id+"F0.wireOp",EDGE,"E7.1.3"),sQuery(id+"F0.wireOp",EDGE,"E7.1.4"),sQuery(id+"F0.wireOp",EDGE,"E7.1.5"),sQuery(id+"F0.wireOp",EDGE,"E7.2.0"),sQuery(id+"F0.wireOp",EDGE,"E7.2.1"),sQuery(id+"F0.wireOp",EDGE,"E7.2.2"),sQuery(id+"F0.wireOp",EDGE,"E7.2.3"),sQuery(id+"F0.wireOp",EDGE,"E7.2.4"),sQuery(id+"F0.wireOp",EDGE,"E7.2.5"),sQuery(id+"F0.wireOp",EDGE,"E7.3.0"),sQuery(id+"F0.wireOp",EDGE,"E7.3.1"),sQuery(id+"F0.wireOp",EDGE,"E7.3.2"),sQuery(id+"F0.wireOp",EDGE,"E7.3.3"),sQuery(id+"F0.wireOp",EDGE,"E7.3.4"),sQuery(id+"F0.wireOp",EDGE,"E7.3.5"),sQuery(id+"F0.wireOp",EDGE,"E7.4.0"),sQuery(id+"F0.wireOp",EDGE,"E7.4.1"),sQuery(id+"F0.wireOp",EDGE,"E7.4.2"),sQuery(id+"F0.wireOp",EDGE,"E7.4.3"),sQuery(id+"F0.wireOp",EDGE,"E7.4.4"),sQuery(id+"F0.wireOp",EDGE,"E7.4.5"),sQuery(id+"F0.wireOp",EDGE,"E7.5.0"),sQuery(id+"F0.wireOp",EDGE,"E7.5.1"),sQuery(id+"F0.wireOp",EDGE,"E7.5.2"),sQuery(id+"F0.wireOp",EDGE,"E7.5.3"),sQuery(id+"F0.wireOp",EDGE,"E7.5.4"),sQuery(id+"F0.wireOp",EDGE,"E7.5.5"),sQuery(id+"F0.wireOp",EDGE,"E7.6.0"),sQuery(id+"F0.wireOp",EDGE,"E7.6.1"),sQuery(id+"F0.wireOp",EDGE,"E7.6.2"),sQuery(id+"F0.wireOp",EDGE,"E7.6.3"),sQuery(id+"F0.wireOp",EDGE,"E7.6.4"),sQuery(id+"F0.wireOp",EDGE,"E7.6.5"),sQuery(id+"F0.wireOp",EDGE,"E7.7.0"),sQuery(id+"F0.wireOp",EDGE,"E7.7.1"),sQuery(id+"F0.wireOp",EDGE,"E7.7.2"),sQuery(id+"F0.wireOp",EDGE,"E7.7.3"),sQuery(id+"F0.wireOp",EDGE,"E7.7.4"),sQuery(id+"F0.wireOp",EDGE,"E7.7.5"),sQuery(id+"F0.wireOp",EDGE,"E7.8.0"),sQuery(id+"F0.wireOp",EDGE,"E7.8.1"),sQuery(id+"F0.wireOp",EDGE,"E7.8.2"),sQuery(id+"F0.wireOp",EDGE,"E7.8.3"),sQuery(id+"F0.wireOp",EDGE,"E7.8.4"),sQuery(id+"F0.wireOp",EDGE,"E7.8.5"),sQuery(id+"F0.wireOp",EDGE,"E7.9.0"),sQuery(id+"F0.wireOp",EDGE,"E7.9.1"),sQuery(id+"F0.wireOp",EDGE,"E7.9.2"),sQuery(id+"F0.wireOp",EDGE,"E7.9.3"),sQuery(id+"F0.wireOp",EDGE,"E7.9.4"),sQuery(id+"F0.wireOp",EDGE,"E7.9.5"),sQuery(id+"F0.wireOp",EDGE,"E7.10.0"),sQuery(id+"F0.wireOp",EDGE,"E7.10.1"),sQuery(id+"F0.wireOp",EDGE,"E7.10.2"),sQuery(id+"F0.wireOp",EDGE,"E7.10.3"),sQuery(id+"F0.wireOp",EDGE,"E7.10.4"),sQuery(id+"F0.wireOp",EDGE,"E7.10.5"),sQuery(id+"F0.wireOp",EDGE,"E7.11.0"),sQuery(id+"F0.wireOp",EDGE,"E7.11.1"),sQuery(id+"F0.wireOp",EDGE,"E7.11.2"),sQuery(id+"F0.wireOp",EDGE,"E7.11.3"),sQuery(id+"F0.wireOp",EDGE,"E7.11.4"),sQuery(id+"F0.wireOp",EDGE,"E7.11.5"),sQuery(id+"F0.wireOp",EDGE,"E7.12.0"),sQuery(id+"F0.wireOp",EDGE,"E7.12.1"),sQuery(id+"F0.wireOp",EDGE,"E7.12.2"),sQuery(id+"F0.wireOp",EDGE,"E7.12.3"),sQuery(id+"F0.wireOp",EDGE,"E7.12.4"),sQuery(id+"F0.wireOp",EDGE,"E7.12.5"),sQuery(id+"F0.wireOp",EDGE,"E7.13.0"),sQuery(id+"F0.wireOp",EDGE,"E7.13.1"),sQuery(id+"F0.wireOp",EDGE,"E7.13.2"),sQuery(id+"F0.wireOp",EDGE,"E7.13.3"),sQuery(id+"F0.wireOp",EDGE,"E7.13.4"),sQuery(id+"F0.wireOp",EDGE,"E7.13.5"),sQuery(id+"F0.wireOp",EDGE,"E7.14.0"),sQuery(id+"F0.wireOp",EDGE,"E7.14.1"),sQuery(id+"F0.wireOp",EDGE,"E7.14.2"),sQuery(id+"F0.wireOp",EDGE,"E7.14.3"),sQuery(id+"F0.wireOp",EDGE,"E7.14.4"),sQuery(id+"F0.wireOp",EDGE,"E7.14.5"),sQuery(id+"F0.wireOp",EDGE,"E7.15.0"),sQuery(id+"F0.wireOp",EDGE,"E7.15.1"),sQuery(id+"F0.wireOp",EDGE,"E7.15.2"),sQuery(id+"F0.wireOp",EDGE,"E7.15.3"),sQuery(id+"F0.wireOp",EDGE,"E7.15.4"),sQuery(id+"F0.wireOp",EDGE,"E7.15.5"),sQuery(id+"F0.wireOp",EDGE,"E7.16.0"),sQuery(id+"F0.wireOp",EDGE,"E7.16.1"),sQuery(id+"F0.wireOp",EDGE,"E7.16.2"),sQuery(id+"F0.wireOp",EDGE,"E7.16.3"),sQuery(id+"F0.wireOp",EDGE,"E7.16.4"),sQuery(id+"F0.wireOp",EDGE,"E7.16.5"),sQuery(id+"F0.wireOp",EDGE,"E7.17.0"),sQuery(id+"F0.wireOp",EDGE,"E7.17.1"),sQuery(id+"F0.wireOp",EDGE,"E7.17.2"),sQuery(id+"F0.wireOp",EDGE,"E7.17.3"),sQuery(id+"F0.wireOp",EDGE,"E7.17.4"),sQuery(id+"F0.wireOp",EDGE,"E7.17.5"),sQuery(id+"F0.wireOp",EDGE,"E7.18.0"),sQuery(id+"F0.wireOp",EDGE,"E7.18.1"),sQuery(id+"F0.wireOp",EDGE,"E7.18.2"),sQuery(id+"F0.wireOp",EDGE,"E7.18.3"),sQuery(id+"F0.wireOp",EDGE,"E7.18.4"),sQuery(id+"F0.wireOp",EDGE,"E7.18.5"),sQuery(id+"F0.wireOp",EDGE,"E7.19.0"),sQuery(id+"F0.wireOp",EDGE,"E7.19.1"),sQuery(id+"F0.wireOp",EDGE,"E7.19.2"),sQuery(id+"F0.wireOp",EDGE,"E7.19.3"),sQuery(id+"F0.wireOp",EDGE,"E7.19.4"),sQuery(id+"F0.wireOp",EDGE,"E7.19.5"),sQuery(id+"F0.wireOp",EDGE,"E7.20.0"),sQuery(id+"F0.wireOp",EDGE,"E7.20.1"),sQuery(id+"F0.wireOp",EDGE,"E7.20.2"),sQuery(id+"F0.wireOp",EDGE,"E7.20.3"),sQuery(id+"F0.wireOp",EDGE,"E7.20.4"),sQuery(id+"F0.wireOp",EDGE,"E7.20.5"),sQuery(id+"F0.wireOp",EDGE,"E7.21.0"),sQuery(id+"F0.wireOp",EDGE,"E7.21.1"),sQuery(id+"F0.wireOp",EDGE,"E7.21.2"),sQuery(id+"F0.wireOp",EDGE,"E7.21.3"),sQuery(id+"F0.wireOp",EDGE,"E7.21.4"),sQuery(id+"F0.wireOp",EDGE,"E7.21.5"),sQuery(id+"F0.wireOp",EDGE,"E7.22.0"),sQuery(id+"F0.wireOp",EDGE,"E7.22.1"),sQuery(id+"F0.wireOp",EDGE,"E7.22.2"),sQuery(id+"F0.wireOp",EDGE,"E7.22.3"),sQuery(id+"F0.wireOp",EDGE,"E7.22.4"),sQuery(id+"F0.wireOp",EDGE,"E7.22.5"),sQuery(id+"F0.wireOp",EDGE,"E7.23.0"),sQuery(id+"F0.wireOp",EDGE,"E7.23.1"),sQuery(id+"F0.wireOp",EDGE,"E7.23.2"),sQuery(id+"F0.wireOp",EDGE,"E7.23.3"),sQuery(id+"F0.wireOp",EDGE,"E7.23.4"),sQuery(id+"F0.wireOp",EDGE,"E7.23.5"),sQuery(id+"F0.wireOp",EDGE,"E7.24.0"),sQuery(id+"F0.wireOp",EDGE,"E7.24.1"),sQuery(id+"F0.wireOp",EDGE,"E7.24.2"),sQuery(id+"F0.wireOp",EDGE,"E7.24.3"),sQuery(id+"F0.wireOp",EDGE,"E7.24.4"),sQuery(id+"F0.wireOp",EDGE,"E7.24.5"),sQuery(id+"F0.wireOp",EDGE,"E7.25.0"),sQuery(id+"F0.wireOp",EDGE,"E7.25.1"),sQuery(id+"F0.wireOp",EDGE,"E7.25.2"),sQuery(id+"F0.wireOp",EDGE,"E7.25.3"),sQuery(id+"F0.wireOp",EDGE,"E7.25.4"),sQuery(id+"F0.wireOp",EDGE,"E7.25.5"),sQuery(id+"F0.wireOp",EDGE,"E7.26.0"),sQuery(id+"F0.wireOp",EDGE,"E7.26.1"),sQuery(id+"F0.wireOp",EDGE,"E7.26.2"),sQuery(id+"F0.wireOp",EDGE,"E7.26.3"),sQuery(id+"F0.wireOp",EDGE,"E7.26.4"),sQuery(id+"F0.wireOp",EDGE,"E7.26.5"),sQuery(id+"F0.wireOp",EDGE,"E7.27.0"),sQuery(id+"F0.wireOp",EDGE,"E7.27.1"),sQuery(id+"F0.wireOp",EDGE,"E7.27.2"),sQuery(id+"F0.wireOp",EDGE,"E7.27.3"),sQuery(id+"F0.wireOp",EDGE,"E7.27.4"),sQuery(id+"F0.wireOp",EDGE,"E7.27.5"),sQuery(id+"F0.wireOp",EDGE,"E7.28.0"),sQuery(id+"F0.wireOp",EDGE,"E7.28.1"),sQuery(id+"F0.wireOp",EDGE,"E7.28.2"),sQuery(id+"F0.wireOp",EDGE,"E7.28.3"),sQuery(id+"F0.wireOp",EDGE,"E7.28.4"),sQuery(id+"F0.wireOp",EDGE,"E7.28.5"),sQuery(id+"F0.wireOp",EDGE,"E7.29.0"),sQuery(id+"F0.wireOp",EDGE,"E7.29.1"),sQuery(id+"F0.wireOp",EDGE,"E7.29.2"),sQuery(id+"F0.wireOp",EDGE,"E7.29.3"),sQuery(id+"F0.wireOp",EDGE,"E7.29.4"),sQuery(id+"F0.wireOp",EDGE,"E7.29.5"),sQuery(id+"F0.wireOp",EDGE,"E7.30.0"),sQuery(id+"F0.wireOp",EDGE,"E7.30.1"),sQuery(id+"F0.wireOp",EDGE,"E7.30.2"),sQuery(id+"F0.wireOp",EDGE,"E7.30.3"),sQuery(id+"F0.wireOp",EDGE,"E7.30.4"),sQuery(id+"F0.wireOp",EDGE,"E7.30.5"),sQuery(id+"F0.wireOp",EDGE,"E7.31.0"),sQuery(id+"F0.wireOp",EDGE,"E7.31.1"),sQuery(id+"F0.wireOp",EDGE,"E7.31.2"),sQuery(id+"F0.wireOp",EDGE,"E7.31.3"),sQuery(id+"F0.wireOp",EDGE,"E7.31.4"),sQuery(id+"F0.wireOp",EDGE,"E7.31.5"),sQuery(id+"F0.wireOp",EDGE,"E7.32.0"),sQuery(id+"F0.wireOp",EDGE,"E7.32.1"),sQuery(id+"F0.wireOp",EDGE,"E7.32.2"),sQuery(id+"F0.wireOp",EDGE,"E7.32.3"),sQuery(id+"F0.wireOp",EDGE,"E7.32.4"),sQuery(id+"F0.wireOp",EDGE,"E7.32.5"),sQuery(id+"F0.wireOp",EDGE,"E7.33.0"),sQuery(id+"F0.wireOp",EDGE,"E7.33.1"),sQuery(id+"F0.wireOp",EDGE,"E7.33.2"),sQuery(id+"F0.wireOp",EDGE,"E7.33.3"),sQuery(id+"F0.wireOp",EDGE,"E7.33.4"),sQuery(id+"F0.wireOp",EDGE,"E7.33.5"),sQuery(id+"F0.wireOp",EDGE,"E7.34.0"),sQuery(id+"F0.wireOp",EDGE,"E7.34.1"),sQuery(id+"F0.wireOp",EDGE,"E7.34.2"),sQuery(id+"F0.wireOp",EDGE,"E7.34.3"),sQuery(id+"F0.wireOp",EDGE,"E7.34.4"),sQuery(id+"F0.wireOp",EDGE,"E7.34.5"),sQuery(id+"F0.wireOp",EDGE,"E7.35.0"),sQuery(id+"F0.wireOp",EDGE,"E7.35.1"),sQuery(id+"F0.wireOp",EDGE,"E7.35.2"),sQuery(id+"F0.wireOp",EDGE,"E7.35.3"),sQuery(id+"F0.wireOp",EDGE,"E7.35.4"),sQuery(id+"F0.wireOp",EDGE,"E7.35.5"),sQuery(id+"F0.wireOp",EDGE,"E7.36.0"),sQuery(id+"F0.wireOp",EDGE,"E7.36.1"),sQuery(id+"F0.wireOp",EDGE,"E7.36.2"),sQuery(id+"F0.wireOp",EDGE,"E7.36.3"),sQuery(id+"F0.wireOp",EDGE,"E7.36.4"),sQuery(id+"F0.wireOp",EDGE,"E7.36.5"),sQuery(id+"F0.wireOp",EDGE,"E7.37.0"),sQuery(id+"F0.wireOp",EDGE,"E7.37.1"),sQuery(id+"F0.wireOp",EDGE,"E7.37.2"),sQuery(id+"F0.wireOp",EDGE,"E7.37.3"),sQuery(id+"F0.wireOp",EDGE,"E7.37.4"),sQuery(id+"F0.wireOp",EDGE,"E7.37.5"),sQuery(id+"F0.wireOp",EDGE,"E7.38.0"),sQuery(id+"F0.wireOp",EDGE,"E7.38.1"),sQuery(id+"F0.wireOp",EDGE,"E7.38.2"),sQuery(id+"F0.wireOp",EDGE,"E7.38.3"),sQuery(id+"F0.wireOp",EDGE,"E7.38.4"),sQuery(id+"F0.wireOp",EDGE,"E7.38.5"),sQuery(id+"F0.wireOp",EDGE,"E7.39.0"),sQuery(id+"F0.wireOp",EDGE,"E7.39.1"),sQuery(id+"F0.wireOp",EDGE,"E7.39.2"),sQuery(id+"F0.wireOp",EDGE,"E7.39.3"),sQuery(id+"F0.wireOp",EDGE,"E7.39.4"),sQuery(id+"F0.wireOp",EDGE,"E7.39.5"),sQuery(id+"F0.wireOp",EDGE,"E7.40.0"),sQuery(id+"F0.wireOp",EDGE,"E7.40.1"),sQuery(id+"F0.wireOp",EDGE,"E7.40.2"),sQuery(id+"F0.wireOp",EDGE,"E7.40.3"),sQuery(id+"F0.wireOp",EDGE,"E7.40.4"),sQuery(id+"F0.wireOp",EDGE,"E7.40.5"),sQuery(id+"F0.wireOp",EDGE,"E7.41.0"),sQuery(id+"F0.wireOp",EDGE,"E7.41.1"),sQuery(id+"F0.wireOp",EDGE,"E7.41.2"),sQuery(id+"F0.wireOp",EDGE,"E7.41.3"),sQuery(id+"F0.wireOp",EDGE,"E7.41.4"),sQuery(id+"F0.wireOp",EDGE,"E7.41.5"),sQuery(id+"F0.wireOp",EDGE,"E7.42.0"),sQuery(id+"F0.wireOp",EDGE,"E7.42.1"),sQuery(id+"F0.wireOp",EDGE,"E7.42.2"),sQuery(id+"F0.wireOp",EDGE,"E7.42.3"),sQuery(id+"F0.wireOp",EDGE,"E7.42.4"),sQuery(id+"F0.wireOp",EDGE,"E7.42.5"),sQuery(id+"F0.wireOp",EDGE,"E7.43.0"),sQuery(id+"F0.wireOp",EDGE,"E7.43.1"),sQuery(id+"F0.wireOp",EDGE,"E7.43.2"),sQuery(id+"F0.wireOp",EDGE,"E7.43.3"),sQuery(id+"F0.wireOp",EDGE,"E7.43.4"),sQuery(id+"F0.wireOp",EDGE,"E7.43.5"),sQuery(id+"F0.wireOp",EDGE,"E7.44.0"),sQuery(id+"F0.wireOp",EDGE,"E7.44.1"),sQuery(id+"F0.wireOp",EDGE,"E7.44.2"),sQuery(id+"F0.wireOp",EDGE,"E7.44.3"),sQuery(id+"F0.wireOp",EDGE,"E7.44.4"),sQuery(id+"F0.wireOp",EDGE,"E7.44.5"),sQuery(id+"F0.wireOp",EDGE,"E7.45.0"),sQuery(id+"F0.wireOp",EDGE,"E7.45.1"),sQuery(id+"F0.wireOp",EDGE,"E7.45.2"),sQuery(id+"F0.wireOp",EDGE,"E7.45.3"),sQuery(id+"F0.wireOp",EDGE,"E7.45.4"),sQuery(id+"F0.wireOp",EDGE,"E7.45.5"),sQuery(id+"F0.wireOp",EDGE,"E7.46.0"),sQuery(id+"F0.wireOp",EDGE,"E7.46.1"),sQuery(id+"F0.wireOp",EDGE,"E7.46.2"),sQuery(id+"F0.wireOp",EDGE,"E7.46.3"),sQuery(id+"F0.wireOp",EDGE,"E7.46.4"),sQuery(id+"F0.wireOp",EDGE,"E7.46.5"),sQuery(id+"F0.wireOp",EDGE,"E7.47.0"),sQuery(id+"F0.wireOp",EDGE,"E7.47.1"),sQuery(id+"F0.wireOp",EDGE,"E7.47.2"),sQuery(id+"F0.wireOp",EDGE,"E7.47.3"),sQuery(id+"F0.wireOp",EDGE,"E7.47.4"),sQuery(id+"F0.wireOp",EDGE,"E7.47.5"),sQuery(id+"F0.wireOp",EDGE,"E7.48.0"),sQuery(id+"F0.wireOp",EDGE,"E7.48.1"),sQuery(id+"F0.wireOp",EDGE,"E7.48.2"),sQuery(id+"F0.wireOp",EDGE,"E7.48.3"),sQuery(id+"F0.wireOp",EDGE,"E7.48.4"),sQuery(id+"F0.wireOp",EDGE,"E7.48.5"),sQuery(id+"F0.wireOp",EDGE,"E7.49.0"),sQuery(id+"F0.wireOp",EDGE,"E7.49.1"),sQuery(id+"F0.wireOp",EDGE,"E7.49.2"),sQuery(id+"F0.wireOp",EDGE,"E7.49.3"),sQuery(id+"F0.wireOp",EDGE,"E7.49.4"),sQuery(id+"F0.wireOp",EDGE,"E7.49.5"),sQuery(id+"F0.wireOp",EDGE,"E7.50.0"),sQuery(id+"F0.wireOp",EDGE,"E7.50.1"),sQuery(id+"F0.wireOp",EDGE,"E7.50.2"),sQuery(id+"F0.wireOp",EDGE,"E7.50.3"),sQuery(id+"F0.wireOp",EDGE,"E7.50.4"),sQuery(id+"F0.wireOp",EDGE,"E7.50.5"),sQuery(id+"F0.wireOp",EDGE,"E7.51.0"),sQuery(id+"F0.wireOp",EDGE,"E7.51.1"),sQuery(id+"F0.wireOp",EDGE,"E7.51.2"),sQuery(id+"F0.wireOp",EDGE,"E7.51.3"),sQuery(id+"F0.wireOp",EDGE,"E7.51.4"),sQuery(id+"F0.wireOp",EDGE,"E7.51.5"),sQuery(id+"F0.wireOp",EDGE,"E7.52.0"),sQuery(id+"F0.wireOp",EDGE,"E7.52.1"),sQuery(id+"F0.wireOp",EDGE,"E7.52.2"),sQuery(id+"F0.wireOp",EDGE,"E7.52.3"),sQuery(id+"F0.wireOp",EDGE,"E7.52.4"),sQuery(id+"F0.wireOp",EDGE,"E7.52.5"),sQuery(id+"F0.wireOp",EDGE,"E7.53.0"),sQuery(id+"F0.wireOp",EDGE,"E7.53.1"),sQuery(id+"F0.wireOp",EDGE,"E7.53.2"),sQuery(id+"F0.wireOp",EDGE,"E7.53.3"),sQuery(id+"F0.wireOp",EDGE,"E7.53.4"),sQuery(id+"F0.wireOp",EDGE,"E7.53.5"),sQuery(id+"F0.wireOp",EDGE,"E7.54.0"),sQuery(id+"F0.wireOp",EDGE,"E7.54.1"),sQuery(id+"F0.wireOp",EDGE,"E7.54.2"),sQuery(id+"F0.wireOp",EDGE,"E7.54.3"),sQuery(id+"F0.wireOp",EDGE,"E7.54.4"),sQuery(id+"F0.wireOp",EDGE,"E7.54.5"),sQuery(id+"F0.wireOp",EDGE,"E7.55.0"),sQuery(id+"F0.wireOp",EDGE,"E7.55.1"),sQuery(id+"F0.wireOp",EDGE,"E7.55.2"),sQuery(id+"F0.wireOp",EDGE,"E7.55.3"),sQuery(id+"F0.wireOp",EDGE,"E7.55.4"),sQuery(id+"F0.wireOp",EDGE,"E7.55.5"),sQuery(id+"F0.wireOp",EDGE,"E7.56.0"),sQuery(id+"F0.wireOp",EDGE,"E7.56.1"),sQuery(id+"F0.wireOp",EDGE,"E7.56.2"),sQuery(id+"F0.wireOp",EDGE,"E7.56.3"),sQuery(id+"F0.wireOp",EDGE,"E7.56.4"),sQuery(id+"F0.wireOp",EDGE,"E7.56.5"),sQuery(id+"F0.wireOp",EDGE,"E7.57.0"),sQuery(id+"F0.wireOp",EDGE,"E7.57.1"),sQuery(id+"F0.wireOp",EDGE,"E7.57.2"),sQuery(id+"F0.wireOp",EDGE,"E7.57.3"),sQuery(id+"F0.wireOp",EDGE,"E7.57.4"),sQuery(id+"F0.wireOp",EDGE,"E7.57.5"),sQuery(id+"F0.wireOp",EDGE,"E7.58.0"),sQuery(id+"F0.wireOp",EDGE,"E7.58.1"),sQuery(id+"F0.wireOp",EDGE,"E7.58.2"),sQuery(id+"F0.wireOp",EDGE,"E7.58.3"),sQuery(id+"F0.wireOp",EDGE,"E7.58.4"),sQuery(id+"F0.wireOp",EDGE,"E7.58.5"),sQuery(id+"F0.wireOp",EDGE,"E7.59.0"),sQuery(id+"F0.wireOp",EDGE,"E7.59.1"),sQuery(id+"F0.wireOp",EDGE,"E7.59.2"),sQuery(id+"F0.wireOp",EDGE,"E7.59.3"),sQuery(id+"F0.wireOp",EDGE,"E7.59.4"),sQuery(id+"F0.wireOp",EDGE,"E7.59.5"),sQuery(id+"F0.wireOp",EDGE,"E8"),sQuery(id+"F0.wireOp",EDGE,"E9"),sQuery(id+"F0.wireOp",EDGE,"E10"),sQuery(id+"F0.wireOp",EDGE,"E11.filletArc"),sQuery(id+"F0.wireOp",EDGE,"E12.filletArc"),sQuery(id+"F0.wireOp",EDGE,"E13.filletArc"),sQuery(id+"F0.wireOp",EDGE,"E14.MirrorCS"),sQuery(id+"F0.wireOp",EDGE,"E15.MirrorCS"),sQuery(id+"F0.wireOp",EDGE,"E16.MirrorCS"),sQuery(id+"F0.wireOp",EDGE,"E17.MirrorCS"),sQuery(id+"F0.wireOp",EDGE,"E18.MirrorCS"),sQuery(id+"F0.wireOp",EDGE,"E19.MirrorCS"),sQuery(id+"F0.wireOp",EDGE,"E21.MirrorCS"),sQuery(id+"F0.wireOp",EDGE,"E22.MirrorCS"),sQuery(id+"F0.wireOp",EDGE,"E23.MirrorCS"),sQuery(id+"F0.wireOp",EDGE,"E24.MirrorCS"),sQuery(id+"F0.wireOp",EDGE,"E25.MirrorCS"),sQuery(id+"F0.wireOp",EDGE,"E20.MirrorCS"),sQuery(id+"F0.wireOp",EDGE,"E27.MirrorCS"),sQuery(id+"F0.wireOp",EDGE,"E28.MirrorCS"),sQuery(id+"F0.wireOp",EDGE,"E29.MirrorCS"),sQuery(id+"F0.wireOp",EDGE,"E30.MirrorCS"),sQuery(id+"F0.wireOp",EDGE,"E31.MirrorCS"),sQuery(id+"F0.wireOp",EDGE,"E32.MirrorCS"),sQuery(id+"F0.wireOp",EDGE,"E33"),sQuery(id+"F0.wireOp",EDGE,"E34.1.0"),sQuery(id+"F0.wireOp",EDGE,"E34.2.0"),sQuery(id+"F0.wireOp",EDGE,"E34.3.0"),sQuery(id+"F0.wireOp",EDGE,"E34.4.0"),sQuery(id+"F0.wireOp",EDGE,"E34.5.0"),sQuery(id+"F0.wireOp",EDGE,"E34.6.0"),sQuery(id+"F0.wireOp",EDGE,"E34.7.0"),sQuery(id+"F0.wireOp",EDGE,"E34.8.0"),sQuery(id+"F0.wireOp",EDGE,"E34.9.0"),sQuery(id+"F0.wireOp",EDGE,"E34.10.0"),sQuery(id+"F0.wireOp",EDGE,"E34.11.0"),sQuery(id+"F0.wireOp",EDGE,"E34.12.0"),sQuery(id+"F0.wireOp",EDGE,"E34.13.0"),sQuery(id+"F0.wireOp",EDGE,"E34.14.0"),sQuery(id+"F0.wireOp",EDGE,"E34.15.0"),sQuery(id+"F0.wireOp",EDGE,"E34.16.0"),sQuery(id+"F0.wireOp",EDGE,"E34.17.0"),sQuery(id+"F0.wireOp",EDGE,"E34.18.0"),sQuery(id+"F0.wireOp",EDGE,"E34.19.0"),sQuery(id+"F0.wireOp",EDGE,"E34.20.0"),sQuery(id+"F0.wireOp",EDGE,"E34.21.0"),sQuery(id+"F0.wireOp",EDGE,"E34.22.0"),sQuery(id+"F0.wireOp",EDGE,"E34.23.0"),sQuery(id+"F0.wireOp",EDGE,"E34.24.0"),sQuery(id+"F0.wireOp",EDGE,"E34.25.0"),sQuery(id+"F0.wireOp",EDGE,"E34.26.0"),sQuery(id+"F0.wireOp",EDGE,"E34.27.0"),sQuery(id+"F0.wireOp",EDGE,"E34.28.0"),sQuery(id+"F0.wireOp",EDGE,"E34.29.0"),sQuery(id+"F0.wireOp",EDGE,"E34.30.0"),sQuery(id+"F0.wireOp",EDGE,"E34.31.0"),sQuery(id+"F0.wireOp",EDGE,"E34.32.0"),sQuery(id+"F0.wireOp",EDGE,"E34.33.0"),sQuery(id+"F0.wireOp",EDGE,"E34.34.0"),sQuery(id+"F0.wireOp",EDGE,"E34.35.0"),sQuery(id+"F0.wireOp",EDGE,"E34.36.0"),sQuery(id+"F0.wireOp",EDGE,"E34.37.0"),sQuery(id+"F0.wireOp",EDGE,"E34.38.0"),sQuery(id+"F0.wireOp",EDGE,"E34.39.0"),sQuery(id+"F0.wireOp",EDGE,"E34.40.0"),sQuery(id+"F0.wireOp",EDGE,"E34.41.0"),sQuery(id+"F0.wireOp",EDGE,"E34.42.0"),sQuery(id+"F0.wireOp",EDGE,"E34.43.0"),sQuery(id+"F0.wireOp",EDGE,"E34.44.0"),sQuery(id+"F0.wireOp",EDGE,"E34.45.0"),sQuery(id+"F0.wireOp",EDGE,"E34.46.0"),sQuery(id+"F0.wireOp",EDGE,"E34.47.0"),sQuery(id+"F0.wireOp",EDGE,"E34.48.0"),sQuery(id+"F0.wireOp",EDGE,"E34.49.0"),sQuery(id+"F0.wireOp",EDGE,"E34.50.0"),sQuery(id+"F0.wireOp",EDGE,"E34.51.0"),sQuery(id+"F0.wireOp",EDGE,"E34.52.0"),sQuery(id+"F0.wireOp",EDGE,"E34.53.0"),sQuery(id+"F0.wireOp",EDGE,"E34.54.0"),sQuery(id+"F0.wireOp",EDGE,"E34.55.0"),sQuery(id+"F0.wireOp",EDGE,"E34.56.0"),sQuery(id+"F0.wireOp",EDGE,"E34.57.0"),sQuery(id+"F0.wireOp",EDGE,"E34.58.0"),sQuery(id+"F0.wireOp",EDGE,"E34.59.0")])],"isStart":false}),"instanceName":"1"});
            var Q2;
            Q2=makeQuery(id+"F1.opExtrude","CAP_FACE",FACE,{"disambiguationData":[OSD([sQuery(id+"F0.wireOp",EDGE,"E0"),sQuery(id+"F0.wireOp",EDGE,"E1"),sQuery(id+"F0.wireOp",EDGE,"E2"),sQuery(id+"F0.wireOp",EDGE,"E3"),sQuery(id+"F0.wireOp",EDGE,"E4.MirrorCS"),sQuery(id+"F0.wireOp",EDGE,"E5.MirrorCS"),sQuery(id+"F0.wireOp",EDGE,"E6.MirrorCS"),sQuery(id+"F0.wireOp",EDGE,"E7.1.0"),sQuery(id+"F0.wireOp",EDGE,"E7.1.1"),sQuery(id+"F0.wireOp",EDGE,"E7.1.2"),sQuery(id+"F0.wireOp",EDGE,"E7.1.3"),sQuery(id+"F0.wireOp",EDGE,"E7.1.4"),sQuery(id+"F0.wireOp",EDGE,"E7.1.5"),sQuery(id+"F0.wireOp",EDGE,"E7.2.0"),sQuery(id+"F0.wireOp",EDGE,"E7.2.1"),sQuery(id+"F0.wireOp",EDGE,"E7.2.2"),sQuery(id+"F0.wireOp",EDGE,"E7.2.3"),sQuery(id+"F0.wireOp",EDGE,"E7.2.4"),sQuery(id+"F0.wireOp",EDGE,"E7.2.5"),sQuery(id+"F0.wireOp",EDGE,"E7.3.0"),sQuery(id+"F0.wireOp",EDGE,"E7.3.1"),sQuery(id+"F0.wireOp",EDGE,"E7.3.2"),sQuery(id+"F0.wireOp",EDGE,"E7.3.3"),sQuery(id+"F0.wireOp",EDGE,"E7.3.4"),sQuery(id+"F0.wireOp",EDGE,"E7.3.5"),sQuery(id+"F0.wireOp",EDGE,"E7.4.0"),sQuery(id+"F0.wireOp",EDGE,"E7.4.1"),sQuery(id+"F0.wireOp",EDGE,"E7.4.2"),sQuery(id+"F0.wireOp",EDGE,"E7.4.3"),sQuery(id+"F0.wireOp",EDGE,"E7.4.4"),sQuery(id+"F0.wireOp",EDGE,"E7.4.5"),sQuery(id+"F0.wireOp",EDGE,"E7.5.0"),sQuery(id+"F0.wireOp",EDGE,"E7.5.1"),sQuery(id+"F0.wireOp",EDGE,"E7.5.2"),sQuery(id+"F0.wireOp",EDGE,"E7.5.3"),sQuery(id+"F0.wireOp",EDGE,"E7.5.4"),sQuery(id+"F0.wireOp",EDGE,"E7.5.5"),sQuery(id+"F0.wireOp",EDGE,"E7.6.0"),sQuery(id+"F0.wireOp",EDGE,"E7.6.1"),sQuery(id+"F0.wireOp",EDGE,"E7.6.2"),sQuery(id+"F0.wireOp",EDGE,"E7.6.3"),sQuery(id+"F0.wireOp",EDGE,"E7.6.4"),sQuery(id+"F0.wireOp",EDGE,"E7.6.5"),sQuery(id+"F0.wireOp",EDGE,"E7.7.0"),sQuery(id+"F0.wireOp",EDGE,"E7.7.1"),sQuery(id+"F0.wireOp",EDGE,"E7.7.2"),sQuery(id+"F0.wireOp",EDGE,"E7.7.3"),sQuery(id+"F0.wireOp",EDGE,"E7.7.4"),sQuery(id+"F0.wireOp",EDGE,"E7.7.5"),sQuery(id+"F0.wireOp",EDGE,"E7.8.0"),sQuery(id+"F0.wireOp",EDGE,"E7.8.1"),sQuery(id+"F0.wireOp",EDGE,"E7.8.2"),sQuery(id+"F0.wireOp",EDGE,"E7.8.3"),sQuery(id+"F0.wireOp",EDGE,"E7.8.4"),sQuery(id+"F0.wireOp",EDGE,"E7.8.5"),sQuery(id+"F0.wireOp",EDGE,"E7.9.0"),sQuery(id+"F0.wireOp",EDGE,"E7.9.1"),sQuery(id+"F0.wireOp",EDGE,"E7.9.2"),sQuery(id+"F0.wireOp",EDGE,"E7.9.3"),sQuery(id+"F0.wireOp",EDGE,"E7.9.4"),sQuery(id+"F0.wireOp",EDGE,"E7.9.5"),sQuery(id+"F0.wireOp",EDGE,"E7.10.0"),sQuery(id+"F0.wireOp",EDGE,"E7.10.1"),sQuery(id+"F0.wireOp",EDGE,"E7.10.2"),sQuery(id+"F0.wireOp",EDGE,"E7.10.3"),sQuery(id+"F0.wireOp",EDGE,"E7.10.4"),sQuery(id+"F0.wireOp",EDGE,"E7.10.5"),sQuery(id+"F0.wireOp",EDGE,"E7.11.0"),sQuery(id+"F0.wireOp",EDGE,"E7.11.1"),sQuery(id+"F0.wireOp",EDGE,"E7.11.2"),sQuery(id+"F0.wireOp",EDGE,"E7.11.3"),sQuery(id+"F0.wireOp",EDGE,"E7.11.4"),sQuery(id+"F0.wireOp",EDGE,"E7.11.5"),sQuery(id+"F0.wireOp",EDGE,"E7.12.0"),sQuery(id+"F0.wireOp",EDGE,"E7.12.1"),sQuery(id+"F0.wireOp",EDGE,"E7.12.2"),sQuery(id+"F0.wireOp",EDGE,"E7.12.3"),sQuery(id+"F0.wireOp",EDGE,"E7.12.4"),sQuery(id+"F0.wireOp",EDGE,"E7.12.5"),sQuery(id+"F0.wireOp",EDGE,"E7.13.0"),sQuery(id+"F0.wireOp",EDGE,"E7.13.1"),sQuery(id+"F0.wireOp",EDGE,"E7.13.2"),sQuery(id+"F0.wireOp",EDGE,"E7.13.3"),sQuery(id+"F0.wireOp",EDGE,"E7.13.4"),sQuery(id+"F0.wireOp",EDGE,"E7.13.5"),sQuery(id+"F0.wireOp",EDGE,"E7.14.0"),sQuery(id+"F0.wireOp",EDGE,"E7.14.1"),sQuery(id+"F0.wireOp",EDGE,"E7.14.2"),sQuery(id+"F0.wireOp",EDGE,"E7.14.3"),sQuery(id+"F0.wireOp",EDGE,"E7.14.4"),sQuery(id+"F0.wireOp",EDGE,"E7.14.5"),sQuery(id+"F0.wireOp",EDGE,"E7.15.0"),sQuery(id+"F0.wireOp",EDGE,"E7.15.1"),sQuery(id+"F0.wireOp",EDGE,"E7.15.2"),sQuery(id+"F0.wireOp",EDGE,"E7.15.3"),sQuery(id+"F0.wireOp",EDGE,"E7.15.4"),sQuery(id+"F0.wireOp",EDGE,"E7.15.5"),sQuery(id+"F0.wireOp",EDGE,"E7.16.0"),sQuery(id+"F0.wireOp",EDGE,"E7.16.1"),sQuery(id+"F0.wireOp",EDGE,"E7.16.2"),sQuery(id+"F0.wireOp",EDGE,"E7.16.3"),sQuery(id+"F0.wireOp",EDGE,"E7.16.4"),sQuery(id+"F0.wireOp",EDGE,"E7.16.5"),sQuery(id+"F0.wireOp",EDGE,"E7.17.0"),sQuery(id+"F0.wireOp",EDGE,"E7.17.1"),sQuery(id+"F0.wireOp",EDGE,"E7.17.2"),sQuery(id+"F0.wireOp",EDGE,"E7.17.3"),sQuery(id+"F0.wireOp",EDGE,"E7.17.4"),sQuery(id+"F0.wireOp",EDGE,"E7.17.5"),sQuery(id+"F0.wireOp",EDGE,"E7.18.0"),sQuery(id+"F0.wireOp",EDGE,"E7.18.1"),sQuery(id+"F0.wireOp",EDGE,"E7.18.2"),sQuery(id+"F0.wireOp",EDGE,"E7.18.3"),sQuery(id+"F0.wireOp",EDGE,"E7.18.4"),sQuery(id+"F0.wireOp",EDGE,"E7.18.5"),sQuery(id+"F0.wireOp",EDGE,"E7.19.0"),sQuery(id+"F0.wireOp",EDGE,"E7.19.1"),sQuery(id+"F0.wireOp",EDGE,"E7.19.2"),sQuery(id+"F0.wireOp",EDGE,"E7.19.3"),sQuery(id+"F0.wireOp",EDGE,"E7.19.4"),sQuery(id+"F0.wireOp",EDGE,"E7.19.5"),sQuery(id+"F0.wireOp",EDGE,"E7.20.0"),sQuery(id+"F0.wireOp",EDGE,"E7.20.1"),sQuery(id+"F0.wireOp",EDGE,"E7.20.2"),sQuery(id+"F0.wireOp",EDGE,"E7.20.3"),sQuery(id+"F0.wireOp",EDGE,"E7.20.4"),sQuery(id+"F0.wireOp",EDGE,"E7.20.5"),sQuery(id+"F0.wireOp",EDGE,"E7.21.0"),sQuery(id+"F0.wireOp",EDGE,"E7.21.1"),sQuery(id+"F0.wireOp",EDGE,"E7.21.2"),sQuery(id+"F0.wireOp",EDGE,"E7.21.3"),sQuery(id+"F0.wireOp",EDGE,"E7.21.4"),sQuery(id+"F0.wireOp",EDGE,"E7.21.5"),sQuery(id+"F0.wireOp",EDGE,"E7.22.0"),sQuery(id+"F0.wireOp",EDGE,"E7.22.1"),sQuery(id+"F0.wireOp",EDGE,"E7.22.2"),sQuery(id+"F0.wireOp",EDGE,"E7.22.3"),sQuery(id+"F0.wireOp",EDGE,"E7.22.4"),sQuery(id+"F0.wireOp",EDGE,"E7.22.5"),sQuery(id+"F0.wireOp",EDGE,"E7.23.0"),sQuery(id+"F0.wireOp",EDGE,"E7.23.1"),sQuery(id+"F0.wireOp",EDGE,"E7.23.2"),sQuery(id+"F0.wireOp",EDGE,"E7.23.3"),sQuery(id+"F0.wireOp",EDGE,"E7.23.4"),sQuery(id+"F0.wireOp",EDGE,"E7.23.5"),sQuery(id+"F0.wireOp",EDGE,"E7.24.0"),sQuery(id+"F0.wireOp",EDGE,"E7.24.1"),sQuery(id+"F0.wireOp",EDGE,"E7.24.2"),sQuery(id+"F0.wireOp",EDGE,"E7.24.3"),sQuery(id+"F0.wireOp",EDGE,"E7.24.4"),sQuery(id+"F0.wireOp",EDGE,"E7.24.5"),sQuery(id+"F0.wireOp",EDGE,"E7.25.0"),sQuery(id+"F0.wireOp",EDGE,"E7.25.1"),sQuery(id+"F0.wireOp",EDGE,"E7.25.2"),sQuery(id+"F0.wireOp",EDGE,"E7.25.3"),sQuery(id+"F0.wireOp",EDGE,"E7.25.4"),sQuery(id+"F0.wireOp",EDGE,"E7.25.5"),sQuery(id+"F0.wireOp",EDGE,"E7.26.0"),sQuery(id+"F0.wireOp",EDGE,"E7.26.1"),sQuery(id+"F0.wireOp",EDGE,"E7.26.2"),sQuery(id+"F0.wireOp",EDGE,"E7.26.3"),sQuery(id+"F0.wireOp",EDGE,"E7.26.4"),sQuery(id+"F0.wireOp",EDGE,"E7.26.5"),sQuery(id+"F0.wireOp",EDGE,"E7.27.0"),sQuery(id+"F0.wireOp",EDGE,"E7.27.1"),sQuery(id+"F0.wireOp",EDGE,"E7.27.2"),sQuery(id+"F0.wireOp",EDGE,"E7.27.3"),sQuery(id+"F0.wireOp",EDGE,"E7.27.4"),sQuery(id+"F0.wireOp",EDGE,"E7.27.5"),sQuery(id+"F0.wireOp",EDGE,"E7.28.0"),sQuery(id+"F0.wireOp",EDGE,"E7.28.1"),sQuery(id+"F0.wireOp",EDGE,"E7.28.2"),sQuery(id+"F0.wireOp",EDGE,"E7.28.3"),sQuery(id+"F0.wireOp",EDGE,"E7.28.4"),sQuery(id+"F0.wireOp",EDGE,"E7.28.5"),sQuery(id+"F0.wireOp",EDGE,"E7.29.0"),sQuery(id+"F0.wireOp",EDGE,"E7.29.1"),sQuery(id+"F0.wireOp",EDGE,"E7.29.2"),sQuery(id+"F0.wireOp",EDGE,"E7.29.3"),sQuery(id+"F0.wireOp",EDGE,"E7.29.4"),sQuery(id+"F0.wireOp",EDGE,"E7.29.5"),sQuery(id+"F0.wireOp",EDGE,"E7.30.0"),sQuery(id+"F0.wireOp",EDGE,"E7.30.1"),sQuery(id+"F0.wireOp",EDGE,"E7.30.2"),sQuery(id+"F0.wireOp",EDGE,"E7.30.3"),sQuery(id+"F0.wireOp",EDGE,"E7.30.4"),sQuery(id+"F0.wireOp",EDGE,"E7.30.5"),sQuery(id+"F0.wireOp",EDGE,"E7.31.0"),sQuery(id+"F0.wireOp",EDGE,"E7.31.1"),sQuery(id+"F0.wireOp",EDGE,"E7.31.2"),sQuery(id+"F0.wireOp",EDGE,"E7.31.3"),sQuery(id+"F0.wireOp",EDGE,"E7.31.4"),sQuery(id+"F0.wireOp",EDGE,"E7.31.5"),sQuery(id+"F0.wireOp",EDGE,"E7.32.0"),sQuery(id+"F0.wireOp",EDGE,"E7.32.1"),sQuery(id+"F0.wireOp",EDGE,"E7.32.2"),sQuery(id+"F0.wireOp",EDGE,"E7.32.3"),sQuery(id+"F0.wireOp",EDGE,"E7.32.4"),sQuery(id+"F0.wireOp",EDGE,"E7.32.5"),sQuery(id+"F0.wireOp",EDGE,"E7.33.0"),sQuery(id+"F0.wireOp",EDGE,"E7.33.1"),sQuery(id+"F0.wireOp",EDGE,"E7.33.2"),sQuery(id+"F0.wireOp",EDGE,"E7.33.3"),sQuery(id+"F0.wireOp",EDGE,"E7.33.4"),sQuery(id+"F0.wireOp",EDGE,"E7.33.5"),sQuery(id+"F0.wireOp",EDGE,"E7.34.0"),sQuery(id+"F0.wireOp",EDGE,"E7.34.1"),sQuery(id+"F0.wireOp",EDGE,"E7.34.2"),sQuery(id+"F0.wireOp",EDGE,"E7.34.3"),sQuery(id+"F0.wireOp",EDGE,"E7.34.4"),sQuery(id+"F0.wireOp",EDGE,"E7.34.5"),sQuery(id+"F0.wireOp",EDGE,"E7.35.0"),sQuery(id+"F0.wireOp",EDGE,"E7.35.1"),sQuery(id+"F0.wireOp",EDGE,"E7.35.2"),sQuery(id+"F0.wireOp",EDGE,"E7.35.3"),sQuery(id+"F0.wireOp",EDGE,"E7.35.4"),sQuery(id+"F0.wireOp",EDGE,"E7.35.5"),sQuery(id+"F0.wireOp",EDGE,"E7.36.0"),sQuery(id+"F0.wireOp",EDGE,"E7.36.1"),sQuery(id+"F0.wireOp",EDGE,"E7.36.2"),sQuery(id+"F0.wireOp",EDGE,"E7.36.3"),sQuery(id+"F0.wireOp",EDGE,"E7.36.4"),sQuery(id+"F0.wireOp",EDGE,"E7.36.5"),sQuery(id+"F0.wireOp",EDGE,"E7.37.0"),sQuery(id+"F0.wireOp",EDGE,"E7.37.1"),sQuery(id+"F0.wireOp",EDGE,"E7.37.2"),sQuery(id+"F0.wireOp",EDGE,"E7.37.3"),sQuery(id+"F0.wireOp",EDGE,"E7.37.4"),sQuery(id+"F0.wireOp",EDGE,"E7.37.5"),sQuery(id+"F0.wireOp",EDGE,"E7.38.0"),sQuery(id+"F0.wireOp",EDGE,"E7.38.1"),sQuery(id+"F0.wireOp",EDGE,"E7.38.2"),sQuery(id+"F0.wireOp",EDGE,"E7.38.3"),sQuery(id+"F0.wireOp",EDGE,"E7.38.4"),sQuery(id+"F0.wireOp",EDGE,"E7.38.5"),sQuery(id+"F0.wireOp",EDGE,"E7.39.0"),sQuery(id+"F0.wireOp",EDGE,"E7.39.1"),sQuery(id+"F0.wireOp",EDGE,"E7.39.2"),sQuery(id+"F0.wireOp",EDGE,"E7.39.3"),sQuery(id+"F0.wireOp",EDGE,"E7.39.4"),sQuery(id+"F0.wireOp",EDGE,"E7.39.5"),sQuery(id+"F0.wireOp",EDGE,"E7.40.0"),sQuery(id+"F0.wireOp",EDGE,"E7.40.1"),sQuery(id+"F0.wireOp",EDGE,"E7.40.2"),sQuery(id+"F0.wireOp",EDGE,"E7.40.3"),sQuery(id+"F0.wireOp",EDGE,"E7.40.4"),sQuery(id+"F0.wireOp",EDGE,"E7.40.5"),sQuery(id+"F0.wireOp",EDGE,"E7.41.0"),sQuery(id+"F0.wireOp",EDGE,"E7.41.1"),sQuery(id+"F0.wireOp",EDGE,"E7.41.2"),sQuery(id+"F0.wireOp",EDGE,"E7.41.3"),sQuery(id+"F0.wireOp",EDGE,"E7.41.4"),sQuery(id+"F0.wireOp",EDGE,"E7.41.5"),sQuery(id+"F0.wireOp",EDGE,"E7.42.0"),sQuery(id+"F0.wireOp",EDGE,"E7.42.1"),sQuery(id+"F0.wireOp",EDGE,"E7.42.2"),sQuery(id+"F0.wireOp",EDGE,"E7.42.3"),sQuery(id+"F0.wireOp",EDGE,"E7.42.4"),sQuery(id+"F0.wireOp",EDGE,"E7.42.5"),sQuery(id+"F0.wireOp",EDGE,"E7.43.0"),sQuery(id+"F0.wireOp",EDGE,"E7.43.1"),sQuery(id+"F0.wireOp",EDGE,"E7.43.2"),sQuery(id+"F0.wireOp",EDGE,"E7.43.3"),sQuery(id+"F0.wireOp",EDGE,"E7.43.4"),sQuery(id+"F0.wireOp",EDGE,"E7.43.5"),sQuery(id+"F0.wireOp",EDGE,"E7.44.0"),sQuery(id+"F0.wireOp",EDGE,"E7.44.1"),sQuery(id+"F0.wireOp",EDGE,"E7.44.2"),sQuery(id+"F0.wireOp",EDGE,"E7.44.3"),sQuery(id+"F0.wireOp",EDGE,"E7.44.4"),sQuery(id+"F0.wireOp",EDGE,"E7.44.5"),sQuery(id+"F0.wireOp",EDGE,"E7.45.0"),sQuery(id+"F0.wireOp",EDGE,"E7.45.1"),sQuery(id+"F0.wireOp",EDGE,"E7.45.2"),sQuery(id+"F0.wireOp",EDGE,"E7.45.3"),sQuery(id+"F0.wireOp",EDGE,"E7.45.4"),sQuery(id+"F0.wireOp",EDGE,"E7.45.5"),sQuery(id+"F0.wireOp",EDGE,"E7.46.0"),sQuery(id+"F0.wireOp",EDGE,"E7.46.1"),sQuery(id+"F0.wireOp",EDGE,"E7.46.2"),sQuery(id+"F0.wireOp",EDGE,"E7.46.3"),sQuery(id+"F0.wireOp",EDGE,"E7.46.4"),sQuery(id+"F0.wireOp",EDGE,"E7.46.5"),sQuery(id+"F0.wireOp",EDGE,"E7.47.0"),sQuery(id+"F0.wireOp",EDGE,"E7.47.1"),sQuery(id+"F0.wireOp",EDGE,"E7.47.2"),sQuery(id+"F0.wireOp",EDGE,"E7.47.3"),sQuery(id+"F0.wireOp",EDGE,"E7.47.4"),sQuery(id+"F0.wireOp",EDGE,"E7.47.5"),sQuery(id+"F0.wireOp",EDGE,"E7.48.0"),sQuery(id+"F0.wireOp",EDGE,"E7.48.1"),sQuery(id+"F0.wireOp",EDGE,"E7.48.2"),sQuery(id+"F0.wireOp",EDGE,"E7.48.3"),sQuery(id+"F0.wireOp",EDGE,"E7.48.4"),sQuery(id+"F0.wireOp",EDGE,"E7.48.5"),sQuery(id+"F0.wireOp",EDGE,"E7.49.0"),sQuery(id+"F0.wireOp",EDGE,"E7.49.1"),sQuery(id+"F0.wireOp",EDGE,"E7.49.2"),sQuery(id+"F0.wireOp",EDGE,"E7.49.3"),sQuery(id+"F0.wireOp",EDGE,"E7.49.4"),sQuery(id+"F0.wireOp",EDGE,"E7.49.5"),sQuery(id+"F0.wireOp",EDGE,"E7.50.0"),sQuery(id+"F0.wireOp",EDGE,"E7.50.1"),sQuery(id+"F0.wireOp",EDGE,"E7.50.2"),sQuery(id+"F0.wireOp",EDGE,"E7.50.3"),sQuery(id+"F0.wireOp",EDGE,"E7.50.4"),sQuery(id+"F0.wireOp",EDGE,"E7.50.5"),sQuery(id+"F0.wireOp",EDGE,"E7.51.0"),sQuery(id+"F0.wireOp",EDGE,"E7.51.1"),sQuery(id+"F0.wireOp",EDGE,"E7.51.2"),sQuery(id+"F0.wireOp",EDGE,"E7.51.3"),sQuery(id+"F0.wireOp",EDGE,"E7.51.4"),sQuery(id+"F0.wireOp",EDGE,"E7.51.5"),sQuery(id+"F0.wireOp",EDGE,"E7.52.0"),sQuery(id+"F0.wireOp",EDGE,"E7.52.1"),sQuery(id+"F0.wireOp",EDGE,"E7.52.2"),sQuery(id+"F0.wireOp",EDGE,"E7.52.3"),sQuery(id+"F0.wireOp",EDGE,"E7.52.4"),sQuery(id+"F0.wireOp",EDGE,"E7.52.5"),sQuery(id+"F0.wireOp",EDGE,"E7.53.0"),sQuery(id+"F0.wireOp",EDGE,"E7.53.1"),sQuery(id+"F0.wireOp",EDGE,"E7.53.2"),sQuery(id+"F0.wireOp",EDGE,"E7.53.3"),sQuery(id+"F0.wireOp",EDGE,"E7.53.4"),sQuery(id+"F0.wireOp",EDGE,"E7.53.5"),sQuery(id+"F0.wireOp",EDGE,"E7.54.0"),sQuery(id+"F0.wireOp",EDGE,"E7.54.1"),sQuery(id+"F0.wireOp",EDGE,"E7.54.2"),sQuery(id+"F0.wireOp",EDGE,"E7.54.3"),sQuery(id+"F0.wireOp",EDGE,"E7.54.4"),sQuery(id+"F0.wireOp",EDGE,"E7.54.5"),sQuery(id+"F0.wireOp",EDGE,"E7.55.0"),sQuery(id+"F0.wireOp",EDGE,"E7.55.1"),sQuery(id+"F0.wireOp",EDGE,"E7.55.2"),sQuery(id+"F0.wireOp",EDGE,"E7.55.3"),sQuery(id+"F0.wireOp",EDGE,"E7.55.4"),sQuery(id+"F0.wireOp",EDGE,"E7.55.5"),sQuery(id+"F0.wireOp",EDGE,"E7.56.0"),sQuery(id+"F0.wireOp",EDGE,"E7.56.1"),sQuery(id+"F0.wireOp",EDGE,"E7.56.2"),sQuery(id+"F0.wireOp",EDGE,"E7.56.3"),sQuery(id+"F0.wireOp",EDGE,"E7.56.4"),sQuery(id+"F0.wireOp",EDGE,"E7.56.5"),sQuery(id+"F0.wireOp",EDGE,"E7.57.0"),sQuery(id+"F0.wireOp",EDGE,"E7.57.1"),sQuery(id+"F0.wireOp",EDGE,"E7.57.2"),sQuery(id+"F0.wireOp",EDGE,"E7.57.3"),sQuery(id+"F0.wireOp",EDGE,"E7.57.4"),sQuery(id+"F0.wireOp",EDGE,"E7.57.5"),sQuery(id+"F0.wireOp",EDGE,"E7.58.0"),sQuery(id+"F0.wireOp",EDGE,"E7.58.1"),sQuery(id+"F0.wireOp",EDGE,"E7.58.2"),sQuery(id+"F0.wireOp",EDGE,"E7.58.3"),sQuery(id+"F0.wireOp",EDGE,"E7.58.4"),sQuery(id+"F0.wireOp",EDGE,"E7.58.5"),sQuery(id+"F0.wireOp",EDGE,"E7.59.0"),sQuery(id+"F0.wireOp",EDGE,"E7.59.1"),sQuery(id+"F0.wireOp",EDGE,"E7.59.2"),sQuery(id+"F0.wireOp",EDGE,"E7.59.3"),sQuery(id+"F0.wireOp",EDGE,"E7.59.4"),sQuery(id+"F0.wireOp",EDGE,"E7.59.5"),sQuery(id+"F0.wireOp",EDGE,"E8"),sQuery(id+"F0.wireOp",EDGE,"E9"),sQuery(id+"F0.wireOp",EDGE,"E10"),sQuery(id+"F0.wireOp",EDGE,"E11.filletArc"),sQuery(id+"F0.wireOp",EDGE,"E12.filletArc"),sQuery(id+"F0.wireOp",EDGE,"E13.filletArc"),sQuery(id+"F0.wireOp",EDGE,"E14.MirrorCS"),sQuery(id+"F0.wireOp",EDGE,"E15.MirrorCS"),sQuery(id+"F0.wireOp",EDGE,"E16.MirrorCS"),sQuery(id+"F0.wireOp",EDGE,"E17.MirrorCS"),sQuery(id+"F0.wireOp",EDGE,"E18.MirrorCS"),sQuery(id+"F0.wireOp",EDGE,"E19.MirrorCS"),sQuery(id+"F0.wireOp",EDGE,"E21.MirrorCS"),sQuery(id+"F0.wireOp",EDGE,"E22.MirrorCS"),sQuery(id+"F0.wireOp",EDGE,"E23.MirrorCS"),sQuery(id+"F0.wireOp",EDGE,"E24.MirrorCS"),sQuery(id+"F0.wireOp",EDGE,"E25.MirrorCS"),sQuery(id+"F0.wireOp",EDGE,"E20.MirrorCS"),sQuery(id+"F0.wireOp",EDGE,"E27.MirrorCS"),sQuery(id+"F0.wireOp",EDGE,"E28.MirrorCS"),sQuery(id+"F0.wireOp",EDGE,"E29.MirrorCS"),sQuery(id+"F0.wireOp",EDGE,"E30.MirrorCS"),sQuery(id+"F0.wireOp",EDGE,"E31.MirrorCS"),sQuery(id+"F0.wireOp",EDGE,"E32.MirrorCS"),sQuery(id+"F0.wireOp",EDGE,"E33"),sQuery(id+"F0.wireOp",EDGE,"E34.1.0"),sQuery(id+"F0.wireOp",EDGE,"E34.2.0"),sQuery(id+"F0.wireOp",EDGE,"E34.3.0"),sQuery(id+"F0.wireOp",EDGE,"E34.4.0"),sQuery(id+"F0.wireOp",EDGE,"E34.5.0"),sQuery(id+"F0.wireOp",EDGE,"E34.6.0"),sQuery(id+"F0.wireOp",EDGE,"E34.7.0"),sQuery(id+"F0.wireOp",EDGE,"E34.8.0"),sQuery(id+"F0.wireOp",EDGE,"E34.9.0"),sQuery(id+"F0.wireOp",EDGE,"E34.10.0"),sQuery(id+"F0.wireOp",EDGE,"E34.11.0"),sQuery(id+"F0.wireOp",EDGE,"E34.12.0"),sQuery(id+"F0.wireOp",EDGE,"E34.13.0"),sQuery(id+"F0.wireOp",EDGE,"E34.14.0"),sQuery(id+"F0.wireOp",EDGE,"E34.15.0"),sQuery(id+"F0.wireOp",EDGE,"E34.16.0"),sQuery(id+"F0.wireOp",EDGE,"E34.17.0"),sQuery(id+"F0.wireOp",EDGE,"E34.18.0"),sQuery(id+"F0.wireOp",EDGE,"E34.19.0"),sQuery(id+"F0.wireOp",EDGE,"E34.20.0"),sQuery(id+"F0.wireOp",EDGE,"E34.21.0"),sQuery(id+"F0.wireOp",EDGE,"E34.22.0"),sQuery(id+"F0.wireOp",EDGE,"E34.23.0"),sQuery(id+"F0.wireOp",EDGE,"E34.24.0"),sQuery(id+"F0.wireOp",EDGE,"E34.25.0"),sQuery(id+"F0.wireOp",EDGE,"E34.26.0"),sQuery(id+"F0.wireOp",EDGE,"E34.27.0"),sQuery(id+"F0.wireOp",EDGE,"E34.28.0"),sQuery(id+"F0.wireOp",EDGE,"E34.29.0"),sQuery(id+"F0.wireOp",EDGE,"E34.30.0"),sQuery(id+"F0.wireOp",EDGE,"E34.31.0"),sQuery(id+"F0.wireOp",EDGE,"E34.32.0"),sQuery(id+"F0.wireOp",EDGE,"E34.33.0"),sQuery(id+"F0.wireOp",EDGE,"E34.34.0"),sQuery(id+"F0.wireOp",EDGE,"E34.35.0"),sQuery(id+"F0.wireOp",EDGE,"E34.36.0"),sQuery(id+"F0.wireOp",EDGE,"E34.37.0"),sQuery(id+"F0.wireOp",EDGE,"E34.38.0"),sQuery(id+"F0.wireOp",EDGE,"E34.39.0"),sQuery(id+"F0.wireOp",EDGE,"E34.40.0"),sQuery(id+"F0.wireOp",EDGE,"E34.41.0"),sQuery(id+"F0.wireOp",EDGE,"E34.42.0"),sQuery(id+"F0.wireOp",EDGE,"E34.43.0"),sQuery(id+"F0.wireOp",EDGE,"E34.44.0"),sQuery(id+"F0.wireOp",EDGE,"E34.45.0"),sQuery(id+"F0.wireOp",EDGE,"E34.46.0"),sQuery(id+"F0.wireOp",EDGE,"E34.47.0"),sQuery(id+"F0.wireOp",EDGE,"E34.48.0"),sQuery(id+"F0.wireOp",EDGE,"E34.49.0"),sQuery(id+"F0.wireOp",EDGE,"E34.50.0"),sQuery(id+"F0.wireOp",EDGE,"E34.51.0"),sQuery(id+"F0.wireOp",EDGE,"E34.52.0"),sQuery(id+"F0.wireOp",EDGE,"E34.53.0"),sQuery(id+"F0.wireOp",EDGE,"E34.54.0"),sQuery(id+"F0.wireOp",EDGE,"E34.55.0"),sQuery(id+"F0.wireOp",EDGE,"E34.56.0"),sQuery(id+"F0.wireOp",EDGE,"E34.57.0"),sQuery(id+"F0.wireOp",EDGE,"E34.58.0"),sQuery(id+"F0.wireOp",EDGE,"E34.59.0")])],"isStart":true});
            fillet(context, id + "F5", {"entities" : qUnion([Q0, Q1, Q2]), "radius" : 1.5 * mm, "tangentPropagation" : true, "allowEdgeOverflow" : false});
        }
    });
